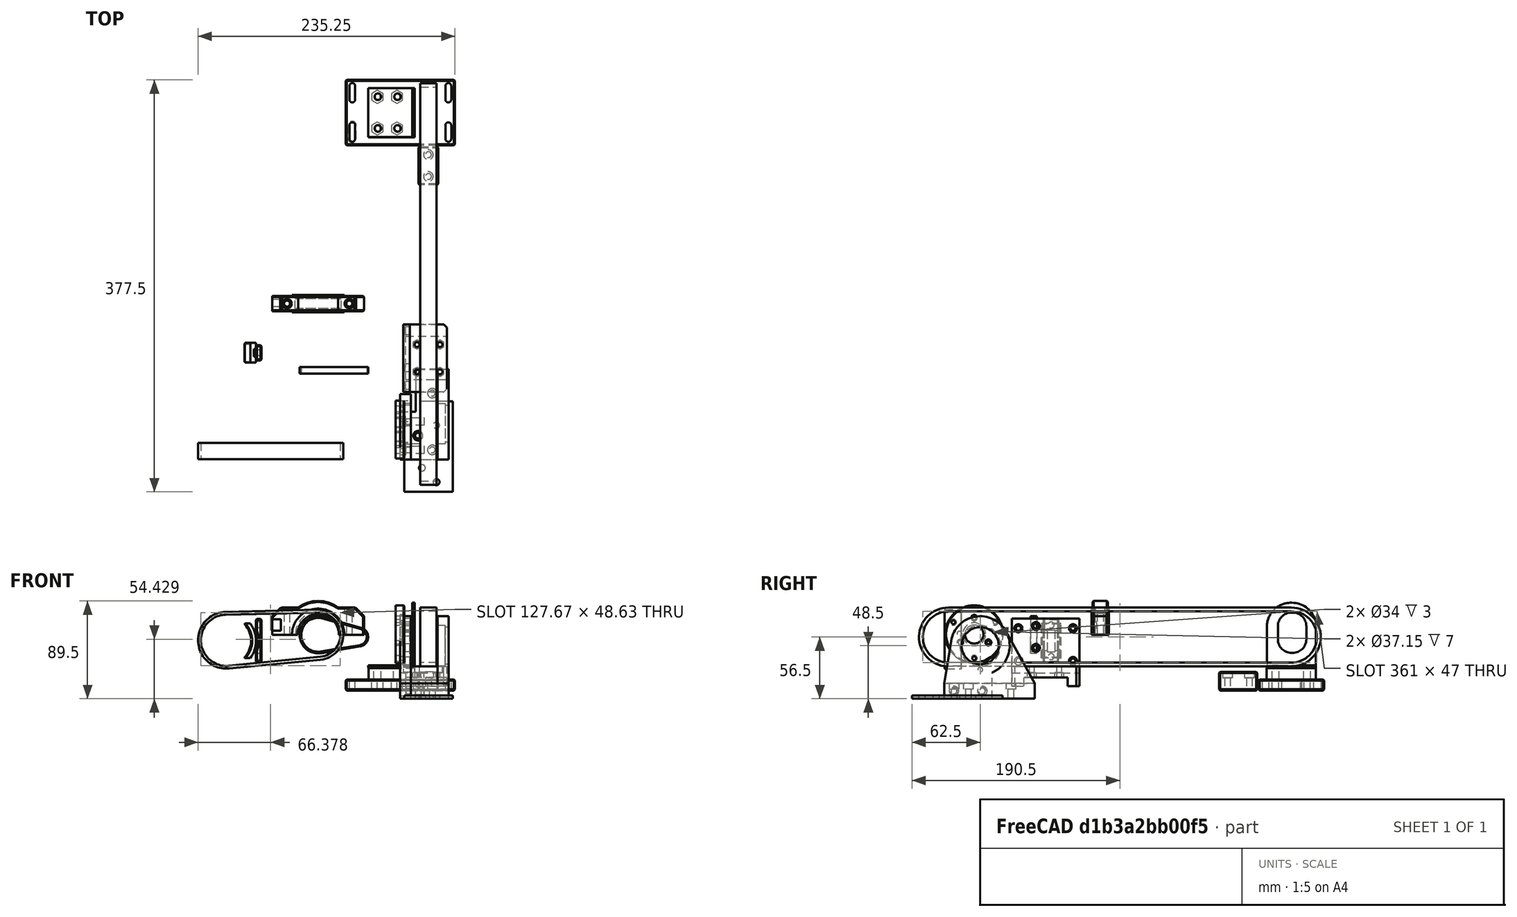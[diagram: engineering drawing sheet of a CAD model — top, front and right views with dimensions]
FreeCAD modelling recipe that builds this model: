
FCSTD DOCUMENT  (FreeCAD 0.21R33668 +26 (Git))
Label: FFB_Yoke_Assembly_v2
License: All rights reserved
LicenseURL: http://en.wikipedia.org/wiki/All_rights_reserved
objects: Sketcher::SketchObject×45, PartDesign::Pad×19, PartDesign::Pocket×17, App::Link×15, PartDesign::Body×14, PartDesign::Chamfer×13, PartDesign::Hole×9, Mesh::Feature×6, App::Part×3, PartDesign::Fillet×1, PartDesign::FeatureBase×1
note: 178 computed .brp shape members not serialized (recipe doc carries the construction recipe); baked Part::Feature solids carry a one-line shape summary decoded from their .brp
EXTERNAL_REF file=Parts/Frame.FCStd obj=Part
EXTERNAL_REF file=Parts/Frame_Roll_Limit_IR_Sensor_Mount.FCStd obj=Body022
EXTERNAL_REF file=Parts/Frame_Roll_Limit_Stop.FCStd obj=Body019
EXTERNAL_REF file=Parts/Roll_Motor_Mount.FCStd obj=Body005
EXTERNAL_REF file=Parts/Roll_Encoder_Mount.FCStd obj=Body026
EXTERNAL_REF file=Parts/GearMotor.FCStd obj=Part
EXTERNAL_REF file=Parts/Encoder.FCStd obj=Part
EXTERNAL_REF file=Parts/Yoke_Bearing.FCStd obj=Body008
EXTERNAL_REF file=Parts/Yoke_Roll_IR_Limit_Ring.FCStd obj=Body028
EXTERNAL_REF file=Parts/Yoke_Encoder_Pulley.FCStd obj=Body
EXTERNAL_REF file=Parts/Roll_Encoder_Pulley.FCStd obj=Part
EXTERNAL_REF file=Parts/Yoke Column.FCStd obj=Part

FEATURE [App::Link] Link  label="Frame"
  LinkedObject = -> <external Parts/Frame.FCStd>#Part
FEATURE [App::Link] Link001  label="Frame_Roll_IR_Sensor_Mount"
  LinkPlacement = pos=(0,-24,0) rot=(0,0,1;0rad)
  LinkedObject = -> <external Parts/Frame_Roll_Limit_IR_Sensor_Mount.FCStd>#Body022
  Placement = pos=(0,-24,0) rot=(0,0,1;0rad)
FEATURE [App::Link] Link002  label="Roll_Limit_Stop"
  LinkPlacement = pos=(0,24,0) rot=(0,0,1;3.14159rad)
  LinkedObject = -> <external Parts/Frame_Roll_Limit_Stop.FCStd>#Body019
  Placement = pos=(0,24,0) rot=(0,0,1;3.14159rad)
FEATURE [App::Link] Link003  label="Roll_Motor_Mount"
  LinkPlacement = pos=(-12,-24,0) rot=(0,0,1;0rad)
  LinkedObject = -> <external Parts/Roll_Motor_Mount.FCStd>#Body005
  Placement = pos=(-12,-24,0) rot=(0,0,1;0rad)
FEATURE [App::Link] Link004  label="Roll_Encoder _Mount"
  LinkPlacement = pos=(1,-27,0) rot=(0,0,1;0rad)
  LinkedObject = -> <external Parts/Roll_Encoder_Mount.FCStd>#Body026
  Placement = pos=(1,-27,0) rot=(0,0,1;0rad)
FEATURE [App::Link] Link005  label="Roll_GearMotor"
  LinkPlacement = pos=(-9,-24,0) rot=(0,0,1;0rad)
  LinkedObject = -> <external Parts/GearMotor.FCStd>#Part
  Placement = pos=(-9,-24,0) rot=(0,0,1;0rad)
FEATURE [App::Link] Link006  label="Pitch_GearMotor"
  LinkPlacement = pos=(88.5,350,3) rot=(0,0,1;1.5708rad)
  LinkedObject = -> <external Parts/GearMotor.FCStd>#Part
  Placement = pos=(88.5,350,3) rot=(0,0,1;1.5708rad)
FEATURE [App::Link] Link007  label="Roll_Encoder"
  LinkPlacement = pos=(-1,-30,0) rot=(0,0,1;0rad)
  LinkedObject = -> <external Parts/Encoder.FCStd>#Part
  Placement = pos=(-1,-30,0) rot=(0,0,1;0rad)
FEATURE [App::Link] Link008  label="Rear_Bearing"
  LinkPlacement = pos=(0,-27,0) rot=(0,0,1;0rad)
  LinkedObject = -> <external Parts/Yoke_Bearing.FCStd>#Body008
  Placement = pos=(0,-27,0) rot=(0,0,1;0rad)
FEATURE [App::Link] Link009  label="Front_Bearing"
  LinkPlacement = pos=(0,-127,0) rot=(0,0,1;0rad)
  LinkedObject = -> <external Parts/Yoke_Bearing.FCStd>#Body008
  Placement = pos=(0,-127,0) rot=(0,0,1;0rad)
FEATURE [App::Link] Link011  label="IR _Cam"
  LinkPlacement = pos=(0,3.75,-6.04e-14) rot=(-1,0,0;1.5708rad)
  LinkedObject = -> <external Parts/Yoke_Roll_IR_Limit_Ring.FCStd>#Body028
  Placement = pos=(0,3.75,-6.04e-14) rot=(-1,0,0;1.5708rad)
FEATURE [App::Link] Link012  label="Yoke_Roll_Encoder_Pulley"
  LinkPlacement = pos=(0,44.25,0) rot=(0,0,1;0rad)
  LinkedObject = -> <external Parts/Yoke_Encoder_Pulley.FCStd>#Body
  Placement = pos=(0,44.25,0) rot=(0,0,1;0rad)
FEATURE [App::Link] Link015  label="Roll_Encoder_Pulley"
  LinkPlacement = pos=(37,43,-2) rot=(1,0,0;1.5708rad)
  LinkedObject = -> <external Parts/Roll_Encoder_Pulley.FCStd>#Part
  Placement = pos=(37,43,-2) rot=(1,0,0;1.5708rad)
FEATURE [App::Link] Link019  label="Pitch_Encoder"
  LinkPlacement = pos=(152.75,-77,0) rot=(0,0,1;1.5708rad)
  LinkedObject = -> <external Parts/Encoder.FCStd>#Part
  Placement = pos=(152.75,-77,0) rot=(0,0,1;1.5708rad)
FEATURE [App::Link] Link021  label="Yoke_Column"
  LinkPlacement = pos=(0,-27,0) rot=(0,0,1;0rad)
  LinkedObject = -> <external Parts/Yoke Column.FCStd>#Part
  Placement = pos=(0,-27,0) rot=(0,0,1;0rad)
FEATURE [Sketcher::SketchObject] Sketch
  AttachmentOffset = pos=(0,0,-19) rot=(0,0,1;0rad)
  FullyConstrained = true
  MapMode = 5
  Placement = pos=(0,19,4.2e-15) rot=(1,0,0;1.5708rad)
  Support = -> [XZ_Plane]
  sketch-geometry (8):
    g0: LineSegment StartX=76 StartY=15 StartZ=0 EndX=76 EndY=-35 EndZ=0
    g1: LineSegment StartX=78 StartY=-47 StartZ=0 EndX=116 EndY=-47 EndZ=0
    g2: LineSegment StartX=116 StartY=-47 StartZ=0 EndX=116 EndY=-29 EndZ=0
    g3: LineSegment StartX=116 StartY=-29 StartZ=0 EndX=82 EndY=-29 EndZ=0
    g4: LineSegment StartX=82 StartY=-29 StartZ=0 EndX=82 EndY=15 EndZ=0
    g5: LineSegment StartX=82 StartY=15 StartZ=0 EndX=76 EndY=15 EndZ=0
    g6: LineSegment StartX=76 StartY=-35 StartZ=0 EndX=78 EndY=-35 EndZ=0
    g7: LineSegment StartX=78 StartY=-35 StartZ=0 EndX=78 EndY=-47 EndZ=0
  constraints (24):
    c: Vertical(g0)
    c: Horizontal(g1)
    c: Coincident(g1,g2)
    c: Coincident(g2,g3)
    c: Horizontal(g3)
    c: Coincident(g3,g4)
    c: Vertical(g4)
    c: Coincident(g4,g5)
    c: Coincident(g5,g0)
    c: Horizontal(g5)
    c: Vertical(g2)
    c: Distance(g2) = 18
    c: Distance(g5) = 6
    c: Distance(g4) = 44
    c: DistanceY(g0) = 15
    c: DistanceX(g0) = 76
    c: Horizontal(g6)
    c: Coincident(g7,g6)
    c: Vertical(g7)
    c: Distance(g6) = 2
    c: Distance(g7) = 12
    c: Distance(g3) = 34
    c: Coincident(g0,g6)
    c: Coincident(g1,g7)
FEATURE [PartDesign::Pad] Pad
  Direction = (0,-1,-2e-16)
  Length = 62
  Length2 = 10
  Placement = pos=(0,0,0) rot=(1,0,0;1.5708rad)
  Profile = -> Sketch
  ReferenceAxis = -> Sketch [N_Axis]
  Reversed = true
  Type = 0
FEATURE [Sketcher::SketchObject] Sketch001
  FullyConstrained = true
  MapMode = 5
  Placement = pos=(0,0,0) rot=(1,0,0;1.5708rad)
  Support = -> [XZ_Plane002]
  sketch-geometry (6):
    g0: LineSegment StartX=42 StartY=0 StartZ=0 EndX=42 EndY=25 EndZ=0
    g1: LineSegment StartX=42 StartY=25 StartZ=0 EndX=18.3303 EndY=25 EndZ=0
    g2: LineSegment StartX=-42 StartY=25 StartZ=0 EndX=-42 EndY=0 EndZ=0
    g3: LineSegment StartX=-42 StartY=0 StartZ=0 EndX=42 EndY=0 EndZ=0
    g4: ArcOfCircle CenterX=0 CenterY=0 CenterZ=0 NormalX=0 NormalY=0 NormalZ=1 AngleXU=0 Radius=31 StartAngle=0.938126 EndAngle=2.20347
    g5: LineSegment StartX=-18.3303 StartY=25 StartZ=0 EndX=-42 EndY=25 EndZ=0
  constraints (18):
    c: Coincident(g0,g1)
    c: Coincident(g5,g2)
    c: Horizontal(g1)
    c: Vertical(g0)
    c: Vertical(g2)
    c: PointOnObject(g2,g-1)
    c: Distance(g0) = 25
    c: DistanceX(g5,g-1) = 42
    c: Horizontal(g0,g-1)
    c: Coincident(g3,g2)
    c: Coincident(g3,g0)
    c: Coincident(g4,g-1)
    c: Diameter(g4) = 62
    c: Coincident(g1,g4)
    c: Coincident(g5,g4)
    c: Distance(g2,g0) = 84
    c: Horizontal(g5)
    c: Horizontal(g1,g4)
FEATURE [PartDesign::Pad] Pad001
  Direction = (0,-1,-2e-16)
  Length = 14
  Length2 = 10
  Midplane = true
  Placement = pos=(0,0,0) rot=(1,0,0;1.5708rad)
  Profile = -> Sketch001
  ReferenceAxis = -> Sketch001 [N_Axis]
  Type = 0
FEATURE [Sketcher::SketchObject] Sketch002
  FullyConstrained = true
  MapMode = 5
  Placement = pos=(0,0,0) rot=(1,0,0;1.5708rad)
  Support = -> [XZ_Plane002]
  sketch-geometry (2):
    g0: ArcOfCircle CenterX=0 CenterY=0 CenterZ=0 NormalX=0 NormalY=0 NormalZ=1 AngleXU=0 Radius=19 StartAngle=0 EndAngle=3.14159
    g1: LineSegment StartX=-19 StartY=0 StartZ=0 EndX=19 EndY=0 EndZ=0
  constraints (6):
    c: Horizontal(g0,g0)
    c: Horizontal(g0,g0)
    c: Coincident(g0,g-1)
    c: Diameter(g0) = 38
    c: Coincident(g1,g0)
    c: Coincident(g1,g0)
FEATURE [Sketcher::SketchObject] Sketch003
  FullyConstrained = true
  MapMode = 5
  Placement = pos=(0,0,0) rot=(1,0,0;1.5708rad)
  Support = -> [XZ_Plane002]
  sketch-geometry (2):
    g0: ArcOfCircle CenterX=0 CenterY=5.9e-15 CenterZ=0 NormalX=0 NormalY=0 NormalZ=1 AngleXU=0 Radius=24 StartAngle=0 EndAngle=3.14159
    g1: LineSegment StartX=-24 StartY=5.9e-15 StartZ=0 EndX=24 EndY=5.9e-15 EndZ=0
  constraints (6):
    c: Diameter(g0) = 48
    c: Horizontal(g0,g0)
    c: Horizontal(g0,g0)
    c: Coincident(g0,g-1)
    c: Coincident(g1,g0)
    c: Coincident(g1,g0)
FEATURE [Sketcher::SketchObject] Sketch004
  FullyConstrained = true
  MapMode = 5
  Placement = pos=(0,0,0) rot=(1,0,0;1.5708rad)
  Support = -> [XZ_Plane002]
  sketch-geometry (2):
    g0: ArcOfCircle CenterX=0 CenterY=0 CenterZ=0 NormalX=0 NormalY=0 NormalZ=1 AngleXU=0 Radius=21 StartAngle=0 EndAngle=3.14159
    g1: LineSegment StartX=-21 StartY=2.6e-15 StartZ=0 EndX=21 EndY=0 EndZ=0
  constraints (6):
    c: PointOnObject(g0,g-1)
    c: Diameter(g0) = 42
    c: Coincident(g0,g-1)
    c: Horizontal(g0,g0)
    c: Coincident(g1,g0)
    c: Coincident(g1,g0)
FEATURE [PartDesign::Pad] Pad002
  BaseFeature = -> Pad001
  Direction = (0,-1,-2e-16)
  Length = 16
  Length2 = 10
  Midplane = true
  Placement = pos=(0,0,0) rot=(1,0,0;1.5708rad)
  Profile = -> Sketch003
  ReferenceAxis = -> Sketch003 [N_Axis]
  Type = 0
FEATURE [PartDesign::Pocket] Pocket
  BaseFeature = -> Pad002
  Direction = (0,1,2e-16)
  Length = 16
  Length2 = 5
  Midplane = true
  Placement = pos=(0,0,0) rot=(1,0,0;1.5708rad)
  Profile = -> Sketch002
  ReferenceAxis = -> Sketch002 [N_Axis]
  Type = 0
FEATURE [PartDesign::Pocket] Pocket001
  BaseFeature = -> Pocket
  Direction = (0,1,2e-16)
  Length = 9.2
  Length2 = 5
  Midplane = true
  Placement = pos=(0,0,0) rot=(1,0,0;1.5708rad)
  Profile = -> Sketch004
  ReferenceAxis = -> Sketch004 [N_Axis]
  Type = 0
FEATURE [Sketcher::SketchObject] Sketch006
  FullyConstrained = true
  MapMode = 5
  Support = -> [XY_Plane002]
  sketch-geometry (2):
    g0: Circle CenterX=-28.5 CenterY=0 CenterZ=0 NormalX=0 NormalY=0 NormalZ=1 AngleXU=0 Radius=2.75
    g1: Circle CenterX=28.5 CenterY=0 CenterZ=0 NormalX=0 NormalY=0 NormalZ=1 AngleXU=0 Radius=2.75
  constraints (5):
    c: Symmetric(g0,g1,g-1)
    c: Horizontal(g0,g-1)
    c: Distance(g0,g1) = 57
    c: Equal(g1,g0)
    c: Diameter(g1) = 5.5
FEATURE [PartDesign::Pocket] Pocket003
  BaseFeature = -> Pocket001
  Direction = (0,0,-1)
  Length = 5
  Length2 = 5
  Placement = pos=(0,0,0) rot=(1,0,0;1.5708rad)
  Profile = -> Sketch006
  ReferenceAxis = -> Sketch006 [N_Axis]
  Reversed = true
  Type = 1
FEATURE [Sketcher::SketchObject] Sketch007
  AttachmentOffset = pos=(0,0,25) rot=(0,0,1;0rad)
  FullyConstrained = true
  MapMode = 5
  Placement = pos=(0,0,25) rot=(0,0,1;0rad)
  Support = -> [XY_Plane002]
  sketch-geometry (2):
    g0: Circle CenterX=-28.5 CenterY=0 CenterZ=0 NormalX=0 NormalY=0 NormalZ=1 AngleXU=0 Radius=4.35
    g1: Circle CenterX=28.5 CenterY=0 CenterZ=0 NormalX=0 NormalY=0 NormalZ=1 AngleXU=0 Radius=4.35
  constraints (5):
    c: PointOnObject(g0,g-1)
    c: Symmetric(g0,g1,g-1)
    c: Distance(g0,g1) = 57
    c: Equal(g0,g1)
    c: Diameter(g0) = 8.7
FEATURE [PartDesign::Pocket] Pocket004
  BaseFeature = -> Pocket003
  Direction = (0,0,-1)
  Length = 5.4
  Length2 = 5
  Placement = pos=(0,0,0) rot=(1,0,0;1.5708rad)
  Profile = -> Sketch007
  ReferenceAxis = -> Sketch007 [N_Axis]
  Type = 0
FEATURE [Mesh::Feature] HTD_32_5M_15_Pulley_v8  label="HTD 32 5M 15 Pulley v8"
  Placement = pos=(111.5,275,-2) rot=(0,0,1;3.14159rad)
FEATURE [Sketcher::SketchObject] Sketch008
  FullyConstrained = true
  MapMode = 5
  Placement = pos=(0,0,0) rot=(0.57735,0.57735,0.57735;2.0944rad)
  Support = -> [YZ_Plane003]
  sketch-geometry (4):
    g0: ArcOfCircle CenterX=-39 CenterY=-3 CenterZ=0 NormalX=0 NormalY=0 NormalZ=1 AngleXU=0 Radius=27 StartAngle=1.5708 EndAngle=4.71239
    g1: ArcOfCircle CenterX=275 CenterY=-3 CenterZ=0 NormalX=0 NormalY=0 NormalZ=1 AngleXU=0 Radius=27 StartAngle=4.71239 EndAngle=7.85398
    g2: LineSegment StartX=-39 StartY=24 StartZ=0 EndX=275 EndY=24 EndZ=0
    g3: LineSegment StartX=275 StartY=-30 StartZ=0 EndX=-39 EndY=-30 EndZ=0
  constraints (13):
    c: Diameter(g0) = 54
    c: Equal(g1,g0)
    c: DistanceY(g0) = -3
    c: DistanceX(g0) = -39
    c: Horizontal(g2)
    c: Coincident(g1,g2)
    c: Coincident(g1,g3)
    c: Coincident(g0,g3)
    c: Tangent(g0,g2) = 1.5708
    c: DistanceX(g1) = 275
    c: Vertical(g0,g0)
    c: Vertical(g1,g1)
    c: Vertical(g1,g1)
FEATURE [PartDesign::Pad] Pad003
  Direction = (1,-2e-16,3e-16)
  Length = 15
  Length2 = 10
  Midplane = true
  Placement = pos=(0,0,0) rot=(0.57735,0.57735,0.57735;2.0944rad)
  Profile = -> Sketch008
  ReferenceAxis = -> Sketch008 [N_Axis]
  Type = 0
FEATURE [Sketcher::SketchObject] Sketch009
  FullyConstrained = true
  MapMode = 5
  Placement = pos=(0,0,0) rot=(0.57735,0.57735,0.57735;2.0944rad)
  Support = -> [YZ_Plane003]
  sketch-geometry (4):
    g0: ArcOfCircle CenterX=-39 CenterY=-3 CenterZ=0 NormalX=0 NormalY=0 NormalZ=1 AngleXU=0 Radius=23.5 StartAngle=1.5708 EndAngle=4.71239
    g1: ArcOfCircle CenterX=275 CenterY=-3 CenterZ=0 NormalX=0 NormalY=0 NormalZ=1 AngleXU=0 Radius=23.5 StartAngle=4.71239 EndAngle=7.85398
    g2: LineSegment StartX=-39 StartY=20.5 StartZ=0 EndX=275 EndY=20.5 EndZ=0
    g3: LineSegment StartX=275 StartY=-26.5 StartZ=0 EndX=-39 EndY=-26.5 EndZ=0
  constraints (13):
    c: Diameter(g1) = 47
    c: Equal(g1,g0)
    c: DistanceY(g0) = -3
    c: DistanceX(g0) = -39
    c: DistanceX(g1) = 275
    c: Horizontal(g2)
    c: Vertical(g2,g0)
    c: Vertical(g0,g3)
    c: Coincident(g0,g3)
    c: Coincident(g0,g2)
    c: Tangent(g1,g2) = 1.5708
    c: Coincident(g1,g3)
    c: Vertical(g1,g1)
FEATURE [PartDesign::Pocket] Pocket005
  BaseFeature = -> Pad003
  Direction = (-1,2e-16,-3e-16)
  Length = 15
  Length2 = 5
  Midplane = true
  Placement = pos=(0,0,0) rot=(0.57735,0.57735,0.57735;2.0944rad)
  Profile = -> Sketch009
  ReferenceAxis = -> Sketch009 [N_Axis]
  Type = 0
FEATURE [PartDesign::Body] Body001002  label="Pitch_Belt"
  Group = -> [Sketch008,Pad003,Sketch009,Pocket005]
  Origin = -> Origin003
  Placement = pos=(101,0,1) rot=(0,0,1;0rad)
  Tip = -> Pocket005
FEATURE [Mesh::Feature] HTD_32_5M_15_Pulley_v8001  label="HTD 32 5M 15 Pulley v009"
  Placement = pos=(-84,-46,-5) rot=(0,0,1;1.5708rad)
FEATURE [Sketcher::SketchObject] Sketch010
  AttachmentOffset = pos=(-4,0,35) rot=(0,0,1;0rad)
  FullyConstrained = true
  MapMode = 5
  Placement = pos=(-4,-35,-7.8e-15) rot=(1,0,0;1.5708rad)
  Support = -> [XZ_Plane004]
  sketch-geometry (4):
    g0: ArcOfCircle CenterX=4 CenterY=0 CenterZ=0 NormalX=0 NormalY=0 NormalZ=1 AngleXU=0 Radius=23 StartAngle=4.8075 EndAngle=7.87778
    g1: LineSegment StartX=-80.6186 StartY=20.9926 StartZ=0 EndX=3.45277 EndY=22.9935 EndZ=0
    g2: LineSegment StartX=-77.5308 StartY=-30.8825 StartZ=0 EndX=6.18429 EndY=-22.896 EndZ=0
    g3: ArcOfCircle CenterX=-80 CenterY=-5 CenterZ=0 NormalX=0 NormalY=0 NormalZ=1 AngleXU=0 Radius=26 StartAngle=1.59459 EndAngle=4.8075
  constraints (10):
    c: PointOnObject(g0,g-1)
    c: DistanceX(g0) = 4
    c: Tangent(g0,g1) = 1.5708
    c: Diameter(g0) = 46
    c: Tangent(g0,g2) = -1.5708
    c: DistanceY(g3) = -5
    c: DistanceX(g3) = -80
    c: Diameter(g3) = 52
    c: Tangent(g3,g2) = -1.5708
    c: Tangent(g3,g1) = 1.5708
FEATURE [PartDesign::Pad] Pad004
  Direction = (0,-1,-2e-16)
  Length = 15
  Length2 = 10
  Midplane = true
  Placement = pos=(0,0,0) rot=(1,0,0;1.5708rad)
  Profile = -> Sketch010
  ReferenceAxis = -> Sketch010 [N_Axis]
  Type = 0
FEATURE [Sketcher::SketchObject] Sketch011
  AttachmentOffset = pos=(-4,0,35) rot=(0,0,1;0rad)
  FullyConstrained = true
  MapMode = 5
  Placement = pos=(-4,-35,-7.8e-15) rot=(1,0,0;1.5708rad)
  Support = -> [XZ_Plane004]
  sketch-geometry (4):
    g0: ArcOfCircle CenterX=-80 CenterY=-5 CenterZ=0 NormalX=0 NormalY=0 NormalZ=1 AngleXU=0 Radius=23.5 StartAngle=1.59162 EndAngle=4.81047
    g1: ArcOfCircle CenterX=4 CenterY=0 CenterZ=0 NormalX=0 NormalY=0 NormalZ=1 AngleXU=0 Radius=20.25 StartAngle=4.81047 EndAngle=7.8748
    g2: LineSegment StartX=-80.4893 StartY=18.4949 StartZ=0 EndX=3.57839 EndY=20.2456 EndZ=0
    g3: LineSegment StartX=-77.6987 StartY=-28.387 StartZ=0 EndX=5.98305 EndY=-20.1527 EndZ=0
  constraints (10):
    c: Diameter(g0) = 47
    c: Diameter(g1) = 40.5
    c: Tangent(g1,g2) = 1.5708
    c: Tangent(g1,g3) = -1.5708
    c: Tangent(g0,g3) = -1.5708
    c: Tangent(g0,g2) = 1.5708
    c: DistanceX(g0) = -80
    c: DistanceY(g0) = -5
    c: DistanceY(g1) = 0
    c: DistanceX(g1) = 4
FEATURE [PartDesign::Pocket] Pocket006
  BaseFeature = -> Pad004
  Direction = (0,1,2e-16)
  Length = 15
  Length2 = 5
  Midplane = true
  Placement = pos=(0,0,0) rot=(1,0,0;1.5708rad)
  Profile = -> Sketch011
  ReferenceAxis = -> Sketch011 [N_Axis]
  Type = 0
FEATURE [PartDesign::Body] Body001003  label="Roll_Belt"
  Group = -> [Sketch010,Sketch011,Pad004,Pocket006]
  Origin = -> Origin004
  Tip = -> Pocket006
FEATURE [Sketcher::SketchObject] Sketch017
  AttachmentOffset = pos=(3,-3,-40) rot=(0,0,1;0rad)
  FullyConstrained = false
  MapMode = 5
  Placement = pos=(-40,3,-3) rot=(0.57735,0.57735,0.57735;2.0944rad)
  Support = -> [YZ_Plane009]
  sketch-geometry (8):
    g0: LineSegment StartX=-2.53905 StartY=-25.1351 StartZ=0 EndX=39.4609 EndY=-25.1351 EndZ=0
    g1: LineSegment StartX=39.4609 StartY=-25.1351 StartZ=0 EndX=39.4609 EndY=19.8649 EndZ=0
    g2: LineSegment StartX=39.4609 StartY=19.8649 StartZ=0 EndX=-2.53905 EndY=19.8649 EndZ=0
    g3: LineSegment StartX=-2.53905 StartY=19.8649 StartZ=0 EndX=-2.53905 EndY=-25.1351 EndZ=0
    g4: Circle CenterX=12.4609 CenterY=11.8649 CenterZ=0 NormalX=0 NormalY=0 NormalZ=1 AngleXU=0 Radius=3
    g5: Circle CenterX=30.4609 CenterY=11.8649 CenterZ=0 NormalX=0 NormalY=0 NormalZ=1 AngleXU=0 Radius=3
    g6: Circle CenterX=30.4609 CenterY=-17.1351 CenterZ=0 NormalX=0 NormalY=0 NormalZ=1 AngleXU=0 Radius=3
    g7: Circle CenterX=12.4609 CenterY=-17.1351 CenterZ=0 NormalX=0 NormalY=0 NormalZ=1 AngleXU=0 Radius=3
  constraints (22):
    c: Coincident(g0,g1)
    c: Coincident(g1,g2)
    c: Coincident(g2,g3)
    c: Coincident(g3,g0)
    c: Horizontal(g0)
    c: Horizontal(g2)
    c: Vertical(g1)
    c: Vertical(g3)
    c: DistanceX(g2,g2) = 42
    c: DistanceY(g1,g1) = 45
    c: Horizontal(g4,g5)
    c: Horizontal(g7,g6)
    c: Vertical(g6,g5)
    c: Vertical(g4,g7)
    c: DistanceY(g6,g5) = 29
    c: DistanceY(g0,g6) = 8
    c: Equal(g4,g5)
    c: Equal(g4,g7)
    c: Equal(g4,g6)
    c: Diameter(g4) = 6
    c: DistanceX(g4,g5) = 18
    c: DistanceX(g2,g4) = 15
FEATURE [PartDesign::Pad] Pad012
  Direction = (1,-2e-16,3e-16)
  Length = 2
  Length2 = 10
  Placement = pos=(0,0,0) rot=(0.57735,0.57735,0.57735;2.0944rad)
  Profile = -> Sketch017
  ReferenceAxis = -> Sketch017 [N_Axis]
  Reversed = true
  Type = 0
FEATURE [Sketcher::SketchObject] Sketch018
  AttachmentOffset = pos=(-21,-3,0) rot=(0,0,1;0rad)
  FullyConstrained = false
  MapMode = 5
  Placement = pos=(-21,7e-16,-3) rot=(1,0,0;1.5708rad)
  Support = -> [XZ_Plane009]
  sketch-geometry (12):
    g0: LineSegment StartX=-20.9755 StartY=19.8621 StartZ=0 EndX=-78.4755 EndY=19.8621 EndZ=0
    g1: LineSegment StartX=-78.4755 StartY=19.8621 StartZ=0 EndX=-78.4755 EndY=-25.1379 EndZ=0
    g2: LineSegment StartX=-78.4755 StartY=-25.1379 StartZ=0 EndX=-20.9755 EndY=-25.1379 EndZ=0
    g3: LineSegment StartX=-20.9755 StartY=-25.1379 StartZ=0 EndX=-20.9755 EndY=19.8621 EndZ=0
    g4: LineSegment StartX=-57 StartY=-15 StartZ=0 EndX=-45 EndY=-15 EndZ=0
    g5: LineSegment StartX=-32.5 StartY=-2.5 StartZ=0 EndX=-32.5 EndY=-1.5 EndZ=0
    g6: LineSegment StartX=-45 StartY=11 StartZ=0 EndX=-57 EndY=11 EndZ=0
    g7: LineSegment StartX=-69.5 StartY=-1.5 StartZ=0 EndX=-69.5 EndY=-2.5 EndZ=0
    g8: ArcOfCircle CenterX=-57 CenterY=-2.5 CenterZ=0 NormalX=0 NormalY=0 NormalZ=1 AngleXU=0 Radius=12.5 StartAngle=3.14159 EndAngle=4.71239
    g9: ArcOfCircle CenterX=-57 CenterY=-1.5 CenterZ=0 NormalX=0 NormalY=0 NormalZ=1 AngleXU=0 Radius=12.5 StartAngle=1.5708 EndAngle=3.14159
    g10: ArcOfCircle CenterX=-45 CenterY=-1.5 CenterZ=0 NormalX=0 NormalY=0 NormalZ=1 AngleXU=0 Radius=12.5 StartAngle=0 EndAngle=1.5708
    g11: ArcOfCircle CenterX=-45 CenterY=-2.5 CenterZ=0 NormalX=0 NormalY=0 NormalZ=1 AngleXU=0 Radius=12.5 StartAngle=4.71239 EndAngle=6.28319
  constraints (30):
    c: Coincident(g0,g1)
    c: Coincident(g1,g2)
    c: Coincident(g2,g3)
    c: Coincident(g3,g0)
    c: Horizontal(g0)
    c: Horizontal(g2)
    c: Vertical(g1)
    c: Vertical(g3)
    c: DistanceY(g3,g3) = 45
    c: DistanceX(g0,g0) = 57.5
    c: Horizontal(g4)
    c: Horizontal(g6)
    c: Vertical(g5)
    c: Vertical(g7)
    c: Tangent(g7,g8) = -1.5708
    c: Tangent(g4,g8) = -1.5708
    c: Tangent(g7,g9) = -1.5708
    c: Tangent(g6,g9) = -1.5708
    c: Tangent(g6,g10) = -1.5708
    c: Tangent(g5,g10) = -1.5708
    c: Tangent(g4,g11) = -1.5708
    c: Tangent(g5,g11) = -1.5708
    c: Equal(g9,g10)
    c: Equal(g9,g11)
    c: Equal(g9,g8)
    c: Diameter(g9) = 25
    c: DistanceY(g4,g6) = 26
    c: DistanceX(g6,g6) = 12
    c: DistanceY(g4) = -15
    c: DistanceX(g4) = -45
FEATURE [PartDesign::Pad] Pad013
  BaseFeature = -> Pad012
  Direction = (0,-1,-2e-16)
  Length = 2
  Length2 = 10
  Placement = pos=(0,0,0) rot=(0.57735,0.57735,0.57735;2.0944rad)
  Profile = -> Sketch018
  ReferenceAxis = -> Sketch018 [N_Axis]
  Reversed = true
  Type = 0
FEATURE [PartDesign::Fillet] Fillet
  Base = -> Pad013 [Edge48,Edge47]
  BaseFeature = -> Pad013
  Placement = pos=(0,0,0) rot=(0.57735,0.57735,0.57735;2.0944rad)
  Radius = 22
  SupportTransform = false
  UseAllEdges = false
FEATURE [PartDesign::Body] Body005  label="Roll Motor Mount"
  Group = -> [Sketch017,Pad012,Sketch018,Pad013,Fillet]
  Origin = -> Origin009
  Placement = pos=(88.25,280.742,-70.0964) rot=(0.57735,-0.57735,-0.57735;4.18879rad)
  Tip = -> Fillet
FEATURE [Mesh::Feature] Clamping_Plate_v1  label="Clamping_Plate v1"
  Placement = pos=(118,29,-19) rot=(-0.57735,-0.57735,0.57735;2.0944rad)
FEATURE [Sketcher::SketchObject] Sketch019
  AttachmentOffset = pos=(0,0,-40) rot=(0,0,1;0rad)
  FullyConstrained = true
  MapMode = 5
  Placement = pos=(0,40,8.9e-15) rot=(1,0,0;1.5708rad)
  Support = -> [XZ_Plane011]
  sketch-geometry (4):
    g0: ArcOfCircle CenterX=0 CenterY=0 CenterZ=0 NormalX=0 NormalY=0 NormalZ=1 AngleXU=0 Radius=17 StartAngle=1.29227 EndAngle=4.88292
    g1: ArcOfCircle CenterX=37 CenterY=-2 CenterZ=0 NormalX=0 NormalY=0 NormalZ=1 AngleXU=0 Radius=8.75 StartAngle=4.88292 EndAngle=7.57545
    g2: LineSegment StartX=4.67404 StartY=16.3448 StartZ=0 EndX=39.4058 EndY=6.41278 EndZ=0
    g3: LineSegment StartX=2.88495 StartY=-16.7534 StartZ=0 EndX=38.4849 EndY=-10.6231 EndZ=0
  constraints (9):
    c: Coincident(g0,g-1)
    c: DistanceX(g1) = 37
    c: DistanceY(g1) = -2
    c: Diameter(g1) = 17.5
    c: Diameter(g0) = 34
    c: Tangent(g0,g3) = -1.5708
    c: Tangent(g0,g2) = 1.5708
    c: Tangent(g1,g2) = 1.5708
    c: Tangent(g1,g3) = -1.5708
FEATURE [PartDesign::Pad] Pad014
  Direction = (0,-1,-2e-16)
  Length = 6
  Length2 = 10
  Midplane = true
  Placement = pos=(0,0,0) rot=(1,0,0;1.5708rad)
  Profile = -> Sketch019
  ReferenceAxis = -> Sketch019 [N_Axis]
  Type = 0
FEATURE [Sketcher::SketchObject] Sketch020
  AttachmentOffset = pos=(0,0,-41.5) rot=(0,0,1;0rad)
  FullyConstrained = true
  MapMode = 5
  Placement = pos=(0,41.5,9.2e-15) rot=(1,0,0;1.5708rad)
  Support = -> [XZ_Plane011]
  sketch-geometry (4):
    g0: ArcOfCircle CenterX=0 CenterY=0 CenterZ=0 NormalX=0 NormalY=0 NormalZ=1 AngleXU=0 Radius=15.5 StartAngle=1.29918 EndAngle=4.876
    g1: ArcOfCircle CenterX=37 CenterY=-2 CenterZ=0 NormalX=0 NormalY=0 NormalZ=1 AngleXU=0 Radius=7.5 StartAngle=4.876 EndAngle=7.58237
    g2: LineSegment StartX=4.15847 StartY=14.9317 StartZ=0 EndX=39.0122 EndY=5.22504 EndZ=0
    g3: LineSegment StartX=2.5247 StartY=-15.293 StartZ=0 EndX=38.2216 EndY=-9.39984 EndZ=0
  constraints (9):
    c: Coincident(g0,g-1)
    c: DistanceY(g1) = -2
    c: DistanceX(g1) = 37
    c: Diameter(g1) = 15
    c: Diameter(g0) = 31
    c: Tangent(g0,g3) = -1.5708
    c: Tangent(g0,g2) = 1.5708
    c: Tangent(g1,g2) = 1.5708
    c: Tangent(g1,g3) = -1.5708
FEATURE [PartDesign::Pocket] Pocket007
  BaseFeature = -> Pad014
  Direction = (0,1,2e-16)
  Length = 9
  Length2 = 5
  Midplane = true
  Placement = pos=(0,0,0) rot=(1,0,0;1.5708rad)
  Profile = -> Sketch020
  ReferenceAxis = -> Sketch020 [N_Axis]
  Type = 0
FEATURE [PartDesign::Body] Body001005  label="Roll_Encoder_Belt"
  Group = -> [Sketch019,Pad014,Sketch020,Pocket007]
  Origin = -> Origin011
  Placement = pos=(0,-1,0) rot=(0,0,1;0rad)
  Tip = -> Pocket007
FEATURE [PartDesign::Chamfer] Chamfer005
  Angle = 45
  Base = -> Pocket004 [Edge35,Edge2]
  BaseFeature = -> Pocket004
  ChamferType = 0
  FlipDirection = false
  Placement = pos=(0,0,0) rot=(1,0,0;1.5708rad)
  Size = 8
  Size2 = 1
  SupportTransform = false
  UseAllEdges = false
FEATURE [PartDesign::Chamfer] Chamfer006
  Angle = 45
  Base = -> Chamfer005 [Edge25,Edge23,Edge21,Edge19,Edge15,Edge4]
  BaseFeature = -> Chamfer005
  ChamferType = 0
  FlipDirection = false
  Placement = pos=(0,0,0) rot=(1,0,0;1.5708rad)
  Size = 1
  Size2 = 1
  SupportTransform = false
  UseAllEdges = false
FEATURE [PartDesign::Chamfer] Chamfer007
  Angle = 45
  Base = -> Chamfer006 [Edge3,Edge6,Edge12,Edge14,Edge16,Edge18]
  BaseFeature = -> Chamfer006
  ChamferType = 0
  FlipDirection = false
  Placement = pos=(0,0,0) rot=(1,0,0;1.5708rad)
  Size = 1
  Size2 = 1
  SupportTransform = false
  UseAllEdges = false
FEATURE [PartDesign::Chamfer] Chamfer008
  Angle = 45
  Base = -> Chamfer007 [Edge93,Edge7]
  BaseFeature = -> Chamfer007
  ChamferType = 0
  FlipDirection = false
  Placement = pos=(0,0,0) rot=(1,0,0;1.5708rad)
  Size = 1
  Size2 = 1
  SupportTransform = false
  UseAllEdges = false
FEATURE [Sketcher::SketchObject] Sketch021
  AttachmentOffset = pos=(-77,10,-34) rot=(0,0,1;0rad)
  FullyConstrained = true
  MapMode = 5
  Placement = pos=(-34,-77,10) rot=(0.57735,0.57735,0.57735;2.0944rad)
  Support = -> [YZ_Plane002]
  sketch-geometry (2):
    g0: Circle CenterX=68.5 CenterY=-1 CenterZ=0 NormalX=0 NormalY=0 NormalZ=1 AngleXU=0 Radius=5.5
    g1: Circle CenterX=86.5 CenterY=-1 CenterZ=0 NormalX=0 NormalY=0 NormalZ=1 AngleXU=0 Radius=5.5
  constraints (6):
    c: Distance(g1,g0) = 18
    c: Horizontal(g1,g0)
    c: DistanceY(g1) = -1
    c: DistanceX(g1) = 86.5
    c: Diameter(g0) = 11
    c: Equal(g0,g1)
FEATURE [PartDesign::Pocket] Pocket008
  BaseFeature = -> Chamfer008
  Direction = (-1,2e-16,-3e-16)
  Length = 5
  Length2 = 5
  Placement = pos=(0,0,0) rot=(1,0,0;1.5708rad)
  Profile = -> Sketch021
  ReferenceAxis = -> Sketch021 [N_Axis]
  Type = 2
FEATURE [PartDesign::Body] Body001
  Group = -> [Sketch001,Pad001,Sketch002,Sketch003,Sketch004,Pad002,Pocket,Pocket001,Sketch006,Pocket003,Sketch007,Pocket004,Chamfer005,Chamfer006,Chamfer007,Chamfer008,Sketch021,Pocket008]
  Origin = -> Origin002
  Placement = pos=(0,100,0) rot=(0,0,1;0rad)
  Tip = -> Pocket008
FEATURE [App::Part] Part  label="Rear_Yoke_Shaft_Housing_Top"
  Group = -> [Body001]
  Origin = -> Origin001
  Placement = pos=(0,-100,0) rot=(0,0,1;0rad)
FEATURE [PartDesign::FeatureBase] Clone
  BaseFeature = -> Body001
  Placement = pos=(0,100,0) rot=(0,0,1;0rad)
FEATURE [PartDesign::Body] Body001006  label="Rear_Yoke_Column_Upper_Mount"
  BaseFeature = -> Body001
  Group = -> [Clone]
  Origin = -> Origin012
  Tip = -> Clone
FEATURE [Sketcher::SketchObject] Sketch029
  AttachmentOffset = pos=(0,0,82) rot=(0,0,1;0rad)
  FullyConstrained = true
  MapMode = 5
  Placement = pos=(82,-1.82e-14,1.82e-14) rot=(0.57735,0.57735,0.57735;2.0944rad)
  Support = -> [YZ_Plane]
  sketch-geometry (6):
    g0: Circle CenterX=25 CenterY=-24 CenterZ=0 NormalX=0 NormalY=0 NormalZ=1 AngleXU=0 Radius=2.1
    g1: Circle CenterX=25 CenterY=6 CenterZ=0 NormalX=0 NormalY=0 NormalZ=1 AngleXU=0 Radius=2.1
    g2: Circle CenterX=41 CenterY=8 CenterZ=0 NormalX=0 NormalY=0 NormalZ=1 AngleXU=0 Radius=2.1
    g3: Circle CenterX=41 CenterY=-12 CenterZ=0 NormalX=0 NormalY=0 NormalZ=1 AngleXU=0 Radius=2.1
    g4: Circle CenterX=75 CenterY=6 CenterZ=0 NormalX=0 NormalY=0 NormalZ=1 AngleXU=0 Radius=2.1
    g5: Circle CenterX=75 CenterY=-24 CenterZ=0 NormalX=0 NormalY=0 NormalZ=1 AngleXU=0 Radius=2.1
  constraints (18):
    c: DistanceX(g2) = 41
    c: Vertical(g2,g3)
    c: Distance(g2,g3) = 20
    c: Diameter(g2) = 4.2
    c: Equal(g2,g3)
    c: DistanceY(g2) = 8
    c: DistanceX(g0) = 25
    c: DistanceY(g0) = -24
    c: Vertical(g0,g1)
    c: Horizontal(g0,g5)
    c: Vertical(g5,g4)
    c: Horizontal(g1,g4)
    c: Distance(g0,g5) = 50
    c: Diameter(g0) = 4.2
    c: Equal(g0,g1)
    c: Equal(g1,g4)
    c: Equal(g4,g5)
    c: Distance(g0,g1) = 30
FEATURE [PartDesign::Hole] Hole
  BaseFeature = -> Pad
  CustomThreadClearance = 0
  Depth = 25
  DepthType = 0
  Diameter = 4.5
  DrillForDepth = false
  DrillPoint = 1
  DrillPointAngle = 118
  HoleCutCountersinkAngle = 90
  HoleCutCustomValues = false
  HoleCutDepth = 4.4
  HoleCutDiameter = 7.4
  HoleCutType = 1
  ModelThread = false
  Placement = pos=(0,0,0) rot=(1,0,0;1.5708rad)
  Profile = -> Sketch029
  Tapered = false
  TaperedAngle = 90
  ThreadClass = 0
  ThreadDepth = 25
  ThreadDepthType = 0
  ThreadDirection = 0
  ThreadFit = 0
  ThreadSize = 11
  ThreadType = 1
  Threaded = false
  UseCustomThreadClearance = false
FEATURE [Sketcher::SketchObject] Sketch030
  FullyConstrained = true
  MapMode = 5
  Placement = pos=(0,0,0) rot=(1,0,0;1.5708rad)
  Support = -> [XZ_Plane015]
  sketch-geometry (7):
    g0: ArcOfCircle CenterX=-84 CenterY=-5.5 CenterZ=0 NormalX=0 NormalY=0 NormalZ=1 AngleXU=0 Radius=27 StartAngle=5.65305 EndAngle=6.91332
    g1: ArcOfCircle CenterX=-84 CenterY=-5.5 CenterZ=0 NormalX=0 NormalY=0 NormalZ=1 AngleXU=0 Radius=22.5 StartAngle=5.49779 EndAngle=7.06858
    g2: LineSegment StartX=-84 StartY=-5.5 StartZ=0 EndX=-68.0901 EndY=10.4099 EndZ=0
    g3: LineSegment StartX=-84 StartY=-5.5 StartZ=0 EndX=-68.0901 EndY=-21.4099 EndZ=0
    g4: LineSegment StartX=-84 StartY=-5.5 StartZ=0 EndX=-84 EndY=24.5 EndZ=0
    g5: LineSegment StartX=-68.0901 StartY=-21.4099 StartZ=0 EndX=-62.1854 EndY=-21.4099 EndZ=0
    g6: LineSegment StartX=-68.0901 StartY=10.4099 StartZ=0 EndX=-62.1854 EndY=10.4099 EndZ=0
  constraints (21):
    c: Coincident(g1,g0)
    c: Coincident(g2,g0)
    c: Coincident(g3,g0)
    c: Coincident(g4,g0)
    c: Vertical(g4)
    c: Distance(g4) = 30
    c: DistanceY(g0) = -5.5
    c: DistanceX(g0) = -84
    c: Diameter(g1) = 45
    c: Diameter(g0) = 54
    c: Angle(g2,g4) = 0.785398
    c: Angle(g3,g4) = 2.35619
    c: PointOnObject(g1,g3)
    c: Coincident(g5,g1)
    c: Horizontal(g5)
    c: Coincident(g2,g1)
    c: Coincident(g6,g1)
    c: Horizontal(g6)
    c: Coincident(g6,g0)
    c: Coincident(g0,g5)
    c: PointOnObject(g3,g5)
FEATURE [PartDesign::Pad] Pad017
  Direction = (0,-1,2e-16)
  Length = 18
  Length2 = 10
  Midplane = true
  Placement = pos=(0,0,0) rot=(1,0,0;1.5708rad)
  Profile = -> Sketch030
  ReferenceAxis = -> Sketch030 [N_Axis]
  Type = 0
FEATURE [Sketcher::SketchObject] Sketch031
  FullyConstrained = true
  MapMode = 5
  Placement = pos=(0,0,0) rot=(1,0,0;1.5708rad)
  Support = -> [XZ_Plane015]
  sketch-geometry (4):
    g0: LineSegment StartX=-60.5 StartY=4.5 StartZ=0 EndX=-52 EndY=4.5 EndZ=0
    g1: LineSegment StartX=-52 StartY=4.5 StartZ=0 EndX=-52 EndY=-15.5 EndZ=0
    g2: LineSegment StartX=-52 StartY=-15.5 StartZ=0 EndX=-60.5 EndY=-15.5 EndZ=0
    g3: LineSegment StartX=-60.5 StartY=-15.5 StartZ=0 EndX=-60.5 EndY=4.5 EndZ=0
  constraints (12):
    c: Coincident(g0,g1)
    c: Coincident(g1,g2)
    c: Coincident(g2,g3)
    c: Coincident(g3,g0)
    c: Horizontal(g0)
    c: Horizontal(g2)
    c: Vertical(g1)
    c: Vertical(g3)
    c: Distance(g1) = 20
    c: DistanceY(g1) = -15.5
    c: Distance(g2) = 8.5
    c: DistanceX(g1) = -52
FEATURE [PartDesign::Pad] Pad018
  BaseFeature = -> Pad017
  Direction = (0,-1,2e-16)
  Length = 7
  Length2 = 10
  Midplane = true
  Placement = pos=(0,0,0) rot=(1,0,0;1.5708rad)
  Profile = -> Sketch031
  ReferenceAxis = -> Sketch031 [N_Axis]
  Type = 0
FEATURE [Sketcher::SketchObject] Sketch032
  FullyConstrained = true
  MapMode = 5
  Placement = pos=(0,0,0) rot=(1,0,0;1.5708rad)
  Support = -> [XZ_Plane015]
  sketch-geometry (6):
    g0: LineSegment StartX=-52 StartY=14.5 StartZ=0 EndX=-57 EndY=14.5 EndZ=0
    g1: LineSegment StartX=-57 StartY=14.5 StartZ=0 EndX=-57 EndY=3.62414 EndZ=0
    g2: LineSegment StartX=-57 StartY=-25.5 StartZ=0 EndX=-52 EndY=-25.5 EndZ=0
    g3: LineSegment StartX=-52 StartY=-25.5 StartZ=0 EndX=-52 EndY=14.5 EndZ=0
    g4: ArcOfCircle CenterX=-84 CenterY=-5.5 CenterZ=0 NormalX=0 NormalY=0 NormalZ=1 AngleXU=0 Radius=28.5 StartAngle=5.9573 EndAngle=6.60907
    g5: LineSegment StartX=-57 StartY=-14.6241 StartZ=0 EndX=-57 EndY=-25.5 EndZ=0
  constraints (19):
    c: Coincident(g0,g1)
    c: Coincident(g5,g2)
    c: Coincident(g2,g3)
    c: Coincident(g3,g0)
    c: Horizontal(g0)
    c: Horizontal(g2)
    c: Vertical(g1)
    c: Vertical(g3)
    c: Distance(g2) = 5
    c: Distance(g3) = 40
    c: DistanceY(g2) = -25.5
    c: DistanceX(g2) = -52
    c: DistanceX(g4) = -84
    c: DistanceY(g4) = -5.5
    c: Diameter(g4) = 57
    c: Coincident(g1,g4)
    c: Coincident(g5,g4)
    c: Equal(g2,g0)
    c: Vertical(g5)
FEATURE [PartDesign::Pad] Pad019
  BaseFeature = -> Pad018
  Direction = (0,-1,2e-16)
  Length = 14
  Length2 = 10
  Midplane = true
  Placement = pos=(0,0,0) rot=(1,0,0;1.5708rad)
  Profile = -> Sketch032
  ReferenceAxis = -> Sketch032 [N_Axis]
  Type = 0
FEATURE [Sketcher::SketchObject] Sketch033
  AttachmentOffset = pos=(0,0,-57) rot=(0,0,1;0rad)
  FullyConstrained = true
  MapMode = 5
  Placement = pos=(-57,1.27e-14,-1.27e-14) rot=(0.57735,0.57735,0.57735;2.0944rad)
  Support = -> [YZ_Plane017]
  sketch-geometry (2):
    g0: Circle CenterX=0 CenterY=9 CenterZ=0 NormalX=0 NormalY=0 NormalZ=1 AngleXU=0 Radius=2.75
    g1: Circle CenterX=0 CenterY=-20 CenterZ=0 NormalX=0 NormalY=0 NormalZ=1 AngleXU=0 Radius=2.75
  constraints (6):
    c: Vertical(g1,g0)
    c: DistanceY(g1) = -20
    c: Distance(g1,g0) = 29
    c: Diameter(g0) = 5.5
    c: Equal(g0,g1)
    c: PointOnObject(g1,g-2)
FEATURE [PartDesign::Pocket] Pocket013
  BaseFeature = -> Pad019
  Direction = (-1,2e-16,-3e-16)
  Length = 5
  Length2 = 5
  Placement = pos=(0,0,0) rot=(1,0,0;1.5708rad)
  Profile = -> Sketch033
  ReferenceAxis = -> Sketch033 [N_Axis]
  Reversed = true
  Type = 1
FEATURE [PartDesign::Chamfer] Chamfer014
  Angle = 45
  Base = -> Pocket013 [Face17,Face16,Face15,Face19,Face2]
  BaseFeature = -> Pocket013
  ChamferType = 0
  FlipDirection = false
  Placement = pos=(0,0,0) rot=(1,0,0;1.5708rad)
  Size = 1
  Size2 = 1
  SupportTransform = false
  UseAllEdges = false
FEATURE [PartDesign::Body] Body001008  label="Roll_Motor_Rear_Mount"
  Group = -> [Sketch030,Pad017,Sketch031,Pad018,Sketch032,Pad019,Sketch033,Pocket013,Chamfer014]
  Origin = -> Origin015
  Placement = pos=(0,55,0) rot=(0,0,1;0rad)
  Tip = -> Chamfer014
FEATURE [Mesh::Feature] Pitch_Encoder_Pulley_5_15_32t_v4  label="Pitch_Encoder_Pulley_5_15_32t v4"
  Placement = pos=(42,0,-14.75) rot=(0,0,1;0rad)
FEATURE [Sketcher::SketchObject] Sketch046
  AttachmentOffset = pos=(0,0,69) rot=(0,0,1;0rad)
  FullyConstrained = true
  MapMode = 5
  Placement = pos=(69,-1.53e-14,1.53e-14) rot=(0.57735,0.57735,0.57735;2.0944rad)
  Support = -> [YZ_Plane015]
  sketch-geometry (8):
    g0: Circle CenterX=-10 CenterY=-6 CenterZ=0 NormalX=0 NormalY=0 NormalZ=1 AngleXU=0 Radius=26.5
    g1: Circle CenterX=-10 CenterY=-6 CenterZ=0 NormalX=0 NormalY=0 NormalZ=1 AngleXU=0 Radius=8.5
    g2: Circle CenterX=-10 CenterY=9 CenterZ=0 NormalX=0 NormalY=0 NormalZ=1 AngleXU=0 Radius=1.65
    g3: Circle CenterX=2.99038 CenterY=-13.5 CenterZ=0 NormalX=0 NormalY=0 NormalZ=1 AngleXU=0 Radius=1.65
    g4: Circle CenterX=-22.9904 CenterY=-13.5 CenterZ=0 NormalX=0 NormalY=0 NormalZ=1 AngleXU=0 Radius=1.65
    g5: LineSegment StartX=-10 StartY=9 StartZ=0 EndX=2.99038 EndY=-13.5 EndZ=0
    g6: LineSegment StartX=2.99038 StartY=-13.5 StartZ=0 EndX=-22.9904 EndY=-13.5 EndZ=0
    g7: LineSegment StartX=-22.9904 StartY=-13.5 StartZ=0 EndX=-10 EndY=9 EndZ=0
  constraints (20):
    c: DistanceY(g0) = -6
    c: DistanceX(g0) = -10
    c: Diameter(g0) = 53
    c: Coincident(g1,g0)
    c: Diameter(g1) = 17
    c: Equal(g2,g3)
    c: Equal(g2,g4)
    c: Diameter(g2) = 3.3
    c: Vertical(g0,g2)
    c: Distance(g0,g2) = 15
    c: Coincident(g5,g2)
    c: Coincident(g5,g3)
    c: Coincident(g5,g6)
    c: Coincident(g6,g4)
    c: Coincident(g6,g7)
    c: Coincident(g7,g5)
    c: Equal(g7,g5)
    c: Equal(g5,g6)
    c: Distance(g0,g3) = 15
    c: Distance(g0,g4) = 15
FEATURE [PartDesign::Pad] Pad029
  Direction = (1,-2e-16,3e-16)
  Length = 8
  Length2 = 10
  Placement = pos=(0,0,0) rot=(0.57735,0.57735,0.57735;2.0944rad)
  Profile = -> Sketch046
  ReferenceAxis = -> Sketch046 [N_Axis]
  Type = 0
FEATURE [Sketcher::SketchObject] Sketch048
  AttachmentOffset = pos=(0,0,69) rot=(0,0,1;0rad)
  FullyConstrained = true
  MapMode = 5
  Placement = pos=(69,-1.53e-14,1.53e-14) rot=(0.57735,0.57735,0.57735;2.0944rad)
  Support = -> [YZ_Plane015]
  sketch-geometry (1):
    g0: Circle CenterX=-10 CenterY=-6 CenterZ=0 NormalX=0 NormalY=0 NormalZ=1 AngleXU=0 Radius=10.5
  constraints (3):
    c: DistanceY(g0) = -6
    c: DistanceX(g0) = -10
    c: Diameter(g0) = 21
FEATURE [PartDesign::Pocket] Pocket014
  BaseFeature = -> Pad029
  Direction = (-1,2e-16,-3e-16)
  Length = 6
  Length2 = 5
  Placement = pos=(0,0,0) rot=(0.57735,0.57735,0.57735;2.0944rad)
  Profile = -> Sketch048
  ReferenceAxis = -> Sketch048 [N_Axis]
  Reversed = true
  Type = 0
FEATURE [Sketcher::SketchObject] Sketch064
  AttachmentOffset = pos=(0,0,69) rot=(0,0,1;0rad)
  FullyConstrained = true
  MapMode = 5
  Placement = pos=(69,-1.53e-14,1.53e-14) rot=(0.57735,0.57735,0.57735;2.0944rad)
  Support = -> [YZ_Plane015]
  sketch-geometry (8):
    g0: Circle CenterX=-10 CenterY=-6 CenterZ=0 NormalX=0 NormalY=0 NormalZ=1 AngleXU=0 Radius=22
    g1: LineSegment StartX=-10 StartY=-6 StartZ=0 EndX=-31.6506 EndY=6.5 EndZ=0
    g2: LineSegment StartX=-10 StartY=-6 StartZ=0 EndX=-10 EndY=19 EndZ=0
    g3: LineSegment StartX=-10 StartY=-6 StartZ=0 EndX=11.6506 EndY=6.5 EndZ=0
    g4: LineSegment StartX=-10 StartY=-6 StartZ=0 EndX=-10 EndY=-31 EndZ=0
    g5: Circle CenterX=-29.0526 CenterY=5 CenterZ=0 NormalX=0 NormalY=0 NormalZ=1 AngleXU=0 Radius=1.65
    g6: Circle CenterX=9.05256 CenterY=5 CenterZ=0 NormalX=0 NormalY=0 NormalZ=1 AngleXU=0 Radius=1.65
    g7: Circle CenterX=-10 CenterY=-28 CenterZ=0 NormalX=0 NormalY=0 NormalZ=1 AngleXU=0 Radius=1.65
  constraints (24):
    c: DistanceX(g0) = -10
    c: DistanceY(g0) = -6
    c: Coincident(g1,g0)
    c: Coincident(g2,g0)
    c: Vertical(g2)
    c: Distance(g2) = 25
    c: Distance(g1) = 25
    c: Angle(g2,g1) = 1.0472
    c: Diameter(g0) = 44
    c: Coincident(g3,g0)
    c: Coincident(g4,g0)
    c: Vertical(g4)
    c: Distance(g4) = 25
    c: Distance(g3) = 25
    c: Angle(g3,g1) = 2.0944
    c: PointOnObject(g7,g4)
    c: PointOnObject(g7,g0)
    c: PointOnObject(g5,g0)
    c: PointOnObject(g5,g1)
    c: PointOnObject(g6,g3)
    c: PointOnObject(g6,g0)
    c: Diameter(g5) = 3.3
    c: Equal(g5,g6)
    c: Equal(g6,g7)
FEATURE [PartDesign::Hole] Hole003
  BaseFeature = -> Pocket014
  CustomThreadClearance = 0
  Depth = 155.107
  DepthType = 1
  Diameter = 3.4
  DrillForDepth = false
  DrillPoint = 1
  DrillPointAngle = 118
  HoleCutCountersinkAngle = 90
  HoleCutCustomValues = false
  HoleCutDepth = 4
  HoleCutDiameter = 5.5
  HoleCutType = 1
  ModelThread = false
  Placement = pos=(0,0,0) rot=(0.57735,0.57735,0.57735;2.0944rad)
  Profile = -> Sketch064
  Reversed = true
  Tapered = false
  TaperedAngle = 90
  ThreadClass = 0
  ThreadDepth = 155.107
  ThreadDepthType = 0
  ThreadDirection = 0
  ThreadFit = 0
  ThreadSize = 9
  ThreadType = 1
  Threaded = false
  UseCustomThreadClearance = false
FEATURE [Sketcher::SketchObject] Sketch065
  AttachmentOffset = pos=(0,0,77) rot=(0,0,1;0rad)
  FullyConstrained = true
  MapMode = 5
  Placement = pos=(77,-1.71e-14,1.71e-14) rot=(0.57735,0.57735,0.57735;2.0944rad)
  Support = -> [YZ_Plane015]
  sketch-geometry (7):
    g0: Circle CenterX=-10 CenterY=-6 CenterZ=0 NormalX=0 NormalY=0 NormalZ=1 AngleXU=0 Radius=15
    g1: LineSegment StartX=-10 StartY=-6 StartZ=0 EndX=-10 EndY=9 EndZ=0
    g2: LineSegment StartX=-10 StartY=-6 StartZ=0 EndX=-22.9904 EndY=-13.5 EndZ=0
    g3: LineSegment StartX=-10 StartY=-6 StartZ=0 EndX=2.99038 EndY=-13.5 EndZ=0
    g4: Circle CenterX=-22.9904 CenterY=-13.5 CenterZ=0 NormalX=0 NormalY=0 NormalZ=1 AngleXU=0 Radius=1.6
    g5: Circle CenterX=-10 CenterY=9 CenterZ=0 NormalX=0 NormalY=0 NormalZ=1 AngleXU=0 Radius=1.6
    g6: Circle CenterX=2.99038 CenterY=-13.5 CenterZ=0 NormalX=0 NormalY=0 NormalZ=1 AngleXU=0 Radius=1.6
  constraints (18):
    c: DistanceX(g0) = -10
    c: DistanceY(g0) = -6
    c: Diameter(g0) = 30
    c: Coincident(g1,g0)
    c: PointOnObject(g1,g0)
    c: Vertical(g1)
    c: Coincident(g2,g1)
    c: PointOnObject(g2,g0)
    c: Coincident(g3,g1)
    c: PointOnObject(g3,g0)
    c: Angle(g3,g1) = 2.0944
    c: Angle(g1,g2) = 2.0944
    c: Coincident(g4,g2)
    c: Coincident(g5,g1)
    c: Coincident(g6,g3)
    c: Diameter(g4) = 3.2
    c: Equal(g4,g5)
    c: Equal(g5,g6)
FEATURE [PartDesign::Hole] Hole004
  BaseFeature = -> Hole003
  CustomThreadClearance = 0
  Depth = 154.845
  DepthType = 1
  Diameter = 3.4
  DrillForDepth = false
  DrillPoint = 1
  DrillPointAngle = 118
  HoleCutCountersinkAngle = 90
  HoleCutCustomValues = false
  HoleCutDepth = 4
  HoleCutDiameter = 5.5
  HoleCutType = 1
  ModelThread = false
  Placement = pos=(0,0,0) rot=(0.57735,0.57735,0.57735;2.0944rad)
  Profile = -> Sketch065
  Tapered = false
  TaperedAngle = 90
  ThreadClass = 0
  ThreadDepth = 154.845
  ThreadDepthType = 0
  ThreadDirection = 0
  ThreadFit = 0
  ThreadSize = 9
  ThreadType = 1
  Threaded = false
  UseCustomThreadClearance = false
FEATURE [PartDesign::Chamfer] Chamfer016
  Angle = 45
  Base = -> Hole004 [Edge3]
  BaseFeature = -> Hole004
  ChamferType = 0
  FlipDirection = false
  Placement = pos=(0,0,0) rot=(0.57735,0.57735,0.57735;2.0944rad)
  Size = 0.75
  Size2 = 1
  SupportTransform = false
  UseAllEdges = false
FEATURE [PartDesign::Body] Body011  label="Pitch Encoder Spacer"
  Group = -> [Sketch046,Pad029,Sketch048,Pocket014,Sketch064,Hole003,Sketch065,Hole004,Chamfer016]
  Origin = -> Origin021
  Placement = pos=(2,-5.5,6.5) rot=(0,0,1;0rad)
  Tip = -> Chamfer016
FEATURE [App::Part] Part002  label="Pitch_Encoder_Spacer"
  Group = -> [Body011]
  Origin = -> Origin022
  Placement = pos=(149.75,-23.5,-1.75) rot=(0,1,0;3.14159rad)
FEATURE [Sketcher::SketchObject] Sketch049
  AttachmentOffset = pos=(0,0,81) rot=(0,0,1;0rad)
  FullyConstrained = true
  MapMode = 5
  Placement = pos=(81,-1.8e-14,1.8e-14) rot=(0.57735,0.57735,0.57735;2.0944rad)
  Support = -> [YZ_Plane022]
  sketch-geometry (6):
    g0: ArcOfCircle CenterX=-10 CenterY=-10 CenterZ=0 NormalX=0 NormalY=0 NormalZ=1 AngleXU=0 Radius=27 StartAngle=5.132 EndAngle=9.26269
    g1: LineSegment StartX=-43 StartY=-58.5 StartZ=0 EndX=1 EndY=-58.5 EndZ=0
    g2: LineSegment StartX=1 StartY=-58.5 StartZ=0 EndX=1 EndY=-34.6577 EndZ=0
    g3: LineSegment StartX=-43 StartY=-58.5 StartZ=0 EndX=-43 EndY=-44.5 EndZ=0
    g4: LineSegment StartX=-43 StartY=-44.5 StartZ=0 EndX=-36.6461 EndY=-5.64285 EndZ=0
    g5: Circle CenterX=-10 CenterY=-10 CenterZ=0 NormalX=0 NormalY=0 NormalZ=1 AngleXU=0 Radius=17
  constraints (17):
    c: DistanceX(g0) = -10
    c: DistanceY(g0) = -10
    c: Diameter(g0) = 54
    c: Horizontal(g1)
    c: Coincident(g2,g1)
    c: Vertical(g2)
    c: Vertical(g3)
    c: Distance(g3) = 14
    c: Coincident(g3,g1)
    c: Coincident(g4,g3)
    c: Tangent(g0,g4) = 1.5708
    c: DistanceX(g1) = -43
    c: DistanceY(g1) = -58.5
    c: Coincident(g5,g0)
    c: Diameter(g5) = 34
    c: Distance(g1) = 44
    c: Coincident(g0,g2)
FEATURE [PartDesign::Pad] Pad030
  Direction = (1,-2e-16,3e-16)
  Length = 10
  Length2 = 10
  Placement = pos=(0,0,0) rot=(0.57735,0.57735,0.57735;2.0944rad)
  Profile = -> Sketch049
  ReferenceAxis = -> Sketch049 [N_Axis]
  Type = 0
FEATURE [Sketcher::SketchObject] Sketch053
  AttachmentOffset = pos=(0,0,91) rot=(0,0,1;0rad)
  FullyConstrained = true
  MapMode = 5
  Placement = pos=(91,-2.02e-14,2.02e-14) rot=(0.57735,0.57735,0.57735;2.0944rad)
  Support = -> [YZ_Plane019]
  sketch-geometry (7):
    g0: ArcOfCircle CenterX=-10 CenterY=-10 CenterZ=0 NormalX=0 NormalY=0 NormalZ=1 AngleXU=0 Radius=27 StartAngle=0.506238 EndAngle=2.97951
    g1: LineSegment StartX=-43 StartY=-58.5 StartZ=0 EndX=40 EndY=-58.5 EndZ=0
    g2: LineSegment StartX=40 StartY=-58.5 StartZ=0 EndX=40 EndY=-44.5 EndZ=0
    g3: LineSegment StartX=40 StartY=-44.5 StartZ=0 EndX=13.6135 EndY=3.09205 EndZ=0
    g4: Circle CenterX=-10 CenterY=-10 CenterZ=0 NormalX=0 NormalY=0 NormalZ=1 AngleXU=0 Radius=17
    g5: LineSegment StartX=-43 StartY=-58.5 StartZ=0 EndX=-43 EndY=-44.5 EndZ=0
    g6: LineSegment StartX=-43 StartY=-44.5 StartZ=0 EndX=-36.6461 EndY=-5.64285 EndZ=0
  constraints (19):
    c: DistanceX(g0) = -10
    c: DistanceY(g0) = -10
    c: Horizontal(g1)
    c: DistanceY(g1) = -58.5
    c: Diameter(g0) = 54
    c: Coincident(g2,g1)
    c: Vertical(g2)
    c: DistanceY(g2,g2) = 14
    c: Coincident(g3,g2)
    c: Tangent(g0,g3) = -1.5708
    c: Coincident(g4,g0)
    c: Diameter(g4) = 34
    c: DistanceX(g1) = 40
    c: DistanceX(g1) = -43
    c: Coincident(g5,g1)
    c: Vertical(g5)
    c: Equal(g5,g2)
    c: Coincident(g6,g5)
    c: Tangent(g0,g6) = 1.5708
FEATURE [PartDesign::Pad] Pad033
  Direction = (1,-2e-16,3e-16)
  Length = 10
  Length2 = 10
  Placement = pos=(0,0,0) rot=(0.57735,0.57735,0.57735;2.0944rad)
  Profile = -> Sketch053
  ReferenceAxis = -> Sketch053 [N_Axis]
  Type = 0
FEATURE [Sketcher::SketchObject] Sketch057
  AttachmentOffset = pos=(0,0,91) rot=(0,0,1;0rad)
  FullyConstrained = true
  MapMode = 5
  Placement = pos=(91,-2.02e-14,2.02e-14) rot=(0.57735,0.57735,0.57735;2.0944rad)
  Support = -> [YZ_Plane019]
  sketch-geometry (1):
    g0: Circle CenterX=-10 CenterY=-10 CenterZ=0 NormalX=0 NormalY=0 NormalZ=1 AngleXU=0 Radius=18.575
  constraints (3):
    c: Diameter(g0) = 37.15
    c: DistanceY(g0) = -10
    c: DistanceX(g0) = -10
FEATURE [PartDesign::Pocket] Pocket018
  BaseFeature = -> Pad033
  Direction = (-1,2e-16,-3e-16)
  Length = 7
  Length2 = 5
  Placement = pos=(0,0,0) rot=(0.57735,0.57735,0.57735;2.0944rad)
  Profile = -> Sketch057
  ReferenceAxis = -> Sketch057 [N_Axis]
  Reversed = true
  Type = 0
FEATURE [Sketcher::SketchObject] Sketch066
  AttachmentOffset = pos=(0,0,91) rot=(0,0,1;0rad)
  FullyConstrained = true
  MapMode = 5
  Placement = pos=(91,-2.02e-14,2.02e-14) rot=(0.57735,0.57735,0.57735;2.0944rad)
  Support = -> [YZ_Plane022]
  sketch-geometry (1):
    g0: Circle CenterX=-10 CenterY=-10 CenterZ=0 NormalX=0 NormalY=0 NormalZ=1 AngleXU=0 Radius=18.575
  constraints (3):
    c: DistanceY(g0) = -10
    c: DistanceX(g0) = -10
    c: Diameter(g0) = 37.15
FEATURE [PartDesign::Pocket] Pocket019
  BaseFeature = -> Pad030
  Direction = (-1,2e-16,-3e-16)
  Length = 7
  Length2 = 5
  Placement = pos=(0,0,0) rot=(0.57735,0.57735,0.57735;2.0944rad)
  Profile = -> Sketch066
  ReferenceAxis = -> Sketch066 [N_Axis]
  Type = 0
FEATURE [Sketcher::SketchObject] Sketch058
  AttachmentOffset = pos=(0,0,-58.5) rot=(0,0,1;0rad)
  FullyConstrained = true
  MapMode = 5
  Placement = pos=(0,0,-58.5) rot=(0,0,1;0rad)
  Support = -> [XY_Plane019]
  sketch-geometry (6):
    g0: LineSegment StartX=91 StartY=40 StartZ=0 EndX=71 EndY=40 EndZ=0
    g1: LineSegment StartX=71 StartY=40 StartZ=0 EndX=71 EndY=1 EndZ=0
    g2: LineSegment StartX=71 StartY=1 StartZ=0 EndX=66.5 EndY=1 EndZ=0
    g3: LineSegment StartX=66.5 StartY=1 StartZ=0 EndX=66.5 EndY=-43 EndZ=0
    g4: LineSegment StartX=66.5 StartY=-43 StartZ=0 EndX=91 EndY=-43 EndZ=0
    g5: LineSegment StartX=91 StartY=-43 StartZ=0 EndX=91 EndY=40 EndZ=0
  constraints (18):
    c: Coincident(g0,g1)
    c: Vertical(g1)
    c: Coincident(g1,g2)
    c: Horizontal(g2)
    c: Coincident(g2,g3)
    c: Vertical(g3)
    c: Coincident(g3,g4)
    c: Horizontal(g4)
    c: Coincident(g4,g5)
    c: Coincident(g5,g0)
    c: Vertical(g5)
    c: Horizontal(g0)
    c: Distance(g0) = 20
    c: DistanceY(g0) = 40
    c: DistanceX(g0) = 91
    c: Distance(g5) = 83
    c: Distance(g4) = 24.5
    c: DistanceY(g3,g3) = 44
FEATURE [PartDesign::Pad] Pad034
  BaseFeature = -> Pocket018
  Direction = (0,0,1)
  Length = 14
  Length2 = 10
  Placement = pos=(0,0,0) rot=(0.57735,0.57735,0.57735;2.0944rad)
  Profile = -> Sketch058
  ReferenceAxis = -> Sketch058 [N_Axis]
  Type = 0
FEATURE [Sketcher::SketchObject] Sketch067
  AttachmentOffset = pos=(0,0,81) rot=(0,0,1;0rad)
  FullyConstrained = true
  MapMode = 5
  Placement = pos=(81,-1.8e-14,1.8e-14) rot=(0.57735,0.57735,0.57735;2.0944rad)
  Support = -> [YZ_Plane022]
  sketch-geometry (2):
    g0: Circle CenterX=-34 CenterY=-51.5 CenterZ=0 NormalX=0 NormalY=0 NormalZ=1 AngleXU=0 Radius=2.65
    g1: Circle CenterX=-8 CenterY=-51.5 CenterZ=0 NormalX=0 NormalY=0 NormalZ=1 AngleXU=0 Radius=2.65
  constraints (6):
    c: Diameter(g0) = 5.3
    c: Distance(g0,g1) = 26
    c: DistanceY(g1) = -51.5
    c: DistanceX(g1) = -8
    c: Equal(g0,g1)
    c: Horizontal(g0,g1)
FEATURE [PartDesign::Hole] Hole005
  BaseFeature = -> Pocket019
  CustomThreadClearance = 0
  Depth = 25
  DepthType = 0
  Diameter = 5.3
  DrillForDepth = false
  DrillPoint = 1
  DrillPointAngle = 118
  HoleCutCountersinkAngle = 90
  HoleCutCustomValues = false
  HoleCutDepth = 5.4
  HoleCutDiameter = 8.7
  HoleCutType = 1
  ModelThread = false
  Placement = pos=(0,0,0) rot=(0.57735,0.57735,0.57735;2.0944rad)
  Profile = -> Sketch067
  Reversed = true
  Tapered = false
  TaperedAngle = 90
  ThreadClass = 0
  ThreadDepth = 25
  ThreadDepthType = 0
  ThreadDirection = 0
  ThreadFit = 1
  ThreadSize = 13
  ThreadType = 1
  Threaded = false
  UseCustomThreadClearance = false
FEATURE [Sketcher::SketchObject] Sketch059
  AttachmentOffset = pos=(-15,-23,66.5) rot=(0,0,1;0rad)
  FullyConstrained = true
  MapMode = 5
  Placement = pos=(66.5,-15,-23) rot=(0.57735,0.57735,0.57735;2.0944rad)
  Support = -> [YZ_Plane019]
  sketch-geometry (2):
    g0: Circle CenterX=-19 CenterY=-28.5 CenterZ=0 NormalX=0 NormalY=0 NormalZ=1 AngleXU=0 Radius=3.45
    g1: Circle CenterX=7 CenterY=-28.5 CenterZ=0 NormalX=0 NormalY=0 NormalZ=1 AngleXU=0 Radius=3.45
  constraints (6):
    c: Diameter(g0) = 6.9
    c: DistanceX(g1) = 7
    c: DistanceY(g1) = -28.5
    c: Horizontal(g0,g1)
    c: Distance(g0,g1) = 26
    c: Equal(g0,g1)
FEATURE [PartDesign::Pocket] Pocket020
  BaseFeature = -> Pad034
  Direction = (-1,2e-16,-3e-16)
  Length = 12
  Length2 = 5
  Placement = pos=(0,0,0) rot=(0.57735,0.57735,0.57735;2.0944rad)
  Profile = -> Sketch059
  ReferenceAxis = -> Sketch059 [N_Axis]
  Reversed = true
  Type = 0
FEATURE [Sketcher::SketchObject] Sketch060
  AttachmentOffset = pos=(1,0,-44.5) rot=(0,0,1;0rad)
  FullyConstrained = true
  MapMode = 5
  Placement = pos=(1,0,-44.5) rot=(0,0,1;0rad)
  Support = -> [XY_Plane019]
  sketch-geometry (3):
    g0: Circle CenterX=85 CenterY=18 CenterZ=0 NormalX=0 NormalY=0 NormalZ=1 AngleXU=0 Radius=4.35
    g1: Circle CenterX=72 CenterY=-21 CenterZ=0 NormalX=0 NormalY=0 NormalZ=1 AngleXU=0 Radius=4.35
    g2: Circle CenterX=85 CenterY=-34 CenterZ=0 NormalX=0 NormalY=0 NormalZ=1 AngleXU=0 Radius=4.35
  constraints (9):
    c: Equal(g0,g1)
    c: Equal(g1,g2)
    c: Diameter(g0) = 8.7
    c: Vertical(g0,g2)
    c: DistanceX(g0) = 85
    c: DistanceY(g0) = 18
    c: DistanceX(g1) = 72
    c: DistanceY(g1) = -21
    c: Distance(g0,g2) = 52
FEATURE [PartDesign::Hole] Hole001
  BaseFeature = -> Pocket020
  CustomThreadClearance = 0
  Depth = 237.1
  DepthType = 1
  Diameter = 5.3
  DrillForDepth = false
  DrillPoint = 1
  DrillPointAngle = 118
  HoleCutCountersinkAngle = 90
  HoleCutCustomValues = false
  HoleCutDepth = 5.4
  HoleCutDiameter = 8.7
  HoleCutType = 1
  ModelThread = false
  Placement = pos=(0,0,0) rot=(0.57735,0.57735,0.57735;2.0944rad)
  Profile = -> Sketch060
  Tapered = false
  TaperedAngle = 90
  ThreadClass = 0
  ThreadDepth = 237.1
  ThreadDepthType = 0
  ThreadDirection = 0
  ThreadFit = 1
  ThreadSize = 13
  ThreadType = 1
  Threaded = false
  UseCustomThreadClearance = false
FEATURE [Sketcher::SketchObject] Sketch061
  AttachmentOffset = pos=(0,0,81) rot=(0,0,1;0rad)
  FullyConstrained = true
  MapMode = 5
  Placement = pos=(81,-1.8e-14,1.8e-14) rot=(0.57735,0.57735,0.57735;2.0944rad)
  Support = -> [YZ_Plane022]
  sketch-geometry (6):
    g0: LineSegment StartX=-10 StartY=-10 StartZ=0 EndX=-29.0526 EndY=1 EndZ=0
    g1: LineSegment StartX=-10 StartY=-10 StartZ=0 EndX=9.05256 EndY=1 EndZ=0
    g2: LineSegment StartX=-10 StartY=-10 StartZ=0 EndX=-10 EndY=-32 EndZ=0
    g3: Circle CenterX=-29.0526 CenterY=1 CenterZ=0 NormalX=0 NormalY=0 NormalZ=1 AngleXU=0 Radius=2.2
    g4: Circle CenterX=9.05256 CenterY=1 CenterZ=0 NormalX=0 NormalY=0 NormalZ=1 AngleXU=0 Radius=2.2
    g5: Circle CenterX=-10 CenterY=-32 CenterZ=0 NormalX=0 NormalY=0 NormalZ=1 AngleXU=0 Radius=2.2
  constraints (16):
    c: DistanceY(g0) = -10
    c: DistanceX(g0) = -10
    c: Coincident(g1,g0)
    c: Coincident(g2,g0)
    c: Vertical(g2)
    c: Equal(g0,g1)
    c: Equal(g1,g2)
    c: Distance(g0) = 22
    c: Angle(g0,g2) = 2.0944
    c: Angle(g2,g1) = 2.0944
    c: Coincident(g3,g0)
    c: Coincident(g4,g1)
    c: Coincident(g5,g2)
    c: Equal(g3,g4)
    c: Equal(g3,g5)
    c: Diameter(g3) = 4.4
FEATURE [PartDesign::Pocket] Pocket021
  BaseFeature = -> Hole005
  Direction = (-1,2e-16,-3e-16)
  Length = 5
  Length2 = 5
  Placement = pos=(0,0,0) rot=(0.57735,0.57735,0.57735;2.0944rad)
  Profile = -> Sketch061
  ReferenceAxis = -> Sketch061 [N_Axis]
  Reversed = true
  Type = 1
FEATURE [PartDesign::Body] Body012  label="Pitch Encoder Mount"
  Group = -> [Sketch049,Pad030,Sketch066,Pocket019,Sketch067,Hole005,Sketch061,Pocket021]
  Origin = -> Origin017
  Placement = pos=(-6,0,0) rot=(0,0,1;0rad)
  Tip = -> Pocket021
FEATURE [Sketcher::SketchObject] Sketch069
  AttachmentOffset = pos=(0,0,-45) rot=(0,0,1;0rad)
  FullyConstrained = true
  MapMode = 5
  Placement = pos=(0,0,-45) rot=(0,0,1;0rad)
  Support = -> [XY_Plane]
  sketch-geometry (4):
    g0: Circle CenterX=88.5 CenterY=62.5 CenterZ=0 NormalX=0 NormalY=0 NormalZ=1 AngleXU=0 Radius=2.2
    g1: Circle CenterX=109.5 CenterY=37.5 CenterZ=0 NormalX=0 NormalY=0 NormalZ=1 AngleXU=0 Radius=2.2
    g2: Circle CenterX=109.5 CenterY=62.5 CenterZ=0 NormalX=0 NormalY=0 NormalZ=1 AngleXU=0 Radius=2.2
    g3: Circle CenterX=88.5 CenterY=37.5 CenterZ=0 NormalX=0 NormalY=0 NormalZ=1 AngleXU=0 Radius=2.2
  constraints (12):
    c: Vertical(g3,g0)
    c: Vertical(g1,g2)
    c: Horizontal(g3,g1)
    c: Horizontal(g0,g2)
    c: Distance(g3,g1) = 21
    c: Distance(g3,g0) = 25
    c: Diameter(g3) = 4.4
    c: Equal(g3,g0)
    c: Equal(g0,g2)
    c: Equal(g2,g1)
    c: DistanceY(g3) = 37.5
    c: DistanceX(g3) = 88.5
FEATURE [PartDesign::Hole] Hole006
  BaseFeature = -> Hole
  CustomThreadClearance = 0
  Depth = 208.716
  DepthType = 1
  Diameter = 4.5
  DrillForDepth = false
  DrillPoint = 1
  DrillPointAngle = 118
  HoleCutCountersinkAngle = 90
  HoleCutCustomValues = false
  HoleCutDepth = 0
  HoleCutDiameter = 10.1
  HoleCutType = 0
  ModelThread = false
  Placement = pos=(0,0,0) rot=(1,0,0;1.5708rad)
  Profile = -> Sketch069
  Reversed = true
  Tapered = false
  TaperedAngle = 90
  ThreadClass = 0
  ThreadDepth = 208.716
  ThreadDepthType = 0
  ThreadDirection = 0
  ThreadFit = 0
  ThreadSize = 11
  ThreadType = 1
  Threaded = false
  UseCustomThreadClearance = false
FEATURE [Sketcher::SketchObject] Sketch070
  AttachmentOffset = pos=(0,0,-39) rot=(0,0,1;0rad)
  FullyConstrained = true
  MapMode = 5
  Placement = pos=(0,0,-39) rot=(0,0,1;0rad)
  Support = -> [XY_Plane]
  sketch-geometry (28):
    g0: LineSegment StartX=92.1 StartY=64.5785 StartZ=0 EndX=88.5 EndY=66.6569 EndZ=0
    g1: LineSegment StartX=88.5 StartY=66.6569 StartZ=0 EndX=84.9 EndY=64.5785 EndZ=0
    g2: LineSegment StartX=84.9 StartY=64.5785 StartZ=0 EndX=84.9 EndY=60.4215 EndZ=0
    g3: LineSegment StartX=84.9 StartY=60.4215 StartZ=0 EndX=88.5 EndY=58.3431 EndZ=0
    g4: LineSegment StartX=88.5 StartY=58.3431 StartZ=0 EndX=92.1 EndY=60.4215 EndZ=0
    g5: LineSegment StartX=92.1 StartY=60.4215 StartZ=0 EndX=92.1 EndY=64.5785 EndZ=0
    g6: Circle CenterX=88.5 CenterY=62.5 CenterZ=0 NormalX=0 NormalY=0 NormalZ=1 AngleXU=0 Radius=4.15692
    g7: LineSegment StartX=113.1 StartY=64.5785 StartZ=0 EndX=109.5 EndY=66.6569 EndZ=0
    g8: LineSegment StartX=109.5 StartY=66.6569 StartZ=0 EndX=105.9 EndY=64.5785 EndZ=0
    g9: LineSegment StartX=105.9 StartY=64.5785 StartZ=0 EndX=105.9 EndY=60.4215 EndZ=0
    g10: LineSegment StartX=105.9 StartY=60.4215 StartZ=0 EndX=109.5 EndY=58.3431 EndZ=0
    g11: LineSegment StartX=109.5 StartY=58.3431 StartZ=0 EndX=113.1 EndY=60.4215 EndZ=0
    g12: LineSegment StartX=113.1 StartY=60.4215 StartZ=0 EndX=113.1 EndY=64.5785 EndZ=0
    g13: Circle CenterX=109.5 CenterY=62.5 CenterZ=0 NormalX=0 NormalY=0 NormalZ=1 AngleXU=0 Radius=4.15692
    g14: LineSegment StartX=113.1 StartY=39.5785 StartZ=0 EndX=109.5 EndY=41.6569 EndZ=0
    g15: LineSegment StartX=109.5 StartY=41.6569 StartZ=0 EndX=105.9 EndY=39.5785 EndZ=0
    g16: LineSegment StartX=105.9 StartY=39.5785 StartZ=0 EndX=105.9 EndY=35.4215 EndZ=0
    g17: LineSegment StartX=105.9 StartY=35.4215 StartZ=0 EndX=109.5 EndY=33.3431 EndZ=0
    g18: LineSegment StartX=109.5 StartY=33.3431 StartZ=0 EndX=113.1 EndY=35.4215 EndZ=0
    g19: LineSegment StartX=113.1 StartY=35.4215 StartZ=0 EndX=113.1 EndY=39.5785 EndZ=0
    g20: Circle CenterX=109.5 CenterY=37.5 CenterZ=0 NormalX=0 NormalY=0 NormalZ=1 AngleXU=0 Radius=4.15692
    g21: LineSegment StartX=92.1 StartY=39.5785 StartZ=0 EndX=88.5 EndY=41.6569 EndZ=0
    g22: LineSegment StartX=88.5 StartY=41.6569 StartZ=0 EndX=84.9 EndY=39.5785 EndZ=0
    g23: LineSegment StartX=84.9 StartY=39.5785 StartZ=0 EndX=84.9 EndY=35.4215 EndZ=0
    g24: LineSegment StartX=84.9 StartY=35.4215 StartZ=0 EndX=88.5 EndY=33.3431 EndZ=0
    g25: LineSegment StartX=88.5 StartY=33.3431 StartZ=0 EndX=92.1 EndY=35.4215 EndZ=0
    g26: LineSegment StartX=92.1 StartY=35.4215 StartZ=0 EndX=92.1 EndY=39.5785 EndZ=0
    g27: Circle CenterX=88.5 CenterY=37.5 CenterZ=0 NormalX=0 NormalY=0 NormalZ=1 AngleXU=0 Radius=4.15692
  constraints (68):
    c: Coincident(g0,g1)
    c: Coincident(g1,g2)
    c: Coincident(g2,g3)
    c: Coincident(g3,g4)
    c: Coincident(g4,g5)
    c: Coincident(g5,g0)
    c: Equal(g0, g1-g5) x5
    c: PointOnObject(g0,g6)
    c: PointOnObject(g1,g6)
    c: PointOnObject(g2,g6)
    c: PointOnObject(g3,g6)
    c: PointOnObject(g4,g6)
    c: PointOnObject(g5,g6)
    c: Coincident(g7,g8)
    c: Coincident(g8,g9)
    c: Coincident(g9,g10)
    c: Coincident(g10,g11)
    c: Coincident(g11,g12)
    c: Coincident(g12,g7)
    c: Equal(g7, g8-g12) x5
    c: PointOnObject(g7,g13)
    c: PointOnObject(g8,g13)
    c: PointOnObject(g9,g13)
    c: PointOnObject(g10,g13)
    c: PointOnObject(g11,g13)
    c: PointOnObject(g12,g13)
    c: Coincident(g14,g15)
    c: Coincident(g15,g16)
    c: Coincident(g16,g17)
    c: Coincident(g17,g18)
    c: Coincident(g18,g19)
    c: Coincident(g19,g14)
    c: Equal(g14, g15-g19) x5
    c: PointOnObject(g14,g20)
    c: PointOnObject(g15,g20)
    c: PointOnObject(g16,g20)
    c: PointOnObject(g17,g20)
    c: PointOnObject(g18,g20)
    c: PointOnObject(g19,g20)
    c: Coincident(g21,g22)
    c: Coincident(g22,g23)
    c: Coincident(g23,g24)
    c: Coincident(g24,g25)
    c: Coincident(g25,g26)
    c: Coincident(g26,g21)
    c: Equal(g21, g22-g26) x5
    c: PointOnObject(g21,g27)
    c: PointOnObject(g22,g27)
    c: PointOnObject(g23,g27)
    c: PointOnObject(g24,g27)
    c: PointOnObject(g25,g27)
    c: PointOnObject(g26,g27)
    c: Horizontal(g27,g20)
    c: Vertical(g27,g6)
    c: Vertical(g20,g13)
    c: Horizontal(g6,g13)
    c: Distance(g27,g6) = 25
    c: Distance(g27,g20) = 21
    c: DistanceX(g27) = 88.5
    c: DistanceY(g27) = 37.5
    c: Distance(g1,g0) = 7.2
    c: Vertical(g2)
    c: Equal(g6,g13)
    c: Equal(g13,g20)
    c: Equal(g20,g27)
    c: Vertical(g12)
    c: Vertical(g19)
    c: Vertical(g23)
FEATURE [PartDesign::Pocket] Pocket022
  BaseFeature = -> Hole006
  Direction = (0,0,-1)
  Length = 4.5
  Length2 = 5
  Placement = pos=(0,0,0) rot=(1,0,0;1.5708rad)
  Profile = -> Sketch070
  ReferenceAxis = -> Sketch070 [N_Axis]
  Reversed = true
  Type = 0
FEATURE [Sketcher::SketchObject] Sketch071
  AttachmentOffset = pos=(0,0,-47) rot=(0,0,1;0rad)
  FullyConstrained = true
  MapMode = 5
  Placement = pos=(0,0,-47) rot=(0,0,1;0rad)
  Support = -> [XY_Plane]
  sketch-geometry (4):
    g0: LineSegment StartX=76 StartY=70 StartZ=0 EndX=116 EndY=70 EndZ=0
    g1: LineSegment StartX=116 StartY=70 StartZ=0 EndX=116 EndY=30 EndZ=0
    g2: LineSegment StartX=116 StartY=30 StartZ=0 EndX=76 EndY=30 EndZ=0
    g3: LineSegment StartX=76 StartY=30 StartZ=0 EndX=76 EndY=70 EndZ=0
  constraints (12):
    c: Coincident(g0,g1)
    c: Coincident(g1,g2)
    c: Coincident(g2,g3)
    c: Coincident(g3,g0)
    c: Horizontal(g0)
    c: Horizontal(g2)
    c: Vertical(g1)
    c: Vertical(g3)
    c: DistanceX(g0) = 76
    c: DistanceY(g0) = 70
    c: Distance(g3) = 40
    c: Distance(g0) = 40
FEATURE [PartDesign::Pocket] Pocket023
  BaseFeature = -> Pocket022
  Direction = (0,0,-1)
  Length = 8
  Length2 = 5
  Placement = pos=(0,0,0) rot=(1,0,0;1.5708rad)
  Profile = -> Sketch071
  ReferenceAxis = -> Sketch071 [N_Axis]
  Reversed = true
  Type = 0
FEATURE [PartDesign::Chamfer] Chamfer017
  Angle = 45
  Base = -> Hole001
  BaseFeature = -> Hole001
  ChamferType = 0
  FlipDirection = false
  Placement = pos=(0,0,0) rot=(0.57735,0.57735,0.57735;2.0944rad)
  Size = 1
  Size2 = 1
  SupportTransform = false
  UseAllEdges = false
FEATURE [PartDesign::Chamfer] Chamfer
  Angle = 45
  Base = -> Pocket023 [Edge23]
  BaseFeature = -> Pocket023
  ChamferType = 0
  FlipDirection = false
  Placement = pos=(0,0,0) rot=(1,0,0;1.5708rad)
  Size = 3
  Size2 = 1
  SupportTransform = false
  UseAllEdges = false
FEATURE [PartDesign::Chamfer] Chamfer018
  Angle = 45
  Base = -> Chamfer [Edge47]
  BaseFeature = -> Chamfer
  ChamferType = 0
  FlipDirection = false
  Placement = pos=(0,0,0) rot=(1,0,0;1.5708rad)
  Size = 3
  Size2 = 1
  SupportTransform = false
  UseAllEdges = false
FEATURE [PartDesign::Body] Body  label="Frame_Pitch_Belt_Clamp"
  Group = -> [Sketch,Pad,Sketch029,Hole,Sketch069,Hole006,Sketch070,Pocket022,Sketch071,Pocket023,Chamfer,Chamfer018]
  Origin = -> Origin
  Placement = pos=(2,0,0) rot=(0,0,1;0rad)
  Tip = -> Chamfer018
FEATURE [Sketcher::SketchObject] Sketch072
  AttachmentOffset = pos=(0,0,-24) rot=(0,0,1;0rad)
  FullyConstrained = false
  MapMode = 5
  Placement = pos=(0,0,-24) rot=(0,0,1;0rad)
  Support = -> [XY_Plane024]
  sketch-geometry (4):
    g0: LineSegment StartX=51 StartY=297 StartZ=0 EndX=93 EndY=297 EndZ=0
    g1: LineSegment StartX=93 StartY=297 StartZ=0 EndX=93 EndY=252 EndZ=0
    g2: LineSegment StartX=93 StartY=252 StartZ=0 EndX=51 EndY=252 EndZ=0
    g3: LineSegment StartX=51 StartY=252 StartZ=0 EndX=51 EndY=297 EndZ=0
  constraints (11):
    c: Coincident(g0,g1)
    c: Coincident(g1,g2)
    c: Coincident(g2,g3)
    c: Coincident(g3,g0)
    c: Horizontal(g0)
    c: Horizontal(g2)
    c: Vertical(g1)
    c: Vertical(g3)
    c: Distance(g2) = 42
    c: Distance(g3) = 45
    c: DistanceY(g2) = 252
FEATURE [PartDesign::Pad] Pad036
  Direction = (0,0,1)
  Length = 20.5
  Length2 = 10
  Profile = -> Sketch072
  ReferenceAxis = -> Sketch072 [N_Axis]
  Reversed = true
  Type = 0
FEATURE [Sketcher::SketchObject] Sketch073
  AttachmentOffset = pos=(0,0,-44.5) rot=(0,0,1;0rad)
  FullyConstrained = true
  MapMode = 5
  Placement = pos=(0,0,-44.5) rot=(0,0,1;0rad)
  Support = -> [XY_Plane024]
  sketch-geometry (20):
    g0: LineSegment StartX=30 StartY=304.5 StartZ=0 EndX=130 EndY=304.5 EndZ=0
    g1: LineSegment StartX=130 StartY=304.5 StartZ=0 EndX=130 EndY=244.5 EndZ=0
    g2: LineSegment StartX=130 StartY=244.5 StartZ=0 EndX=30 EndY=244.5 EndZ=0
    g3: LineSegment StartX=30 StartY=244.5 StartZ=0 EndX=30 EndY=304.5 EndZ=0
    g4: ArcOfCircle CenterX=124 CenterY=286.5 CenterZ=0 NormalX=0 NormalY=0 NormalZ=1 AngleXU=0 Radius=2.65 StartAngle=3.14159 EndAngle=6.28319
    g5: ArcOfCircle CenterX=124 CenterY=299 CenterZ=0 NormalX=0 NormalY=0 NormalZ=1 AngleXU=0 Radius=2.65 StartAngle=-9e-16 EndAngle=3.14159
    g6: LineSegment StartX=126.65 StartY=286.5 StartZ=0 EndX=126.65 EndY=299 EndZ=0
    g7: LineSegment StartX=121.35 StartY=299 StartZ=0 EndX=121.35 EndY=286.5 EndZ=0
    g8: ArcOfCircle CenterX=124 CenterY=250.5 CenterZ=0 NormalX=0 NormalY=0 NormalZ=1 AngleXU=0 Radius=2.65 StartAngle=3.14159 EndAngle=6.28319
    g9: ArcOfCircle CenterX=124 CenterY=263 CenterZ=0 NormalX=0 NormalY=0 NormalZ=1 AngleXU=0 Radius=2.65 StartAngle=-8e-15 EndAngle=3.14159
    g10: LineSegment StartX=126.65 StartY=250.5 StartZ=0 EndX=126.65 EndY=263 EndZ=0
    g11: LineSegment StartX=121.35 StartY=263 StartZ=0 EndX=121.35 EndY=250.5 EndZ=0
    g12: ArcOfCircle CenterX=36 CenterY=250.5 CenterZ=0 NormalX=0 NormalY=0 NormalZ=1 AngleXU=0 Radius=2.65 StartAngle=3.14159 EndAngle=6.28319
    g13: ArcOfCircle CenterX=36 CenterY=263 CenterZ=0 NormalX=0 NormalY=0 NormalZ=1 AngleXU=0 Radius=2.65 StartAngle=-9e-16 EndAngle=3.14159
    g14: LineSegment StartX=38.65 StartY=250.5 StartZ=0 EndX=38.65 EndY=263 EndZ=0
    g15: LineSegment StartX=33.35 StartY=263 StartZ=0 EndX=33.35 EndY=250.5 EndZ=0
    g16: ArcOfCircle CenterX=36 CenterY=286.5 CenterZ=0 NormalX=0 NormalY=0 NormalZ=1 AngleXU=0 Radius=2.65 StartAngle=3.14159 EndAngle=6.28319
    g17: ArcOfCircle CenterX=36 CenterY=299 CenterZ=0 NormalX=0 NormalY=0 NormalZ=1 AngleXU=0 Radius=2.65 StartAngle=8.8e-15 EndAngle=3.14159
    g18: LineSegment StartX=38.65 StartY=286.5 StartZ=0 EndX=38.65 EndY=299 EndZ=0
    g19: LineSegment StartX=33.35 StartY=299 StartZ=0 EndX=33.35 EndY=286.5 EndZ=0
  constraints (52):
    c: Coincident(g0,g1)
    c: Coincident(g1,g2)
    c: Coincident(g2,g3)
    c: Coincident(g3,g0)
    c: Horizontal(g0)
    c: Horizontal(g2)
    c: Vertical(g1)
    c: Vertical(g3)
    c: Tangent(g4,g6) = -1.5708
    c: Tangent(g6,g5) = -1.5708
    c: Tangent(g5,g7) = -1.5708
    c: Tangent(g7,g4) = -1.5708
    c: Equal(g4,g5)
    c: Vertical(g6)
    c: Distance(g2) = 100
    c: Distance(g1) = 60
    c: Tangent(g8,g10) = -1.5708
    c: Tangent(g10,g9) = -1.5708
    c: Tangent(g9,g11) = -1.5708
    c: Tangent(g11,g8) = -1.5708
    c: Equal(g8,g9)
    c: Vertical(g10)
    c: Tangent(g12,g14) = -1.5708
    c: Tangent(g14,g13) = -1.5708
    c: Tangent(g13,g15) = -1.5708
    c: Tangent(g15,g12) = -1.5708
    c: Equal(g12,g13)
    c: Vertical(g14)
    c: Tangent(g16,g18) = -1.5708
    c: Tangent(g18,g17) = -1.5708
    c: Tangent(g17,g19) = -1.5708
    c: Tangent(g19,g16) = -1.5708
    c: Equal(g16,g17)
    c: Vertical(g18)
    c: Equal(g16,g4)
    c: Equal(g4,g8)
    c: Equal(g8,g12)
    c: Equal(g19,g15)
    c: Equal(g15,g11)
    c: Equal(g11,g7)
    c: Vertical(g12,g16)
    c: Vertical(g8,g4)
    c: Horizontal(g5,g17)
    c: Horizontal(g13,g9)
    c: Diameter(g16) = 5.3
    c: Distance(g15) = 12.5
    c: Distance(g12,g8) = 88
    c: DistanceX(g8,g1) = 6
    c: Distance(g12,g16) = 36
    c: DistanceY(g2,g12) = 6
    c: DistanceX(g1) = 130
    c: DistanceY(g1) = 244.5
FEATURE [PartDesign::Pad] Pad037
  BaseFeature = -> Pad036
  Direction = (0,0,1)
  Length = 10
  Length2 = 10
  Profile = -> Sketch073
  ReferenceAxis = -> Sketch073 [N_Axis]
  Type = 0
FEATURE [Sketcher::SketchObject] Sketch074
  AttachmentOffset = pos=(0,0,-44) rot=(0,0,1;0rad)
  FullyConstrained = true
  MapMode = 5
  Placement = pos=(0,0,-44) rot=(0,0,1;0rad)
  Support = -> [XY_Plane024]
  sketch-geometry (4):
    g0: Circle CenterX=59 CenterY=289 CenterZ=0 NormalX=0 NormalY=0 NormalZ=1 AngleXU=0 Radius=3.15
    g1: Circle CenterX=77 CenterY=289 CenterZ=0 NormalX=0 NormalY=0 NormalZ=1 AngleXU=0 Radius=3.15
    g2: Circle CenterX=77 CenterY=260 CenterZ=0 NormalX=0 NormalY=0 NormalZ=1 AngleXU=0 Radius=3.15
    g3: Circle CenterX=59 CenterY=260 CenterZ=0 NormalX=0 NormalY=0 NormalZ=1 AngleXU=0 Radius=3.15
  constraints (12):
    c: Horizontal(g0,g1)
    c: Vertical(g0,g3)
    c: Horizontal(g3,g2)
    c: Vertical(g2,g1)
    c: Distance(g3,g0) = 29
    c: Distance(g3,g2) = 18
    c: Equal(g0,g1)
    c: Equal(g1,g2)
    c: Equal(g2,g3)
    c: Diameter(g0) = 6.3
    c: DistanceX(g3) = 59
    c: DistanceY(g3) = 260
FEATURE [Sketcher::SketchObject] Sketch075
  AttachmentOffset = pos=(0,0,-44.5) rot=(0,0,1;0rad)
  FullyConstrained = true
  MapMode = 5
  Placement = pos=(0,0,-44.5) rot=(0,0,1;0rad)
  Support = -> [XY_Plane024]
  sketch-geometry (28):
    g0: LineSegment StartX=64.15 StartY=257.027 StartZ=0 EndX=64.15 EndY=262.973 EndZ=0
    g1: LineSegment StartX=64.15 StartY=262.973 StartZ=0 EndX=59 EndY=265.947 EndZ=0
    g2: LineSegment StartX=59 StartY=265.947 StartZ=0 EndX=53.85 EndY=262.973 EndZ=0
    g3: LineSegment StartX=53.85 StartY=262.973 StartZ=0 EndX=53.85 EndY=257.027 EndZ=0
    g4: LineSegment StartX=53.85 StartY=257.027 StartZ=0 EndX=59 EndY=254.053 EndZ=0
    g5: LineSegment StartX=59 StartY=254.053 StartZ=0 EndX=64.15 EndY=257.027 EndZ=0
    g6: Circle CenterX=59 CenterY=260 CenterZ=0 NormalX=0 NormalY=0 NormalZ=1 AngleXU=0 Radius=5.94671
    g7: LineSegment StartX=82.15 StartY=257.027 StartZ=0 EndX=82.15 EndY=262.973 EndZ=0
    g8: LineSegment StartX=82.15 StartY=262.973 StartZ=0 EndX=77 EndY=265.947 EndZ=0
    g9: LineSegment StartX=77 StartY=265.947 StartZ=0 EndX=71.85 EndY=262.973 EndZ=0
    g10: LineSegment StartX=71.85 StartY=262.973 StartZ=0 EndX=71.85 EndY=257.027 EndZ=0
    g11: LineSegment StartX=71.85 StartY=257.027 StartZ=0 EndX=77 EndY=254.053 EndZ=0
    g12: LineSegment StartX=77 StartY=254.053 StartZ=0 EndX=82.15 EndY=257.027 EndZ=0
    g13: Circle CenterX=77 CenterY=260 CenterZ=0 NormalX=0 NormalY=0 NormalZ=1 AngleXU=0 Radius=5.94671
    g14: LineSegment StartX=82.15 StartY=286.027 StartZ=0 EndX=82.15 EndY=291.973 EndZ=0
    g15: LineSegment StartX=82.15 StartY=291.973 StartZ=0 EndX=77 EndY=294.947 EndZ=0
    g16: LineSegment StartX=77 StartY=294.947 StartZ=0 EndX=71.85 EndY=291.973 EndZ=0
    g17: LineSegment StartX=71.85 StartY=291.973 StartZ=0 EndX=71.85 EndY=286.027 EndZ=0
    g18: LineSegment StartX=71.85 StartY=286.027 StartZ=0 EndX=77 EndY=283.053 EndZ=0
    g19: LineSegment StartX=77 StartY=283.053 StartZ=0 EndX=82.15 EndY=286.027 EndZ=0
    g20: Circle CenterX=77 CenterY=289 CenterZ=0 NormalX=0 NormalY=0 NormalZ=1 AngleXU=0 Radius=5.94671
    g21: LineSegment StartX=64.15 StartY=286.027 StartZ=0 EndX=64.15 EndY=291.973 EndZ=0
    g22: LineSegment StartX=64.15 StartY=291.973 StartZ=0 EndX=59 EndY=294.947 EndZ=0
    g23: LineSegment StartX=59 StartY=294.947 StartZ=0 EndX=53.85 EndY=291.973 EndZ=0
    g24: LineSegment StartX=53.85 StartY=291.973 StartZ=0 EndX=53.85 EndY=286.027 EndZ=0
    g25: LineSegment StartX=53.85 StartY=286.027 StartZ=0 EndX=59 EndY=283.053 EndZ=0
    g26: LineSegment StartX=59 StartY=283.053 StartZ=0 EndX=64.15 EndY=286.027 EndZ=0
    g27: Circle CenterX=59 CenterY=289 CenterZ=0 NormalX=0 NormalY=0 NormalZ=1 AngleXU=0 Radius=5.94671
  constraints (68):
    c: Coincident(g0,g1)
    c: Coincident(g1,g2)
    c: Coincident(g2,g3)
    c: Coincident(g3,g4)
    c: Coincident(g4,g5)
    c: Coincident(g5,g0)
    c: Equal(g0, g1-g5) x5
    c: PointOnObject(g0,g6)
    c: PointOnObject(g1,g6)
    c: PointOnObject(g2,g6)
    c: PointOnObject(g3,g6)
    c: PointOnObject(g4,g6)
    c: PointOnObject(g5,g6)
    c: Coincident(g7,g8)
    c: Coincident(g8,g9)
    c: Coincident(g9,g10)
    c: Coincident(g10,g11)
    c: Coincident(g11,g12)
    c: Coincident(g12,g7)
    c: Equal(g7, g8-g12) x5
    c: PointOnObject(g7,g13)
    c: PointOnObject(g8,g13)
    c: PointOnObject(g9,g13)
    c: PointOnObject(g10,g13)
    c: PointOnObject(g11,g13)
    c: PointOnObject(g12,g13)
    c: Coincident(g14,g15)
    c: Coincident(g15,g16)
    c: Coincident(g16,g17)
    c: Coincident(g17,g18)
    c: Coincident(g18,g19)
    c: Coincident(g19,g14)
    c: Equal(g14, g15-g19) x5
    c: PointOnObject(g14,g20)
    c: PointOnObject(g15,g20)
    c: PointOnObject(g16,g20)
    c: PointOnObject(g17,g20)
    c: PointOnObject(g18,g20)
    c: PointOnObject(g19,g20)
    c: Coincident(g21,g22)
    c: Coincident(g22,g23)
    c: Coincident(g23,g24)
    c: Coincident(g24,g25)
    c: Coincident(g25,g26)
    c: Coincident(g26,g21)
    c: Equal(g21, g22-g26) x5
    c: PointOnObject(g21,g27)
    c: PointOnObject(g22,g27)
    c: PointOnObject(g23,g27)
    c: PointOnObject(g24,g27)
    c: PointOnObject(g25,g27)
    c: PointOnObject(g26,g27)
    c: Equal(g6,g13)
    c: Equal(g13,g20)
    c: Equal(g20,g27)
    c: Vertical(g3)
    c: Vertical(g10)
    c: Vertical(g17)
    c: Vertical(g24)
    c: Distance(g2,g0) = 10.3
    c: Vertical(g27,g6)
    c: Vertical(g20,g13)
    c: Horizontal(g6,g13)
    c: Horizontal(g27,g20)
    c: DistanceY(g6) = 260
    c: DistanceX(g6) = 59
    c: Distance(g6,g13) = 18
    c: Distance(g6,g27) = 29
FEATURE [PartDesign::Pocket] Pocket024
  BaseFeature = -> Pad037
  Direction = (0,0,-1)
  Length = 10
  Length2 = 5
  Profile = -> Sketch075
  ReferenceAxis = -> Sketch075 [N_Axis]
  Reversed = true
  Type = 0
FEATURE [PartDesign::Hole] Hole007
  BaseFeature = -> Pocket024
  CustomThreadClearance = 0
  Depth = 25
  DepthType = 0
  Diameter = 6.4
  DrillForDepth = false
  DrillPoint = 1
  DrillPointAngle = 118
  HoleCutCountersinkAngle = 90
  HoleCutCustomValues = false
  HoleCutDepth = 0
  HoleCutDiameter = 6.1
  HoleCutType = 0
  ModelThread = false
  Profile = -> Sketch074
  Reversed = true
  Tapered = false
  TaperedAngle = 90
  ThreadClass = 0
  ThreadDepth = 25
  ThreadDepthType = 0
  ThreadDirection = 0
  ThreadFit = 0
  ThreadSize = 0
  ThreadType = 0
  Threaded = false
  UseCustomThreadClearance = false
FEATURE [PartDesign::Chamfer] Chamfer019
  Angle = 45
  Base = -> Hole007 [Face11,Face12,Face14,Face13]
  BaseFeature = -> Hole007
  ChamferType = 0
  FlipDirection = false
  Size = 1
  Size2 = 1
  SupportTransform = false
  UseAllEdges = false
FEATURE [PartDesign::Chamfer] Chamfer020
  Angle = 45
  Base = -> Chamfer019 [Edge62,Edge63,Edge65,Edge67]
  BaseFeature = -> Chamfer019
  ChamferType = 0
  FlipDirection = false
  Size = 1
  Size2 = 1
  SupportTransform = false
  UseAllEdges = false
FEATURE [PartDesign::Body] Body001009  label="Pitch_Motor_Mount"
  Group = -> [Sketch072,Pad036,Sketch073,Pad037,Sketch074,Sketch075,Pocket024,Hole007,Chamfer019,Chamfer020]
  Origin = -> Origin024
  Placement = pos=(-4.75,0.5,-6.5) rot=(0,0,1;0rad)
  Tip = -> Chamfer020
FEATURE [Sketcher::SketchObject] Sketch076
  AttachmentOffset = pos=(0,0,-51) rot=(0,0,1;0rad)
  FullyConstrained = true
  MapMode = 5
  Placement = pos=(0,0,-51) rot=(0,0,1;0rad)
  Support = -> [XY_Plane025]
  sketch-geometry (4):
    g0: LineSegment StartX=92 StartY=240 StartZ=0 EndX=110 EndY=240 EndZ=0
    g1: LineSegment StartX=110 StartY=240 StartZ=0 EndX=110 EndY=205 EndZ=0
    g2: LineSegment StartX=110 StartY=205 StartZ=0 EndX=92 EndY=205 EndZ=0
    g3: LineSegment StartX=92 StartY=205 StartZ=0 EndX=92 EndY=240 EndZ=0
  constraints (12):
    c: Coincident(g0,g1)
    c: Coincident(g1,g2)
    c: Coincident(g2,g3)
    c: Coincident(g3,g0)
    c: Horizontal(g0)
    c: Horizontal(g2)
    c: Vertical(g1)
    c: Vertical(g3)
    c: Distance(g2) = 18
    c: Distance(g1) = 35
    c: DistanceX(g2) = 92
    c: DistanceY(g2) = 205
FEATURE [PartDesign::Pad] Pad038
  Direction = (0,0,1)
  Length = 17
  Length2 = 10
  Profile = -> Sketch076
  ReferenceAxis = -> Sketch076 [N_Axis]
  Type = 0
FEATURE [Sketcher::SketchObject] Sketch077
  AttachmentOffset = pos=(0,0,-34) rot=(0,0,1;0rad)
  FullyConstrained = true
  MapMode = 5
  Placement = pos=(0,0,-34) rot=(0,0,1;0rad)
  Support = -> [XY_Plane025]
  sketch-geometry (2):
    g0: Circle CenterX=101 CenterY=232.75 CenterZ=0 NormalX=0 NormalY=0 NormalZ=1 AngleXU=0 Radius=4.15
    g1: Circle CenterX=101 CenterY=212.75 CenterZ=0 NormalX=0 NormalY=0 NormalZ=1 AngleXU=0 Radius=4.15
  constraints (6):
    c: Vertical(g0,g1)
    c: Distance(g1,g0) = 20
    c: DistanceY(g1) = 212.75
    c: DistanceX(g1) = 101
    c: Diameter(g1) = 8.3
    c: Equal(g1,g0)
FEATURE [PartDesign::Hole] Hole008
  BaseFeature = -> Pad038
  CustomThreadClearance = 0
  Depth = 25
  DepthType = 0
  Diameter = 5.3
  DrillForDepth = false
  DrillPoint = 1
  DrillPointAngle = 118
  HoleCutCountersinkAngle = 90
  HoleCutCustomValues = false
  HoleCutDepth = 5.4
  HoleCutDiameter = 8.8
  HoleCutType = 1
  ModelThread = false
  Profile = -> Sketch077
  Tapered = false
  TaperedAngle = 90
  ThreadClass = 0
  ThreadDepth = 25
  ThreadDepthType = 0
  ThreadDirection = 0
  ThreadFit = 1
  ThreadSize = 13
  ThreadType = 1
  Threaded = false
  UseCustomThreadClearance = false
FEATURE [PartDesign::Chamfer] Chamfer021
  Angle = 45
  Base = -> Hole008 [Face1,Face3,Face2,Face6]
  BaseFeature = -> Hole008
  ChamferType = 0
  FlipDirection = false
  Size = 1
  Size2 = 1
  SupportTransform = false
  UseAllEdges = false
FEATURE [PartDesign::Body] Body001010  label="Pitch_Rear_Stop"
  Group = -> [Sketch076,Pad038,Sketch077,Hole008,Chamfer021]
  Origin = -> Origin025
  Placement = pos=(0,3.75,0) rot=(0,0,1;0rad)
  Tip = -> Chamfer021
FEATURE [PartDesign::Chamfer] Chamfer022
  Angle = 45
  Base = -> Hole001 [Edge30]
  BaseFeature = -> Hole001
  ChamferType = 0
  FlipDirection = false
  Placement = pos=(0,0,0) rot=(0.57735,0.57735,0.57735;2.0944rad)
  Size = 0.5
  Size2 = 1
  SupportTransform = false
  UseAllEdges = false
FEATURE [PartDesign::Body] Body014  label="Pitch Encoder Pulley Mount"
  Group = -> [Sketch053,Pad033,Sketch057,Pocket018,Sketch058,Pad034,Sketch059,Pocket020,Sketch060,Hole001,Chamfer017,Chamfer022]
  Origin = -> Origin019
  Placement = pos=(18.5,0,0) rot=(0,0,1;0rad)
  Tip = -> Chamfer022
FEATURE [App::Part] Part003  label="Pitch_Pulley_Mount_Assy"
  Group = -> [Body012,Body014]
  Origin = -> Origin023
  Placement = pos=(3.75,-29.5,7.5) rot=(0,0,1;0rad)
FEATURE [Sketcher::SketchObject] Sketch078
  AttachmentOffset = pos=(0,0,-58.5) rot=(0,0,1;0rad)
  FullyConstrained = true
  MapMode = 5
  Placement = pos=(0,0,-58.5) rot=(0,0,1;0rad)
  Support = -> [XY_Plane026]
  sketch-geometry (6):
    g0: LineSegment StartX=111 StartY=40 StartZ=0 EndX=81 EndY=40 EndZ=0
    g1: LineSegment StartX=81 StartY=40 StartZ=0 EndX=81 EndY=1 EndZ=0
    g2: LineSegment StartX=81 StartY=1 StartZ=0 EndX=66.5 EndY=1 EndZ=0
    g3: LineSegment StartX=66.5 StartY=1 StartZ=0 EndX=66.5 EndY=-43 EndZ=0
    g4: LineSegment StartX=66.5 StartY=-43 StartZ=0 EndX=111 EndY=-43 EndZ=0
    g5: LineSegment StartX=111 StartY=-43 StartZ=0 EndX=111 EndY=40 EndZ=0
  constraints (18):
    c: Coincident(g0,g1)
    c: Vertical(g1)
    c: Coincident(g1,g2)
    c: Horizontal(g2)
    c: Coincident(g2,g3)
    c: Vertical(g3)
    c: Coincident(g3,g4)
    c: Horizontal(g4)
    c: Coincident(g4,g5)
    c: Coincident(g5,g0)
    c: Vertical(g5)
    c: Horizontal(g0)
    c: DistanceY(g0) = 40
    c: DistanceX(g0) = 111
    c: Distance(g5) = 83
    c: Distance(g4) = 44.5
    c: DistanceY(g3,g3) = 44
    c: Distance(g0) = 30
FEATURE [PartDesign::Pad] Pad039
  Direction = (0,0,1)
  Length = 3
  Length2 = 10
  Profile = -> Sketch078
  ReferenceAxis = -> Sketch078 [N_Axis]
  Type = 0
FEATURE [Sketcher::SketchObject] Sketch079
  AttachmentOffset = pos=(1,0,-54.5) rot=(0,0,1;0rad)
  FullyConstrained = true
  MapMode = 5
  Placement = pos=(1,0,-54.5) rot=(0,0,1;0rad)
  Support = -> [XY_Plane026]
  sketch-geometry (3):
    g0: Circle CenterX=95 CenterY=18 CenterZ=0 NormalX=0 NormalY=0 NormalZ=1 AngleXU=0 Radius=2.7
    g1: Circle CenterX=82 CenterY=-21 CenterZ=0 NormalX=0 NormalY=0 NormalZ=1 AngleXU=0 Radius=2.7
    g2: Circle CenterX=95 CenterY=-34 CenterZ=0 NormalX=0 NormalY=0 NormalZ=1 AngleXU=0 Radius=2.7
  constraints (9):
    c: Equal(g0,g1)
    c: Equal(g1,g2)
    c: Diameter(g0) = 5.4
    c: Vertical(g0,g2)
    c: DistanceX(g0) = 95
    c: DistanceY(g0) = 18
    c: DistanceX(g1) = 82
    c: DistanceY(g1) = -21
    c: Distance(g0,g2) = 52
FEATURE [PartDesign::Hole] Hole009
  BaseFeature = -> Pad039
  CustomThreadClearance = 0
  Depth = 192.327
  DepthType = 1
  Diameter = 5.8
  DrillForDepth = false
  DrillPoint = 1
  DrillPointAngle = 118
  HoleCutCountersinkAngle = 90
  HoleCutCustomValues = false
  HoleCutDepth = 0
  HoleCutDiameter = 8.7
  HoleCutType = 0
  ModelThread = false
  Profile = -> Sketch079
  Tapered = false
  TaperedAngle = 90
  ThreadClass = 0
  ThreadDepth = 192.327
  ThreadDepthType = 0
  ThreadDirection = 0
  ThreadFit = 2
  ThreadSize = 13
  ThreadType = 1
  Threaded = false
  UseCustomThreadClearance = false
FEATURE [PartDesign::Body] Body001011  label="Pitch Encoder Pulley Mount001"
  Group = -> [Sketch078,Pad039,Sketch079,Hole009]
  Origin = -> Origin026
  Placement = pos=(12.25,-29.5,0) rot=(0,0,1;0rad)
  Tip = -> Hole009
FEATURE [Mesh::Feature] CadetYokev3__1__v6  label="CadetYokev3 (1) v6"
  Placement = pos=(-0.25,-3.25,-100.5) rot=(0,0,1;0rad)
FEATURE [Mesh::Feature] _8_5M_15_Yoke_Column_Pulley_v24  label="28_5M_15_Yoke_Column_Pulley v24"
  Placement = pos=(-1.17e-14,-45.5,0) rot=(0,0,1;1.5708rad)

RESOLVED EXTERNAL PARTS (link-assembly join: the EXTERNAL_REF files above that resolve inside this repo's crawl, each included once):
---- part Parts/Encoder.FCStd = doc fcstd_7a44d7247bb3 ----
FCSTD DOCUMENT  (FreeCAD 0.21R32110 (Git))
Label: Encoder
License: All rights reserved
LicenseURL: http://en.wikipedia.org/wiki/All_rights_reserved
objects: Sketcher::SketchObject×3, PartDesign::Pad×3, PartDesign::Body×1, App::Part×1
note: 10 computed .brp shape members not serialized (recipe doc carries the construction recipe); baked Part::Feature solids carry a one-line shape summary decoded from their .brp

FEATURE [Sketcher::SketchObject] Sketch002
  AttachmentOffset = pos=(0,0,-60) rot=(0,0,1;0rad)
  FullyConstrained = true
  MapMode = 5
  Placement = pos=(0,82,3) rot=(1,0,0;1.5708rad)
  sketch-geometry (1):
    g0: Circle CenterX=38 CenterY=-5 CenterZ=0 NormalX=0 NormalY=0 NormalZ=1 AngleXU=0 Radius=19
  constraints (3):
    c: Diameter(g0) = 38
    c: DistanceX(g0) = 38
    c: DistanceY(g0) = -5
FEATURE [PartDesign::Pad] Pad002  label="Encoder"
  Direction = (0,-1,2e-16)
  Length = 34
  Length2 = 10
  Placement = pos=(0,82,3) rot=(1,0,0;1.5708rad)
  Profile = -> Sketch002
  ReferenceAxis = -> Sketch002 [N_Axis]
  Reversed = true
  Type = 0
FEATURE [Sketcher::SketchObject] Sketch036
  AttachmentOffset = pos=(0,0,-80) rot=(0,0,1;0rad)
  FullyConstrained = true
  MapMode = 5
  Placement = pos=(0,80,1.78e-14) rot=(1,0,0;1.5708rad)
  Support = -> [XZ_Plane013]
  sketch-geometry (1):
    g0: Circle CenterX=38 CenterY=-5 CenterZ=0 NormalX=0 NormalY=0 NormalZ=1 AngleXU=0 Radius=10
  constraints (3):
    c: DistanceX(g0) = 38
    c: DistanceY(g0) = -5
    c: Diameter(g0) = 20
FEATURE [PartDesign::Pad] Pad025
  Direction = (0,-1,-2e-16)
  Length = 5
  Length2 = 10
  Placement = pos=(0,0,0) rot=(1,0,0;1.5708rad)
  Profile = -> Sketch036
  ReferenceAxis = -> Sketch036 [N_Axis]
  Reversed = true
  Type = 0
FEATURE [Sketcher::SketchObject] Sketch037
  AttachmentOffset = pos=(0,0,-80) rot=(0,0,1;0rad)
  FullyConstrained = true
  MapMode = 5
  Placement = pos=(0,80,1.78e-14) rot=(1,0,0;1.5708rad)
  Support = -> [XZ_Plane013]
  sketch-geometry (1):
    g0: Circle CenterX=38 CenterY=-5 CenterZ=0 NormalX=0 NormalY=0 NormalZ=1 AngleXU=0 Radius=3
  constraints (3):
    c: Diameter(g0) = 6
    c: DistanceY(g0) = -5
    c: DistanceX(g0) = 38
FEATURE [PartDesign::Pad] Pad026
  BaseFeature = -> Pad025
  Direction = (0,-1,-2e-16)
  Length = 13
  Length2 = 10
  Placement = pos=(0,0,0) rot=(1,0,0;1.5708rad)
  Profile = -> Sketch037
  ReferenceAxis = -> Sketch037 [N_Axis]
  Type = 0
FEATURE [PartDesign::Body] Body009  label="Encoder_Shaft"
  Group = -> [Sketch036,Sketch037,Pad025,Pad026]
  Origin = -> Origin013
  Placement = pos=(0,-3,3) rot=(0,0,1;0rad)
  Tip = -> Pad026
FEATURE [App::Part] Part
  Group = -> [Sketch002,Pad002,Body009]
  Origin = -> Origin
---- part Parts/Frame.FCStd = doc fcstd_649fad6ec7f0 ----
FCSTD DOCUMENT  (FreeCAD 0.21R32110 (Git))
Label: Frame
License: All rights reserved
LicenseURL: http://en.wikipedia.org/wiki/All_rights_reserved
objects: Sketcher::SketchObject×12, PartDesign::Pad×6, PartDesign::Pocket×6, PartDesign::Body×5, PartDesign::Chamfer×5, PartDesign::LinearPattern×1, PartDesign::CoordinateSystem×1, PartDesign::FeatureBase×1, App::Part×1
note: 54 computed .brp shape members not serialized (recipe doc carries the construction recipe); baked Part::Feature solids carry a one-line shape summary decoded from their .brp

FEATURE [Sketcher::SketchObject] Sketch
  AttachmentOffset = pos=(0,0,-42) rot=(0,0,1;0rad)
  FullyConstrained = true
  MapMode = 5
  Placement = pos=(-42,9.3e-15,-9.3e-15) rot=(0.57735,0.57735,0.57735;2.0944rad)
  Support = -> [YZ_Plane004]
  sketch-geometry (8):
    g0: LineSegment StartX=-7 StartY=0 StartZ=0 EndX=7 EndY=0 EndZ=0
    g1: LineSegment StartX=7 StartY=0 StartZ=0 EndX=7 EndY=-10 EndZ=0
    g2: LineSegment StartX=7 StartY=-10 StartZ=0 EndX=3 EndY=-17 EndZ=0
    g3: LineSegment StartX=3 StartY=-17 StartZ=0 EndX=3 EndY=-35 EndZ=0
    g4: LineSegment StartX=3 StartY=-35 StartZ=0 EndX=-3 EndY=-35 EndZ=0
    g5: LineSegment StartX=-3 StartY=-35 StartZ=0 EndX=-3 EndY=-17 EndZ=0
    g6: LineSegment StartX=-3 StartY=-17 StartZ=0 EndX=-7 EndY=-10 EndZ=0
    g7: LineSegment StartX=-7 StartY=-10 StartZ=0 EndX=-7 EndY=0 EndZ=0
  constraints (22):
    c: Coincident(g0,g1)
    c: Coincident(g1,g2)
    c: Coincident(g2,g3)
    c: Vertical(g3)
    c: Coincident(g3,g4)
    c: Coincident(g4,g5)
    c: Vertical(g5)
    c: Coincident(g5,g6)
    c: Coincident(g6,g7)
    c: Coincident(g7,g0)
    c: Vertical(g7)
    c: Vertical(g1)
    c: Equal(g7,g1)
    c: Equal(g5,g3)
    c: Symmetric(g0,g0,g-2)
    c: Distance(g0) = 14
    c: Distance(g4) = 6
    c: Symmetric(g4,g3,g-2)
    c: Distance(g5) = 18
    c: Horizontal(g0,g-1)
    c: DistanceY(g4) = -35
    c: Distance(g7) = 10
FEATURE [PartDesign::Pad] Pad
  Direction = (1,-2e-16,3e-16)
  Length = 110
  Length2 = 10
  Placement = pos=(0,0,0) rot=(0.57735,0.57735,0.57735;2.0944rad)
  Profile = -> Sketch
  ReferenceAxis = -> Sketch [N_Axis]
  Type = 0
FEATURE [Sketcher::SketchObject] Sketch001
  FullyConstrained = true
  MapMode = 5
  Placement = pos=(0,0,0) rot=(1,0,0;1.5708rad)
  Support = -> [XZ_Plane]
  sketch-geometry (1):
    g0: Circle CenterX=0 CenterY=0 CenterZ=0 NormalX=0 NormalY=0 NormalZ=1 AngleXU=0 Radius=21
  constraints (2):
    c: Coincident(g0,g-1)
    c: Diameter(g0) = 42
FEATURE [Sketcher::SketchObject] Sketch002
  FullyConstrained = true
  MapMode = 5
  Support = -> [XY_Plane]
  sketch-geometry (2):
    g0: Circle CenterX=-28.5 CenterY=0 CenterZ=0 NormalX=0 NormalY=0 NormalZ=1 AngleXU=0 Radius=3.45
    g1: Circle CenterX=28.5 CenterY=0 CenterZ=0 NormalX=0 NormalY=0 NormalZ=1 AngleXU=0 Radius=3.45
  constraints (5):
    c: PointOnObject(g0,g-1)
    c: Equal(g0,g1)
    c: Diameter(g0) = 6.9
    c: Symmetric(g0,g1,g-2)
    c: DistanceX(g0,g1) = 57
FEATURE [PartDesign::Pocket] Pocket001
  BaseFeature = -> Pad
  Direction = (0,0,-1)
  Length = 11
  Length2 = 5
  Placement = pos=(0,0,0) rot=(0.57735,0.57735,0.57735;2.0944rad)
  Profile = -> Sketch002
  ReferenceAxis = -> Sketch002 [N_Axis]
  Type = 0
FEATURE [Sketcher::SketchObject] Sketch003
  FullyConstrained = true
  MapMode = 5
  Placement = pos=(0,0,0) rot=(1,0,0;1.5708rad)
  Support = -> [XZ_Plane]
  sketch-geometry (1):
    g0: Circle CenterX=0 CenterY=0 CenterZ=0 NormalX=0 NormalY=0 NormalZ=1 AngleXU=0 Radius=19
  constraints (2):
    c: Coincident(g0,g-1)
    c: Diameter(g0) = 38
FEATURE [Sketcher::SketchObject] Sketch004
  FullyConstrained = true
  MapMode = 5
  Placement = pos=(0,0,0) rot=(1,0,0;1.5708rad)
  Support = -> [XZ_Plane]
  sketch-geometry (2):
    g0: Circle CenterX=-10 CenterY=-28 CenterZ=0 NormalX=0 NormalY=0 NormalZ=1 AngleXU=0 Radius=2.1
    g1: Circle CenterX=10 CenterY=-28 CenterZ=0 NormalX=0 NormalY=0 NormalZ=1 AngleXU=0 Radius=2.1
  constraints (5):
    c: DistanceX(g0,g1) = 20
    c: Symmetric(g0,g1,g-2)
    c: Equal(g0,g1)
    c: Diameter(g0) = 4.2
    c: DistanceY(g0) = -28
FEATURE [PartDesign::Pocket] Pocket003
  BaseFeature = -> Pocket001
  Direction = (0,1,2e-16)
  Length = 5
  Length2 = 5
  Midplane = true
  Placement = pos=(0,0,0) rot=(0.57735,0.57735,0.57735;2.0944rad)
  Profile = -> Sketch004
  ReferenceAxis = -> Sketch004 [N_Axis]
  Type = 1
FEATURE [Sketcher::SketchObject] Sketch005
  FullyConstrained = true
  MapMode = 5
  Placement = pos=(0,0,0) rot=(1,0,0;1.5708rad)
  Support = -> [XZ_Plane]
  sketch-geometry (8):
    g0: LineSegment StartX=32 StartY=-35 StartZ=0 EndX=39 EndY=-35 EndZ=0
    g1: LineSegment StartX=39 StartY=-35 StartZ=0 EndX=39 EndY=-27 EndZ=0
    g2: LineSegment StartX=39 StartY=-27 StartZ=0 EndX=32 EndY=-27 EndZ=0
    g3: LineSegment StartX=32 StartY=-27 StartZ=0 EndX=32 EndY=-35 EndZ=0
    g4: LineSegment StartX=42 StartY=-35 StartZ=0 EndX=49 EndY=-35 EndZ=0
    g5: LineSegment StartX=49 StartY=-35 StartZ=0 EndX=49 EndY=-27 EndZ=0
    g6: LineSegment StartX=49 StartY=-27 StartZ=0 EndX=42 EndY=-27 EndZ=0
    g7: LineSegment StartX=42 StartY=-27 StartZ=0 EndX=42 EndY=-35 EndZ=0
  constraints (24):
    c: Coincident(g0,g1)
    c: Coincident(g1,g2)
    c: Coincident(g2,g3)
    c: Coincident(g3,g0)
    c: Horizontal(g0)
    c: Horizontal(g2)
    c: Vertical(g1)
    c: Vertical(g3)
    c: Coincident(g4,g5)
    c: Coincident(g5,g6)
    c: Coincident(g6,g7)
    c: Coincident(g7,g4)
    c: Horizontal(g4)
    c: Horizontal(g6)
    c: Vertical(g5)
    c: Vertical(g7)
    c: Distance(g0) = 7
    c: Equal(g0,g4)
    c: Distance(g3) = 8
    c: Equal(g3,g7)
    c: Horizontal(g0,g4)
    c: DistanceX(g0,g4) = 3
    c: DistanceX(g0) = 32
    c: DistanceY(g0) = -35
FEATURE [PartDesign::Pocket] Pocket004
  BaseFeature = -> Pocket003
  Direction = (0,1,2e-16)
  Length = 5
  Length2 = 5
  Midplane = true
  Placement = pos=(0,0,0) rot=(0.57735,0.57735,0.57735;2.0944rad)
  Profile = -> Sketch005
  ReferenceAxis = -> Sketch005 [N_Axis]
  Type = 1
FEATURE [Sketcher::SketchObject] Sketch006
  FullyConstrained = true
  MapMode = 5
  Placement = pos=(0,0,0) rot=(1,0,0;1.5708rad)
  Support = -> [XZ_Plane]
  sketch-geometry (2):
    g0: LineSegment StartX=-24 StartY=2.9e-15 StartZ=0 EndX=24 EndY=-5.69382e-05 EndZ=0
    g1: ArcOfCircle CenterX=0 CenterY=0 CenterZ=0 NormalX=0 NormalY=0 NormalZ=1 AngleXU=0 Radius=24 StartAngle=3.14159 EndAngle=6.28318
  constraints (6):
    c: Coincident(g1,g-1)
    c: Diameter(g1) = 48
    c: Coincident(g0,g1)
    c: Coincident(g0,g1)
    c: DistanceY(g0) = 0
    c: DistanceX(g0,g0) = 48
FEATURE [PartDesign::Pad] Pad001
  BaseFeature = -> Pocket004
  Direction = (0,-1,-2e-16)
  Length = 16
  Length2 = 10
  Midplane = true
  Placement = pos=(0,0,0) rot=(0.57735,0.57735,0.57735;2.0944rad)
  Profile = -> Sketch006
  ReferenceAxis = -> Sketch006 [N_Axis]
  Type = 0
FEATURE [PartDesign::Pocket] Pocket
  BaseFeature = -> Pad001
  Direction = (0,1,2e-16)
  Length = 18
  Length2 = 5
  Midplane = true
  Placement = pos=(0,0,0) rot=(0.57735,0.57735,0.57735;2.0944rad)
  Profile = -> Sketch003
  ReferenceAxis = -> Sketch003 [N_Axis]
  Type = 0
FEATURE [PartDesign::Pocket] Pocket005
  BaseFeature = -> Pocket
  Direction = (0,1,2e-16)
  Length = 9.2
  Length2 = 5
  Midplane = true
  Placement = pos=(0,0,0) rot=(0.57735,0.57735,0.57735;2.0944rad)
  Profile = -> Sketch001
  ReferenceAxis = -> Sketch001 [N_Axis]
  Type = 0
FEATURE [Sketcher::SketchObject] Sketch007
  AttachmentOffset = pos=(-18,21,-30) rot=(0,0,1;0rad)
  FullyConstrained = true
  MapMode = 5
  Placement = pos=(-123,-11.5,-35) rot=(0,0,1;0rad)
  sketch-geometry (8):
    g0: LineSegment StartX=62.5 StartY=-1 StartZ=0 EndX=89.5 EndY=-1 EndZ=0
    g1: LineSegment StartX=89.5 StartY=-1 StartZ=0 EndX=89.5 EndY=24 EndZ=0
    g2: LineSegment StartX=89.5 StartY=24 StartZ=0 EndX=62.5 EndY=24 EndZ=0
    g3: LineSegment StartX=62.5 StartY=24 StartZ=0 EndX=62.5 EndY=-1 EndZ=0
    g4: Circle CenterX=66 CenterY=19 CenterZ=0 NormalX=0 NormalY=0 NormalZ=1 AngleXU=0 Radius=1.8
    g5: Circle CenterX=86 CenterY=19 CenterZ=0 NormalX=0 NormalY=0 NormalZ=1 AngleXU=0 Radius=1.8
    g6: Circle CenterX=86 CenterY=4 CenterZ=0 NormalX=0 NormalY=0 NormalZ=1 AngleXU=0 Radius=1.8
    g7: Circle CenterX=66 CenterY=4 CenterZ=0 NormalX=0 NormalY=0 NormalZ=1 AngleXU=0 Radius=1.8
  constraints (24):
    c: Coincident(g0,g1)
    c: Coincident(g1,g2)
    c: Coincident(g2,g3)
    c: Coincident(g3,g0)
    c: Horizontal(g0)
    c: Horizontal(g2)
    c: Vertical(g1)
    c: Vertical(g3)
    c: DistanceX(g0,g0) = 27
    c: DistanceY(g1,g1) = 25
    c: Vertical(g7,g4)
    c: Vertical(g6,g5)
    c: Horizontal(g4,g5)
    c: Horizontal(g7,g6)
    c: DistanceX(g7,g6) = 20
    c: DistanceY(g6,g5) = 15
    c: Equal(g4,g5)
    c: Equal(g4,g6)
    c: Equal(g4,g7)
    c: Diameter(g4) = 3.6
    c: DistanceY(g0,g6) = 5
    c: DistanceX(g6,g0) = 3.5
    c: DistanceX(g5) = 86
    c: DistanceY(g5) = 19
FEATURE [PartDesign::Pad] Pad002
  BaseFeature = -> Pocket005
  Direction = (0,0,1)
  Length = 5
  Length2 = 10
  Placement = pos=(0,0,0) rot=(0.57735,0.57735,0.57735;2.0944rad)
  Profile = -> Sketch007
  ReferenceAxis = -> Sketch007 [N_Axis]
  Type = 0
FEATURE [PartDesign::LinearPattern] LinearPattern
  BaseFeature = -> Pad002
  Direction = -> Sketch007 [H_Axis]
  Length = 120
  Occurrences = 2
  Originals = -> [Pad002]
  Placement = pos=(0,0,0) rot=(0.57735,0.57735,0.57735;2.0944rad)
FEATURE [Sketcher::SketchObject] Sketch008
  AttachmentOffset = pos=(0,0,-36) rot=(0,0,1;0rad)
  FullyConstrained = true
  MapMode = 5
  Placement = pos=(-36,8e-15,-8e-15) rot=(0.57735,0.57735,0.57735;2.0944rad)
  Support = -> [YZ_Plane003]
  sketch-geometry (10):
    g0: LineSegment StartX=112 StartY=17 StartZ=0 EndX=-24 EndY=17 EndZ=0
    g1: LineSegment StartX=-24 StartY=17 StartZ=0 EndX=-24 EndY=-35 EndZ=0
    g2: LineSegment StartX=-24 StartY=-35 StartZ=0 EndX=112 EndY=-35 EndZ=0
    g3: LineSegment StartX=112 StartY=-35 StartZ=0 EndX=112 EndY=17 EndZ=0
    g4: Circle CenterX=-8.5 CenterY=9 CenterZ=0 NormalX=0 NormalY=0 NormalZ=1 AngleXU=0 Radius=3.15
    g5: Circle CenterX=9.5 CenterY=9 CenterZ=0 NormalX=0 NormalY=0 NormalZ=1 AngleXU=0 Radius=3.15
    g6: Circle CenterX=9.5 CenterY=-20 CenterZ=0 NormalX=0 NormalY=0 NormalZ=1 AngleXU=0 Radius=3.15
    g7: Circle CenterX=-8.5 CenterY=-20 CenterZ=0 NormalX=0 NormalY=0 NormalZ=1 AngleXU=0 Radius=3.15
    g8: Circle CenterX=55 CenterY=9 CenterZ=0 NormalX=0 NormalY=0 NormalZ=1 AngleXU=0 Radius=2.65
    g9: Circle CenterX=55 CenterY=-20 CenterZ=0 NormalX=0 NormalY=0 NormalZ=1 AngleXU=0 Radius=2.65
  constraints (30):
    c: Coincident(g0,g1)
    c: Coincident(g1,g2)
    c: Coincident(g2,g3)
    c: Coincident(g3,g0)
    c: Horizontal(g0)
    c: Horizontal(g2)
    c: Vertical(g1)
    c: Vertical(g3)
    c: Distance(g2) = 136
    c: Distance(g1) = 52
    c: DistanceY(g2) = -35
    c: DistanceX(g1) = -24
    c: Equal(g4,g5)
    c: Equal(g4,g6)
    c: Equal(g4,g7)
    c: Diameter(g4) = 6.3
    c: Vertical(g7,g4)
    c: Vertical(g6,g5)
    c: Horizontal(g4,g5)
    c: Horizontal(g7,g6)
    c: DistanceX(g7) = -8.5
    c: DistanceY(g6,g5) = 29
    c: DistanceY(g6) = -20
    c: DistanceX(g7,g6) = 18
    c: Horizontal(g5,g8)
    c: Horizontal(g6,g9)
    c: Vertical(g9,g8)
    c: DistanceX(g1,g9) = 79
    c: Equal(g8,g9)
    c: Diameter(g8) = 5.3
FEATURE [PartDesign::Pad] Pad003
  Direction = (1,-2e-16,3e-16)
  Length = 10
  Length2 = 10
  Placement = pos=(0,0,0) rot=(0.57735,0.57735,0.57735;2.0944rad)
  Profile = -> Sketch008
  ReferenceAxis = -> Sketch008 [N_Axis]
  Reversed = true
  Type = 0
FEATURE [Sketcher::SketchObject] Sketch010
  AttachmentOffset = pos=(0,4,0) rot=(0,0,1;0rad)
  FullyConstrained = true
  MapMode = 5
  Placement = pos=(0,4,0) rot=(0,0,1;0rad)
  Support = -> [XY_Plane003]
  sketch-geometry (8):
    g0: LineSegment StartX=-36 StartY=42 StartZ=0 EndX=-26 EndY=42 EndZ=0
    g1: LineSegment StartX=-26 StartY=42 StartZ=0 EndX=-26 EndY=35 EndZ=0
    g2: LineSegment StartX=-26 StartY=35 StartZ=0 EndX=-36 EndY=35 EndZ=0
    g3: LineSegment StartX=-36 StartY=35 StartZ=0 EndX=-36 EndY=42 EndZ=0
    g4: LineSegment StartX=-36 StartY=21 StartZ=0 EndX=-26 EndY=21 EndZ=0
    g5: LineSegment StartX=-26 StartY=21 StartZ=0 EndX=-26 EndY=14 EndZ=0
    g6: LineSegment StartX=-26 StartY=14 StartZ=0 EndX=-36 EndY=14 EndZ=0
    g7: LineSegment StartX=-36 StartY=14 StartZ=0 EndX=-36 EndY=21 EndZ=0
  constraints (24):
    c: Coincident(g0,g1)
    c: Coincident(g1,g2)
    c: Coincident(g2,g3)
    c: Coincident(g3,g0)
    c: Horizontal(g0)
    c: Horizontal(g2)
    c: Vertical(g1)
    c: Vertical(g3)
    c: Coincident(g4,g5)
    c: Coincident(g5,g6)
    c: Coincident(g6,g7)
    c: Coincident(g7,g4)
    c: Horizontal(g4)
    c: Horizontal(g6)
    c: Vertical(g5)
    c: Vertical(g7)
    c: Vertical(g4,g2)
    c: DistanceX(g6) = -36
    c: Vertical(g4,g1)
    c: Equal(g1,g5)
    c: Distance(g6) = 10
    c: Distance(g5) = 7
    c: DistanceY(g6) = 14
    c: DistanceY(g4,g0) = 21
FEATURE [PartDesign::Pad] Pad005
  BaseFeature = -> Pad003
  Direction = (0,0,1)
  Length = 8
  Length2 = 10
  Midplane = true
  Placement = pos=(0,0,0) rot=(0.57735,0.57735,0.57735;2.0944rad)
  Profile = -> Sketch010
  ReferenceAxis = -> Sketch010 [N_Axis]
  Type = 0
FEATURE [Sketcher::SketchObject] Sketch011
  AttachmentOffset = pos=(4,0,-26) rot=(0,0,1;0rad)
  FullyConstrained = true
  MapMode = 5
  Placement = pos=(-26,4,-6.7e-15) rot=(0.57735,0.57735,0.57735;2.0944rad)
  Support = -> [YZ_Plane003]
  sketch-geometry (2):
    g0: Circle CenterX=38.5 CenterY=0 CenterZ=0 NormalX=0 NormalY=0 NormalZ=1 AngleXU=0 Radius=2.1
    g1: Circle CenterX=17.5 CenterY=0 CenterZ=0 NormalX=0 NormalY=0 NormalZ=1 AngleXU=0 Radius=2.1
  constraints (6):
    c: PointOnObject(g0,g-1)
    c: PointOnObject(g1,g-1)
    c: Distance(g1,g0) = 21
    c: Equal(g1,g0)
    c: Diameter(g1) = 4.2
    c: DistanceX(g1) = 17.5
FEATURE [PartDesign::Pocket] Pocket006
  BaseFeature = -> Pad005
  Direction = (-1,2e-16,-3e-16)
  Length = 5
  Length2 = 5
  Placement = pos=(0,0,0) rot=(0.57735,0.57735,0.57735;2.0944rad)
  Profile = -> Sketch011
  ReferenceAxis = -> Sketch011 [N_Axis]
  Type = 1
FEATURE [Sketcher::SketchObject] Sketch012
  AttachmentOffset = pos=(0,0,68) rot=(0,0,1;0rad)
  FullyConstrained = true
  MapMode = 5
  Placement = pos=(68,-1.51e-14,1.51e-14) rot=(0.57735,0.57735,0.57735;2.0944rad)
  Support = -> [YZ_Plane004]
  sketch-geometry (12):
    g0: LineSegment StartX=-8 StartY=17 StartZ=0 EndX=112 EndY=17 EndZ=0
    g1: LineSegment StartX=112 StartY=17 StartZ=0 EndX=112 EndY=-35 EndZ=0
    g2: LineSegment StartX=112 StartY=-35 StartZ=0 EndX=-12.5 EndY=-35 EndZ=0
    g3: LineSegment StartX=-12.5 StartY=-35 StartZ=0 EndX=-12.5 EndY=-17.9911 EndZ=0
    g4: ArcOfCircle CenterX=-32 CenterY=-4 CenterZ=0 NormalX=0 NormalY=0 NormalZ=1 AngleXU=0 Radius=24 StartAngle=5.66082 EndAngle=6.28319
    g5: Circle CenterX=41 CenterY=8 CenterZ=0 NormalX=0 NormalY=0 NormalZ=1 AngleXU=0 Radius=2.1
    g6: Circle CenterX=41 CenterY=-12 CenterZ=0 NormalX=0 NormalY=0 NormalZ=1 AngleXU=0 Radius=2.1
    g7: Circle CenterX=75 CenterY=-24 CenterZ=0 NormalX=0 NormalY=0 NormalZ=1 AngleXU=0 Radius=2.1
    g8: Circle CenterX=25 CenterY=-24 CenterZ=0 NormalX=0 NormalY=0 NormalZ=1 AngleXU=0 Radius=2.1
    g9: Circle CenterX=25 CenterY=6 CenterZ=0 NormalX=0 NormalY=0 NormalZ=1 AngleXU=0 Radius=2.1
    g10: Circle CenterX=75 CenterY=6 CenterZ=0 NormalX=0 NormalY=0 NormalZ=1 AngleXU=0 Radius=2.1
    g11: LineSegment StartX=-8 StartY=17 StartZ=0 EndX=-8 EndY=-4 EndZ=0
  constraints (36):
    c: Coincident(g0,g1)
    c: Coincident(g1,g2)
    c: Coincident(g2,g3)
    c: Horizontal(g0)
    c: Horizontal(g2)
    c: Vertical(g1)
    c: Vertical(g3)
    c: Distance(g1) = 52
    c: DistanceY(g2) = -35
    c: Diameter(g4) = 48
    c: DistanceX(g4) = -32
    c: Coincident(g3,g4)
    c: Vertical(g6,g5)
    c: Equal(g5,g6)
    c: Diameter(g5) = 4.2
    c: DistanceY(g5) = 8
    c: DistanceX(g5) = 41
    c: Distance(g5,g6) = 20
    c: Diameter(g8) = 4.2
    c: Vertical(g9,g8)
    c: Vertical(g7,g10)
    c: Horizontal(g9,g10)
    c: Equal(g7,g10)
    c: Equal(g10,g9)
    c: Distance(g8,g9) = 30
    c: DistanceY(g4) = -4
    c: Coincident(g11,g0)
    c: Tangent(g11,g4) = 1.5708
    c: Vertical(g11)
    c: DistanceX(g1) = 112
    c: Distance(g2) = 124.5
    c: DistanceX(g8) = 25
    c: DistanceY(g8) = -24
    c: Distance(g8,g7) = 50
    c: Horizontal(g8,g7)
    c: Equal(g8,g9)
FEATURE [PartDesign::Pad] Pad006
  Direction = (1,-2e-16,3e-16)
  Length = 10
  Length2 = 10
  Placement = pos=(0,0,0) rot=(0.57735,0.57735,0.57735;2.0944rad)
  Profile = -> Sketch012
  ReferenceAxis = -> Sketch012 [N_Axis]
  Type = 0
FEATURE [PartDesign::CoordinateSystem] LCS_1
  AttacherType = Attacher::AttachEngine3D
FEATURE [PartDesign::Body] Body004  label="Front_IR_Tab"
  Origin = -> Origin005
FEATURE [PartDesign::Chamfer] Chamfer
  Angle = 45
  Base = -> Pocket006 [Edge4,Edge3,Edge2,Edge1,Edge9,Edge10,Edge8,Edge7,Face2,Edge6,Edge11,Edge26]
  BaseFeature = -> Pocket006
  ChamferType = 0
  FlipDirection = false
  Placement = pos=(0,0,0) rot=(0.57735,0.57735,0.57735;2.0944rad)
  Size = 1
  Size2 = 1
  SupportTransform = false
  UseAllEdges = false
FEATURE [PartDesign::Chamfer] Chamfer001
  Angle = 45
  Base = -> Pad006 [Edge7,Edge6,Edge2,Edge4,Face1,Edge1,Edge13,Edge18,Edge16,Edge12,Edge15,Edge17,Edge10,Edge9]
  BaseFeature = -> Pad006
  ChamferType = 0
  FlipDirection = false
  Placement = pos=(0,0,0) rot=(0.57735,0.57735,0.57735;2.0944rad)
  Size = 1
  Size2 = 1
  SupportTransform = false
  UseAllEdges = false
FEATURE [PartDesign::Body] Body003  label="RHS"
  Group = -> [Sketch012,Pad006,Chamfer001]
  Origin = -> Origin004
  Tip = -> Chamfer001
FEATURE [PartDesign::Chamfer] Chamfer002
  Angle = 45
  Base = -> LinearPattern [Edge125,Edge123,Edge124,Edge121,Edge119]
  BaseFeature = -> LinearPattern
  ChamferType = 0
  FlipDirection = false
  Placement = pos=(0,0,0) rot=(0.57735,0.57735,0.57735;2.0944rad)
  Size = 1
  Size2 = 1
  SupportTransform = false
  UseAllEdges = false
FEATURE [PartDesign::Chamfer] Chamfer003
  Angle = 45
  Base = -> Chamfer002 [Edge79,Edge78,Edge74,Edge75,Edge152,Edge156,Edge151,Edge76]
  BaseFeature = -> Chamfer002
  ChamferType = 0
  FlipDirection = false
  Placement = pos=(0,0,0) rot=(0.57735,0.57735,0.57735;2.0944rad)
  Size = 1
  Size2 = 1
  SupportTransform = false
  UseAllEdges = false
FEATURE [PartDesign::Body] Body  label="Front"
  Group = -> [Sketch,Pad,Sketch002,Pocket001,Sketch004,Pocket003,Sketch005,Pocket004,Sketch006,Pad001,Sketch003,Pocket,Sketch001,Pocket005,Sketch007,Pad002,LinearPattern,Chamfer002,Chamfer003]
  Origin = -> Origin
  Tip = -> Chamfer003
FEATURE [PartDesign::FeatureBase] Clone
  BaseFeature = -> Body
FEATURE [PartDesign::Body] Body001  label="Rear"
  BaseFeature = -> Body
  Group = -> [Clone]
  Origin = -> Origin002
  Placement = pos=(0,100,0) rot=(0,0,1;0rad)
  Tip = -> Clone
FEATURE [PartDesign::Chamfer] Chamfer004
  Angle = 45
  Base = -> Pocket006 [Face3,Face1,Face2,Face6]
  BaseFeature = -> Pocket006
  ChamferType = 0
  FlipDirection = false
  Placement = pos=(0,0,0) rot=(0.57735,0.57735,0.57735;2.0944rad)
  Size = 1
  Size2 = 1
  SupportTransform = false
  UseAllEdges = false
FEATURE [PartDesign::Body] Body002  label="LHS"
  Group = -> [Sketch008,Pad003,Sketch010,Pad005,Sketch011,Pocket006,Chamfer,Chamfer004]
  Origin = -> Origin003
  Placement = pos=(-6,0,0) rot=(0,0,1;0rad)
  Tip = -> Chamfer004
FEATURE [App::Part] Part  label="Frame"
  Group = -> [Body,Body002,Body003,Body001,LCS_1,Body004]
  Origin = -> Origin001
---- part Parts/Frame_Roll_Limit_IR_Sensor_Mount.FCStd = doc fcstd_48ffcfb0d0f1 ----
FCSTD DOCUMENT  (FreeCAD 0.21R32110 (Git))
Label: Frame_Roll_Limit_IR_Sensor_Mount
License: All rights reserved
LicenseURL: http://en.wikipedia.org/wiki/All_rights_reserved
objects: Sketcher::SketchObject×6, PartDesign::Pad×3, PartDesign::Pocket×3, PartDesign::Plane×1, PartDesign::Mirrored×1, PartDesign::Body×1
note: 21 computed .brp shape members not serialized (recipe doc carries the construction recipe); baked Part::Feature solids carry a one-line shape summary decoded from their .brp

FEATURE [Sketcher::SketchObject] Sketch097
  AttachmentOffset = pos=(0,0,-27) rot=(0,0,1;0rad)
  FullyConstrained = true
  MapMode = 5
  Placement = pos=(0,27,6e-15) rot=(1,0,0;1.5708rad)
  Support = -> [XZ_Plane031]
  sketch-geometry (7):
    g0: LineSegment StartX=25.8209 StartY=-22.5023 StartZ=0 EndX=19.68 EndY=-28.0316 EndZ=0
    g1: LineSegment StartX=19.68 StartY=-35 StartZ=0 EndX=24 EndY=-35 EndZ=0
    g2: LineSegment StartX=0 StartY=0 StartZ=0 EndX=22.7504 EndY=-25.2669 EndZ=0
    g3: LineSegment StartX=24 StartY=-32.2156 StartZ=0 EndX=24 EndY=-35 EndZ=0
    g4: LineSegment StartX=19.68 StartY=-35 StartZ=0 EndX=19.68 EndY=-28.0316 EndZ=0
    g5: LineSegment StartX=24 StartY=-32.2156 StartZ=0 EndX=29.8357 EndY=-26.9612 EndZ=0
    g6: LineSegment StartX=25.8209 StartY=-22.5023 StartZ=0 EndX=29.8357 EndY=-26.9612 EndZ=0
  constraints (20):
    c: Horizontal(g1)
    c: DistanceY(g1) = -35
    c: Coincident(g2,g-1)
    c: Angle(g2,g0) = 1.5708
    c: Coincident(g3,g1)
    c: Vertical(g3)
    c: Symmetric(g0,g0,g2)
    c: Coincident(g4,g1)
    c: Vertical(g4)
    c: Angle(g2,g-1) = 0.837758
    c: Distance(g2,g2) = 34
    c: Parallel(g0,g5)
    c: Coincident(g6,g0)
    c: Coincident(g6,g5)
    c: Angle(g0,g6) = 1.5708
    c: Coincident(g3,g5)
    c: Distance(g6) = 6
    c: Coincident(g4,g0)
    c: Distance(g1) = 4.32
    c: DistanceX(g1) = 24
FEATURE [PartDesign::Pad] Pad054
  Direction = (0,-1,-2e-16)
  Length = 33
  Length2 = 10
  Placement = pos=(0,0,0) rot=(1,0,0;1.5708rad)
  Profile = -> Sketch097
  ReferenceAxis = -> Sketch097 [N_Axis]
  Reversed = true
  Type = 0
FEATURE [PartDesign::Plane] DatumPlane
  Length = 82.4977
  MapMode = 5
  Placement = pos=(22.7504,-5.6e-15,-25.2669) rot=(-0.358368,0,0.93358;3.14159rad)
  ResizeMode = 0
  Support = -> [Pad054]
  Width = 61.8839
FEATURE [Sketcher::SketchObject] Sketch098
  AttachmentOffset = pos=(0,0.75,0) rot=(0,0,1;0rad)
  FullyConstrained = true
  MapMode = 5
  Placement = pos=(22.7504,-0.75,-25.2669) rot=(-0.358368,0,0.93358;3.14159rad)
  Support = -> [DatumPlane]
  sketch-geometry (2):
    g0: Circle CenterX=0 CenterY=-55.75 CenterZ=0 NormalX=0 NormalY=0 NormalZ=1 AngleXU=0 Radius=2.2
    g1: Circle CenterX=0 CenterY=-34.75 CenterZ=0 NormalX=0 NormalY=0 NormalZ=1 AngleXU=0 Radius=2.2
  constraints (6):
    c: PointOnObject(g0,g-2)
    c: PointOnObject(g1,g-2)
    c: DistanceY(g0,g1) = 21
    c: DistanceY(g1) = -34.75
    c: Equal(g0,g1)
    c: Diameter(g0) = 4.4
FEATURE [PartDesign::Pocket] Pocket034
  BaseFeature = -> Pad054
  Direction = (0.669131,-2e-16,-0.743145)
  Length = 5
  Length2 = 5
  Placement = pos=(0,0,0) rot=(1,0,0;1.5708rad)
  Profile = -> Sketch098
  ReferenceAxis = -> Sketch098 [N_Axis]
  Type = 1
FEATURE [Sketcher::SketchObject] Sketch099
  AttachmentOffset = pos=(0,0.75,0) rot=(0,0,1;0rad)
  FullyConstrained = true
  MapMode = 5
  Placement = pos=(22.7504,-0.75,-25.2669) rot=(-0.358368,0,0.93358;3.14159rad)
  Support = -> [DatumPlane]
  sketch-geometry (4):
    g0: LineSegment StartX=-7 StartY=-38.25 StartZ=0 EndX=7 EndY=-38.25 EndZ=0
    g1: LineSegment StartX=7 StartY=-38.25 StartZ=0 EndX=7 EndY=-52.25 EndZ=0
    g2: LineSegment StartX=7 StartY=-52.25 StartZ=0 EndX=-7 EndY=-52.25 EndZ=0
    g3: LineSegment StartX=-7 StartY=-52.25 StartZ=0 EndX=-7 EndY=-38.25 EndZ=0
  constraints (11):
    c: Coincident(g0,g1)
    c: Coincident(g1,g2)
    c: Coincident(g2,g3)
    c: Coincident(g3,g0)
    c: Horizontal(g2)
    c: Vertical(g1)
    c: Vertical(g3)
    c: DistanceY(g1,g1) = 14
    c: DistanceX(g2,g2) = 14
    c: Symmetric(g0,g0,g-2)
    c: DistanceY(g0) = -38.25
FEATURE [PartDesign::Pocket] Pocket035
  BaseFeature = -> Pocket034
  Direction = (0.669131,-2e-16,-0.743145)
  Length = 1.5
  Length2 = 5
  Placement = pos=(0,0,0) rot=(1,0,0;1.5708rad)
  Profile = -> Sketch099
  ReferenceAxis = -> Sketch099 [N_Axis]
  Type = 0
FEATURE [Sketcher::SketchObject] Sketch100
  AttachmentOffset = pos=(0,0,-27) rot=(0,0,1;0rad)
  FullyConstrained = true
  MapMode = 5
  Placement = pos=(0,27,6e-15) rot=(1,0,0;1.5708rad)
  Support = -> [XZ_Plane031]
  sketch-geometry (8):
    g0: LineSegment StartX=17.3775 StartY=-24.25 StartZ=0 EndX=9.3775 EndY=-24.25 EndZ=0
    g1: LineSegment StartX=-21.5 StartY=-29.2 StartZ=0 EndX=-21.5 EndY=-35 EndZ=0
    g2: LineSegment StartX=-21.5 StartY=-35 StartZ=0 EndX=21.5 EndY=-35 EndZ=0
    g3: ArcOfCircle CenterX=0 CenterY=0 CenterZ=0 NormalX=0 NormalY=0 NormalZ=1 AngleXU=0 Radius=26 StartAngle=4.3434 EndAngle=5.08138
    g4: LineSegment StartX=-9.3775 StartY=-24.25 StartZ=0 EndX=-17.3775 EndY=-24.25 EndZ=0
    g5: LineSegment StartX=21.5 StartY=-35 StartZ=0 EndX=21.5 EndY=-29.2 EndZ=0
    g6: LineSegment StartX=21.5 StartY=-29.2 StartZ=0 EndX=17.3775 EndY=-24.25 EndZ=0
    g7: LineSegment StartX=-21.5 StartY=-29.2 StartZ=0 EndX=-17.3775 EndY=-24.25 EndZ=0
  constraints (23):
    c: Coincident(g1,g2)
    c: Vertical(g1)
    c: DistanceY(g2) = -35
    c: Coincident(g3,g-1)
    c: Coincident(g0,g3)
    c: Coincident(g4,g3)
    c: Horizontal(g3,g0)
    c: Horizontal(g4)
    c: Diameter(g3) = 52
    c: Symmetric(g1,g2,g-2)
    c: Coincident(g5,g2)
    c: Vertical(g5)
    c: Coincident(g6,g5)
    c: Coincident(g6,g0)
    c: Coincident(g7,g1)
    c: Coincident(g7,g4)
    c: Equal(g5,g1)
    c: Distance(g4) = 8
    c: Equal(g4,g0)
    c: Distance(g2) = 43
    c: Distance(g1) = 5.8
    c: Horizontal(g0)
    c: DistanceY(g1,g4) = 10.75
FEATURE [PartDesign::Pad] Pad055
  BaseFeature = -> Pocket035
  Direction = (0,-1,-2e-16)
  Length = 6
  Length2 = 10
  Placement = pos=(0,0,0) rot=(1,0,0;1.5708rad)
  Profile = -> Sketch100
  ReferenceAxis = -> Sketch100 [N_Axis]
  Reversed = true
  Type = 0
FEATURE [Sketcher::SketchObject] Sketch101
  AttachmentOffset = pos=(0,0,-33) rot=(0,0,1;0rad)
  FullyConstrained = true
  MapMode = 5
  Placement = pos=(0,33,7.3e-15) rot=(1,0,0;1.5708rad)
  Support = -> [XZ_Plane031]
  sketch-geometry (2):
    g0: Circle CenterX=-10 CenterY=-28 CenterZ=0 NormalX=0 NormalY=0 NormalZ=1 AngleXU=0 Radius=2.15
    g1: Circle CenterX=10 CenterY=-28 CenterZ=0 NormalX=0 NormalY=0 NormalZ=1 AngleXU=0 Radius=2.15
  constraints (5):
    c: Equal(g0,g1)
    c: Diameter(g0) = 4.3
    c: Symmetric(g0,g1,g-2)
    c: DistanceY(g0) = -28
    c: DistanceX(g0) = -10
FEATURE [Sketcher::SketchObject] Sketch102
  AttachmentOffset = pos=(0,1,-35) rot=(0,0,1;0rad)
  FullyConstrained = true
  MapMode = 5
  Placement = pos=(0,1,-35) rot=(0,0,1;0rad)
  Support = -> [XY_Plane031]
  sketch-geometry (4):
    g0: LineSegment StartX=-20 StartY=59 StartZ=0 EndX=20 EndY=59 EndZ=0
    g1: LineSegment StartX=20 StartY=59 StartZ=0 EndX=20 EndY=53.5 EndZ=0
    g2: LineSegment StartX=20 StartY=53.5 StartZ=0 EndX=-20 EndY=53.5 EndZ=0
    g3: LineSegment StartX=-20 StartY=53.5 StartZ=0 EndX=-20 EndY=59 EndZ=0
  constraints (11):
    c: Coincident(g0,g1)
    c: Coincident(g1,g2)
    c: Coincident(g2,g3)
    c: Coincident(g3,g0)
    c: Horizontal(g0)
    c: Vertical(g1)
    c: Vertical(g3)
    c: DistanceY(g0) = 59
    c: Distance(g1) = 5.5
    c: Distance(g2) = 40
    c: Symmetric(g2,g1,g-2)
FEATURE [PartDesign::Mirrored] Mirrored
  BaseFeature = -> Pad055
  MirrorPlane = -> Sketch097 [V_Axis]
  Originals = -> [Pad054,Pocket034,Pocket035]
  Placement = pos=(0,0,0) rot=(1,0,0;1.5708rad)
FEATURE [PartDesign::Pocket] Pocket036
  BaseFeature = -> Mirrored
  Direction = (0,1,2e-16)
  Length = 5
  Length2 = 5
  Placement = pos=(0,0,0) rot=(1,0,0;1.5708rad)
  Profile = -> Sketch101
  ReferenceAxis = -> Sketch101 [N_Axis]
  Reversed = true
  Type = 1
FEATURE [PartDesign::Pad] Pad
  BaseFeature = -> Pocket036
  Direction = (0,0,1)
  Length = 6.8
  Length2 = 10
  Placement = pos=(0,0,0) rot=(1,0,0;1.5708rad)
  Profile = -> Sketch102
  ReferenceAxis = -> Sketch102 [N_Axis]
  Type = 0
FEATURE [PartDesign::Body] Body022  label="Frame_Roll_IR_Sensor_Mount"
  Group = -> [Sketch097,Pad054,DatumPlane,Sketch098,Sketch099,Pocket034,Pocket035,Sketch100,Pad055,Mirrored,Sketch101,Pocket036,Sketch102,Pad]
  Origin = -> Origin031
  Tip = -> Pad
---- part Parts/Frame_Roll_Limit_Stop.FCStd = doc fcstd_30771d60c532 ----
FCSTD DOCUMENT  (FreeCAD 0.21R32110 (Git))
Label: Frame_Roll_Limit_Stop
License: All rights reserved
LicenseURL: http://en.wikipedia.org/wiki/All_rights_reserved
objects: Sketcher::SketchObject×3, PartDesign::Pad×1, PartDesign::Pocket×1, PartDesign::Hole×1, PartDesign::Body×1
note: 10 computed .brp shape members not serialized (recipe doc carries the construction recipe); baked Part::Feature solids carry a one-line shape summary decoded from their .brp

FEATURE [Sketcher::SketchObject] Sketch078
  AttachmentOffset = pos=(0,0,-27) rot=(0,0,1;0rad)
  FullyConstrained = false
  MapMode = 5
  Placement = pos=(0,27,6e-15) rot=(1,0,0;1.5708rad)
  Support = -> [XZ_Plane028]
  sketch-geometry (8):
    g0: LineSegment StartX=-23.5 StartY=-35 StartZ=0 EndX=23.5 EndY=-35 EndZ=0
    g1: LineSegment StartX=23.5 StartY=-35 StartZ=0 EndX=23.5 EndY=-23.5 EndZ=0
    g2: LineSegment StartX=-23.5 StartY=-23.5 StartZ=0 EndX=-23.5 EndY=-35 EndZ=0
    g3: LineSegment StartX=0 StartY=0 StartZ=0 EndX=23.5001 EndY=-23.5001 EndZ=0
    g4: LineSegment StartX=0 StartY=0 StartZ=0 EndX=-23.5 EndY=-23.5 EndZ=0
    g5: ArcOfCircle CenterX=0 CenterY=0 CenterZ=0 NormalX=0 NormalY=0 NormalZ=1 AngleXU=0 Radius=20.5 StartAngle=3.92699 EndAngle=5.49779
    g6: LineSegment StartX=14.4957 StartY=-14.4957 StartZ=0 EndX=23.5 EndY=-23.5 EndZ=0
    g7: LineSegment StartX=-23.5 StartY=-23.5 StartZ=0 EndX=-14.4957 EndY=-14.4957 EndZ=0
  constraints (21):
    c: Coincident(g0,g1)
    c: Coincident(g2,g0)
    c: Vertical(g1)
    c: Vertical(g2)
    c: Symmetric(g0,g0,g-2)
    c: DistanceX(g0,g0) = 47
    c: Coincident(g3,g-1)
    c: Coincident(g4,g3)
    c: Angle(g4) = -2.35619
    c: Angle(g3) = -0.785398
    c: Coincident(g5,g3)
    c: Diameter(g5) = 41
    c: PointOnObject(g5,g3)
    c: PointOnObject(g5,g4)
    c: Coincident(g6,g5)
    c: Coincident(g6,g1)
    c: Coincident(g4,g2)
    c: Equal(g2,g1)
    c: Coincident(g7,g2)
    c: Coincident(g7,g5)
    c: DistanceY(g0) = -35
FEATURE [PartDesign::Pad] Pad046
  Direction = (0,-1,-2e-16)
  Length = 22
  Length2 = 10
  Placement = pos=(0,0,0) rot=(1,0,0;1.5708rad)
  Profile = -> Sketch078
  ReferenceAxis = -> Sketch078 [N_Axis]
  Reversed = true
  Type = 0
FEATURE [Sketcher::SketchObject] Sketch
  AttachmentOffset = pos=(0,0,-27) rot=(0,0,1;0rad)
  FullyConstrained = true
  MapMode = 5
  Placement = pos=(0,27,6e-15) rot=(1,0,0;1.5708rad)
  Support = -> [XZ_Plane028]
  sketch-geometry (1):
    g0: Circle CenterX=0 CenterY=0 CenterZ=0 NormalX=0 NormalY=0 NormalZ=1 AngleXU=0 Radius=25
  constraints (2):
    c: Coincident(g0,g-1)
    c: Diameter(g0) = 50
FEATURE [PartDesign::Pocket] Pocket
  BaseFeature = -> Pad046
  Direction = (0,1,2e-16)
  Length = 6
  Length2 = 5
  Placement = pos=(0,0,0) rot=(1,0,0;1.5708rad)
  Profile = -> Sketch
  ReferenceAxis = -> Sketch [N_Axis]
  Type = 0
FEATURE [Sketcher::SketchObject] Sketch079
  AttachmentOffset = pos=(0,0,-49) rot=(0,0,1;0rad)
  FullyConstrained = true
  MapMode = 5
  Placement = pos=(0,49,1.09e-14) rot=(1,0,0;1.5708rad)
  Support = -> [XZ_Plane028]
  sketch-geometry (2):
    g0: Circle CenterX=-10 CenterY=-28 CenterZ=0 NormalX=0 NormalY=0 NormalZ=1 AngleXU=0 Radius=2.25
    g1: Circle CenterX=10 CenterY=-28 CenterZ=0 NormalX=0 NormalY=0 NormalZ=1 AngleXU=0 Radius=2.25
  constraints (5):
    c: Symmetric(g0,g1,g-2)
    c: Distance(g0,g1) = 20
    c: Equal(g0,g1)
    c: Diameter(g0) = 4.5
    c: DistanceY(g1) = -28
FEATURE [PartDesign::Hole] Hole
  BaseFeature = -> Pocket
  CustomThreadClearance = 0
  Depth = 112.712
  DepthType = 1
  Diameter = 4.5
  DrillForDepth = false
  DrillPoint = 1
  DrillPointAngle = 118
  HoleCutCountersinkAngle = 90
  HoleCutCustomValues = false
  HoleCutDepth = 4.4
  HoleCutDiameter = 7.4
  HoleCutType = 1
  ModelThread = false
  Placement = pos=(0,0,0) rot=(1,0,0;1.5708rad)
  Profile = -> Sketch079
  Reversed = true
  Tapered = false
  TaperedAngle = 90
  ThreadClass = 0
  ThreadDepth = 112.712
  ThreadDepthType = 0
  ThreadDirection = 0
  ThreadFit = 0
  ThreadSize = 11
  ThreadType = 1
  Threaded = false
  UseCustomThreadClearance = false
FEATURE [PartDesign::Body] Body019  label="Roll limit stop"
  Group = -> [Sketch078,Pad046,Sketch,Pocket,Sketch079,Hole]
  Origin = -> Origin028
  Tip = -> Hole
---- part Parts/GearMotor.FCStd = doc fcstd_35677846020b ----
FCSTD DOCUMENT  (FreeCAD 0.21R32110 (Git))
Label: GearMotor
License: All rights reserved
LicenseURL: http://en.wikipedia.org/wiki/All_rights_reserved
objects: Sketcher::SketchObject×3, PartDesign::Pad×3, PartDesign::Body×1, App::Part×1
note: 10 computed .brp shape members not serialized (recipe doc carries the construction recipe); baked Part::Feature solids carry a one-line shape summary decoded from their .brp

FEATURE [Sketcher::SketchObject] Sketch003
  FullyConstrained = false
  MapMode = 5
  Placement = pos=(-7,2,-25.5) rot=(1,0,0;1.5708rad)
  sketch-geometry (1):
    g0: Circle CenterX=-68 CenterY=20 CenterZ=0 NormalX=0 NormalY=0 NormalZ=1 AngleXU=0 Radius=22.5
  constraints (2):
    c: Diameter(g0) = 45
    c: DistanceX(g0) = -68
FEATURE [PartDesign::Pad] Pad003  label="Gear_Motor"
  Direction = (0,-1,0)
  Length = 120
  Length2 = 10
  Placement = pos=(-7,2,-25.5) rot=(1,0,0;1.5708rad)
  Profile = -> Sketch003
  ReferenceAxis = -> Sketch003 [N_Axis]
  Reversed = true
  Type = 0
FEATURE [Sketcher::SketchObject] Sketch
  AttachmentOffset = pos=(0,0,1) rot=(0,0,1;0rad)
  FullyConstrained = true
  MapMode = 5
  Placement = pos=(0,-1,-2e-16) rot=(1,0,0;1.5708rad)
  Support = -> [XZ_Plane001]
  sketch-geometry (1):
    g0: Circle CenterX=-75 CenterY=-5 CenterZ=0 NormalX=0 NormalY=0 NormalZ=1 AngleXU=0 Radius=5
  constraints (3):
    c: Diameter(g0) = 10
    c: DistanceY(g0) = -5
    c: DistanceX(g0) = -75
FEATURE [PartDesign::Pad] Pad
  Direction = (0,-1,-2e-16)
  Length = 23.5
  Length2 = 10
  Placement = pos=(0,0,0) rot=(1,0,0;1.5708rad)
  Profile = -> Sketch
  ReferenceAxis = -> Sketch [N_Axis]
  Type = 0
FEATURE [Sketcher::SketchObject] Sketch004
  AttachmentOffset = pos=(0,0,-2) rot=(0,0,1;0rad)
  FullyConstrained = false
  MapMode = 5
  Placement = pos=(0,2,4e-16) rot=(1,0,0;1.5708rad)
  Support = -> [XZ_Plane001]
  sketch-geometry (1):
    g0: Circle CenterX=-74.9703 CenterY=-5.13394 CenterZ=0 NormalX=0 NormalY=0 NormalZ=1 AngleXU=0 Radius=10
  constraints (1):
    c: Diameter(g0) = 20
FEATURE [PartDesign::Pad] Pad004
  BaseFeature = -> Pad
  Direction = (0,-1,-2e-16)
  Length = 3
  Length2 = 10
  Placement = pos=(0,0,0) rot=(1,0,0;1.5708rad)
  Profile = -> Sketch004
  ReferenceAxis = -> Sketch004 [N_Axis]
  Type = 0
FEATURE [PartDesign::Body] Body
  Group = -> [Sketch,Pad,Sketch004,Pad004]
  Origin = -> Origin001
  Tip = -> Pad004
FEATURE [App::Part] Part
  Group = -> [Sketch003,Pad003,Body]
  Origin = -> Origin
---- part Parts/Roll_Encoder_Mount.FCStd = doc fcstd_f4d863fa154e ----
FCSTD DOCUMENT  (FreeCAD 0.21R33668 +26 (Git))
Label: Roll_Encoder_Mount
License: All rights reserved
LicenseURL: http://en.wikipedia.org/wiki/All_rights_reserved
objects: PartDesign::Chamfer×6, Sketcher::SketchObject×5, PartDesign::Pad×4, PartDesign::Pocket×1, PartDesign::Body×1
note: 28 computed .brp shape members not serialized (recipe doc carries the construction recipe); baked Part::Feature solids carry a one-line shape summary decoded from their .brp

FEATURE [Sketcher::SketchObject] Sketch124
  AttachmentOffset = pos=(1,-14,-75) rot=(0,0,1;0rad)
  FullyConstrained = true
  MapMode = 5
  Placement = pos=(1,75,-14) rot=(1,0,0;1.5708rad)
  Support = -> [XZ_Plane043]
  sketch-geometry (23):
    g0: LineSegment StartX=33 StartY=31 StartZ=0 EndX=66 EndY=31 EndZ=0
    g1: LineSegment StartX=66 StartY=31 StartZ=0 EndX=66 EndY=-7 EndZ=0
    g2: LineSegment StartX=66 StartY=-7 StartZ=0 EndX=33 EndY=-7 EndZ=0
    g3: ArcOfCircle CenterX=33 CenterY=12 CenterZ=0 NormalX=0 NormalY=0 NormalZ=1 AngleXU=0 Radius=19 StartAngle=1.5708 EndAngle=4.71239
    g4: LineSegment StartX=33 StartY=22.25 StartZ=0 EndX=36 EndY=22.25 EndZ=0
    g5: LineSegment StartX=36 StartY=1.75 StartZ=0 EndX=33 EndY=1.75 EndZ=0
    g6: ArcOfCircle CenterX=51 CenterY=11.86 CenterZ=0 NormalX=0 NormalY=0 NormalZ=1 AngleXU=0 Radius=1.75 StartAngle=4.71239 EndAngle=7.85398
    g7: LineSegment StartX=51 StartY=10.11 StartZ=0 EndX=46.0742 EndY=10.11 EndZ=0
    g8: LineSegment StartX=51 StartY=13.61 StartZ=0 EndX=46.1228 EndY=13.61 EndZ=0
    g9: ArcOfCircle CenterX=33 CenterY=12 CenterZ=0 NormalX=0 NormalY=0 NormalZ=1 AngleXU=0 Radius=10.25 StartAngle=1.5708 EndAngle=4.71239
    g10: ArcOfCircle CenterX=36 CenterY=12 CenterZ=0 NormalX=0 NormalY=0 NormalZ=1 AngleXU=0 Radius=10.25 StartAngle=4.71239 EndAngle=6.09773
    g11: ArcOfCircle CenterX=36 CenterY=12 CenterZ=0 NormalX=0 NormalY=0 NormalZ=1 AngleXU=0 Radius=10.25 StartAngle=0.157726 EndAngle=1.5708
    g12: ArcOfCircle CenterX=25.57 CenterY=24.41 CenterZ=0 NormalX=0 NormalY=0 NormalZ=1 AngleXU=0 Radius=1.6 StartAngle=1.5708 EndAngle=4.71239
    g13: ArcOfCircle CenterX=30.57 CenterY=24.41 CenterZ=0 NormalX=0 NormalY=0 NormalZ=1 AngleXU=0 Radius=1.6 StartAngle=4.71239 EndAngle=7.85398
    g14: ArcOfCircle CenterX=25.57 CenterY=-0.59 CenterZ=0 NormalX=0 NormalY=0 NormalZ=1 AngleXU=0 Radius=1.6 StartAngle=1.5708 EndAngle=4.71239
    g15: ArcOfCircle CenterX=30.57 CenterY=-0.59 CenterZ=0 NormalX=0 NormalY=0 NormalZ=1 AngleXU=0 Radius=1.6 StartAngle=4.71239 EndAngle=7.85398
    g16: LineSegment StartX=25.57 StartY=1.01 StartZ=0 EndX=30.57 EndY=1.01 EndZ=0
    g17: LineSegment StartX=25.57 StartY=-2.19 StartZ=0 EndX=30.57 EndY=-2.19 EndZ=0
    g18: LineSegment StartX=25.57 StartY=26.01 StartZ=0 EndX=30.57 EndY=26.01 EndZ=0
    g19: LineSegment StartX=25.57 StartY=22.81 StartZ=0 EndX=30.57 EndY=22.81 EndZ=0
    g20: GeomPoint X=33 Y=12 Z=0
    g21: GeomPoint X=33 Y=12 Z=0
    g22: GeomPoint X=33 Y=12 Z=0
  constraints (65):
    c: Coincident(g0,g1)
    c: Vertical(g1)
    c: Coincident(g1,g2)
    c: Coincident(g3,g2)
    c: Coincident(g3,g0)
    c: Horizontal(g2)
    c: Horizontal(g0)
    c: DistanceY(g1,g1) = 38
    c: DistanceX(g0) = 66
    c: Horizontal(g4)
    c: Horizontal(g5)
    c: DistanceY(g3) = 12
    c: Vertical(g5,g4)
    c: DistanceX(g3) = 33
    c: Vertical(g0,g3)
    c: Equal(g0,g2)
    c: Diameter(g6) = 3.5
    c: DistanceX(g6,g0) = 15
    c: DistanceY(g6,g0) = 19.14
    c: Horizontal(g7)
    c: Horizontal(g8)
    c: Tangent(g6,g7) = 1.5708
    c: Tangent(g6,g8) = -1.5708
    c: Coincident(g9,g3)
    c: Coincident(g9,g5)
    c: Coincident(g11,g4)
    c: Coincident(g10,g5)
    c: Symmetric(g4,g5,g10)
    c: Coincident(g10,g7)
    c: Coincident(g11,g8)
    c: DistanceX(g3,g10) = 3
    c: Coincident(g10,g11)
    c: Diameter(g9) = 20.5
    c: Coincident(g9,g4)
    c: Vertical(g4,g5)
    c: DistanceX(g12) = 25.57
    c: Horizontal(g12,g13)
    c: Horizontal(g14,g15)
    c: Vertical(g12,g14)
    c: Equal(g12,g13)
    c: Diameter(g12) = 3.2
    c: Equal(g14,g15)
    c: Diameter(g14) = 3.2
    c: DistanceX(g12,g13) = 5
    c: Vertical(g13,g15)
    c: DistanceY(g14,g12) = 25
    c: Tangent(g15,g16) = 1.5708
    c: Tangent(g15,g17) = -1.5708
    c: Coincident(g14,g17)
    c: Coincident(g14,g16)
    c: Vertical(g14,g14)
    c: Coincident(g13,g18)
    c: Coincident(g13,g19)
    c: Coincident(g12,g19)
    c: Coincident(g12,g18)
    c: Vertical(g12,g12)
    c: Vertical(g13,g13)
    c: Coincident(g20,g3)
    c: Coincident(g21,g3)
    c: Coincident(g22,g3)
    c: DistanceY(g12) = 24.41
    c: Vertical(g4,g3)
    c: Vertical(g13,g13)
    c: Vertical(g12,g12)
    c: Vertical(g14,g14)
FEATURE [PartDesign::Pad] Pad068
  Direction = (0,-1,-2e-16)
  Length = 5
  Length2 = 10
  Placement = pos=(0,0,0) rot=(1,0,0;1.5708rad)
  Profile = -> Sketch124
  ReferenceAxis = -> Sketch124 [N_Axis]
  Reversed = true
  Type = 0
FEATURE [Sketcher::SketchObject] Sketch125
  AttachmentOffset = pos=(0,0,67) rot=(0,0,1;0rad)
  FullyConstrained = true
  MapMode = 5
  Placement = pos=(67,-1.49e-14,1.49e-14) rot=(0.57735,0.57735,0.57735;2.0944rad)
  Support = -> [YZ_Plane042]
  sketch-geometry (4):
    g0: LineSegment StartX=80 StartY=17 StartZ=0 EndX=60 EndY=17 EndZ=0
    g1: LineSegment StartX=60 StartY=17 StartZ=0 EndX=60 EndY=-21 EndZ=0
    g2: LineSegment StartX=60 StartY=-21 StartZ=0 EndX=80 EndY=-21 EndZ=0
    g3: LineSegment StartX=80 StartY=-21 StartZ=0 EndX=80 EndY=17 EndZ=0
  constraints (12):
    c: Coincident(g0,g1)
    c: Coincident(g1,g2)
    c: Coincident(g2,g3)
    c: Coincident(g3,g0)
    c: Horizontal(g0)
    c: Horizontal(g2)
    c: Vertical(g1)
    c: Vertical(g3)
    c: DistanceX(g0) = 80
    c: Distance(g3) = 38
    c: DistanceY(g0) = 17
    c: Distance(g0) = 20
FEATURE [PartDesign::Pad] Pad069
  BaseFeature = -> Pad068
  Direction = (1,-2e-16,3e-16)
  Length = 4
  Length2 = 10
  Placement = pos=(0,0,0) rot=(1,0,0;1.5708rad)
  Profile = -> Sketch125
  ReferenceAxis = -> Sketch125 [N_Axis]
  Reversed = true
  Type = 0
FEATURE [Sketcher::SketchObject] Sketch
  AttachmentOffset = pos=(0,0,67) rot=(0,0,1;0rad)
  FullyConstrained = true
  MapMode = 5
  Placement = pos=(67,-1.49e-14,1.49e-14) rot=(0.57735,0.57735,0.57735;2.0944rad)
  Support = -> [YZ_Plane042]
  sketch-geometry (2):
    g0: Circle CenterX=68 CenterY=8 CenterZ=0 NormalX=0 NormalY=0 NormalZ=1 AngleXU=0 Radius=2.1
    g1: Circle CenterX=68 CenterY=-12 CenterZ=0 NormalX=0 NormalY=0 NormalZ=1 AngleXU=0 Radius=2.1
  constraints (6):
    c: Equal(g0,g1)
    c: Diameter(g0) = 4.2
    c: Vertical(g1,g0)
    c: Distance(g1,g0) = 20
    c: DistanceY(g0) = 8
    c: DistanceX(g0) = 68
FEATURE [PartDesign::Pocket] Pocket
  BaseFeature = -> Pad069
  Direction = (-1,2e-16,-3e-16)
  Length = 5
  Length2 = 5
  Placement = pos=(0,0,0) rot=(1,0,0;1.5708rad)
  Profile = -> Sketch
  ReferenceAxis = -> Sketch [N_Axis]
  Type = 1
FEATURE [Sketcher::SketchObject] Sketch126
  AttachmentOffset = pos=(0,0,-21) rot=(0,0,1;0rad)
  FullyConstrained = true
  MapMode = 5
  Placement = pos=(0,0,-21) rot=(0,0,1;0rad)
  Support = -> [XY_Plane042]
  sketch-geometry (3):
    g0: LineSegment StartX=63 StartY=60 StartZ=0 EndX=63 EndY=75 EndZ=0
    g1: LineSegment StartX=63 StartY=75 StartZ=0 EndX=48 EndY=75 EndZ=0
    g2: LineSegment StartX=48 StartY=75 StartZ=0 EndX=63 EndY=60 EndZ=0
  constraints (9):
    c: Vertical(g0)
    c: Coincident(g0,g1)
    c: Horizontal(g1)
    c: Coincident(g1,g2)
    c: Coincident(g2,g0)
    c: Equal(g1,g0)
    c: Distance(g0) = 15
    c: DistanceY(g0) = 75
    c: DistanceX(g0) = 63
FEATURE [PartDesign::Pad] Pad
  BaseFeature = -> Pocket
  Direction = (0,0,1)
  Length = 3
  Length2 = 10
  Placement = pos=(0,0,0) rot=(1,0,0;1.5708rad)
  Profile = -> Sketch126
  ReferenceAxis = -> Sketch126 [N_Axis]
  Type = 0
FEATURE [Sketcher::SketchObject] Sketch127
  AttachmentOffset = pos=(0,0,17) rot=(0,0,1;0rad)
  FullyConstrained = true
  MapMode = 5
  Placement = pos=(0,0,17) rot=(0,0,1;0rad)
  Support = -> [XY_Plane042]
  sketch-geometry (3):
    g0: LineSegment StartX=63 StartY=60 StartZ=0 EndX=63 EndY=75 EndZ=0
    g1: LineSegment StartX=63 StartY=75 StartZ=0 EndX=48 EndY=75 EndZ=0
    g2: LineSegment StartX=48 StartY=75 StartZ=0 EndX=63 EndY=60 EndZ=0
  constraints (9):
    c: Vertical(g0)
    c: Coincident(g0,g1)
    c: Horizontal(g1)
    c: Coincident(g1,g2)
    c: Coincident(g2,g0)
    c: Equal(g1,g0)
    c: Distance(g0) = 15
    c: DistanceY(g0) = 75
    c: DistanceX(g0) = 63
FEATURE [PartDesign::Pad] Pad070
  BaseFeature = -> Pad
  Direction = (0,0,1)
  Length = 3
  Length2 = 10
  Placement = pos=(0,0,0) rot=(1,0,0;1.5708rad)
  Profile = -> Sketch127
  ReferenceAxis = -> Sketch127 [N_Axis]
  Reversed = true
  Type = 0
FEATURE [PartDesign::Chamfer] Chamfer
  Angle = 45
  Base = -> Pad070 [Face6]
  BaseFeature = -> Pad070
  ChamferType = 0
  FlipDirection = false
  Placement = pos=(0,0,0) rot=(1,0,0;1.5708rad)
  Size = 0.5
  Size2 = 1
  SupportTransform = false
  UseAllEdges = false
FEATURE [PartDesign::Chamfer] Chamfer001
  Angle = 45
  Base = -> Chamfer [Edge73,Edge72,Edge79,Edge78,Edge77]
  BaseFeature = -> Chamfer
  ChamferType = 0
  FlipDirection = false
  Placement = pos=(0,0,0) rot=(1,0,0;1.5708rad)
  Size = 0.3
  Size2 = 1
  SupportTransform = false
  UseAllEdges = false
FEATURE [PartDesign::Chamfer] Chamfer002
  Angle = 45
  Base = -> Chamfer001 [Edge5,Edge3,Edge1]
  BaseFeature = -> Chamfer001
  ChamferType = 0
  FlipDirection = false
  Placement = pos=(0,0,0) rot=(1,0,0;1.5708rad)
  Size = 0.3
  Size2 = 1
  SupportTransform = false
  UseAllEdges = false
FEATURE [PartDesign::Chamfer] Chamfer003
  Angle = 45
  Base = -> Chamfer002 [Edge54,Edge52]
  BaseFeature = -> Chamfer002
  ChamferType = 0
  FlipDirection = false
  Placement = pos=(0,0,0) rot=(1,0,0;1.5708rad)
  Size = 0.4
  Size2 = 1
  SupportTransform = false
  UseAllEdges = false
FEATURE [PartDesign::Chamfer] Chamfer004
  Angle = 45
  Base = -> Chamfer003 [Edge48,Edge50]
  BaseFeature = -> Chamfer003
  ChamferType = 0
  FlipDirection = false
  Placement = pos=(0,0,0) rot=(1,0,0;1.5708rad)
  Size = 0.4
  Size2 = 1
  SupportTransform = false
  UseAllEdges = false
FEATURE [PartDesign::Chamfer] Chamfer005
  Angle = 45
  Base = -> Chamfer004 [Edge33]
  BaseFeature = -> Chamfer004
  ChamferType = 0
  FlipDirection = false
  Placement = pos=(0,0,0) rot=(1,0,0;1.5708rad)
  Size = 0.4
  Size2 = 1
  SupportTransform = false
  UseAllEdges = false
FEATURE [PartDesign::Body] Body026  label="Roll Encoder Mount"
  Group = -> [Sketch124,Pad068,Sketch125,Pad069,Sketch,Pocket,Sketch126,Pad,Sketch127,Pad070,Chamfer,Chamfer001,Chamfer002,Chamfer003,Chamfer004,Chamfer005]
  Origin = -> Origin042
  Placement = pos=(0,2,0) rot=(0,0,1;0rad)
  Tip = -> Chamfer005
---- part Parts/Roll_Encoder_Pulley.FCStd = doc fcstd_fdb3ba359fab ----
FCSTD DOCUMENT  (FreeCAD 0.21R32110 (Git))
Label: Roll_Encoder_Pulley
License: All rights reserved
LicenseURL: http://en.wikipedia.org/wiki/All_rights_reserved
objects: Sketcher::SketchObject×3, PartDesign::Pad×2, PartDesign::Chamfer×2, PartDesign::FeaturePython×1, PartDesign::Pocket×1, PartDesign::Body×1, App::Part×1
note: 15 computed .brp shape members not serialized (recipe doc carries the construction recipe); baked Part::Feature solids carry a one-line shape summary decoded from their .brp

FEATURE [PartDesign::FeaturePython] TimingGear  # WARN: FeaturePython — macro-defined, semantics opaque (R4)
  AttacherType = Attacher::AttachEngine3D
  h = 0.75
  height = 7
  offset = 0.4
  pitch = 2
  r0 = 0.555
  r1 = 1
  rs = 0.15
  teeth = 26
  type = 0
  u = 0.254
  version = 0.0.4
FEATURE [Sketcher::SketchObject] Sketch
  AttachmentOffset = pos=(0,0,1) rot=(0,0,1;0rad)
  FullyConstrained = true
  MapMode = 5
  Placement = pos=(0,0,1) rot=(0,0,1;0rad)
  Support = -> [XY_Plane001]
  sketch-geometry (1):
    g0: Circle CenterX=0 CenterY=0 CenterZ=0 NormalX=0 NormalY=0 NormalZ=1 AngleXU=0 Radius=9
  constraints (2):
    c: Coincident(g0,g-1)
    c: Diameter(g0) = 18
FEATURE [PartDesign::Pad] Pad
  AlongSketchNormal = false
  BaseFeature = -> TimingGear
  Direction = (0,0,1)
  Length = 2
  Length2 = 10
  Profile = -> Sketch
  ReferenceAxis = -> Sketch [N_Axis]
  Reversed = true
  Type = 0
FEATURE [Sketcher::SketchObject] Sketch001
  AttachmentOffset = pos=(0,0,7) rot=(0,0,1;0rad)
  FullyConstrained = true
  MapMode = 5
  Placement = pos=(0,0,7) rot=(0,0,1;0rad)
  Support = -> [XY_Plane001]
  sketch-geometry (1):
    g0: Circle CenterX=0 CenterY=0 CenterZ=0 NormalX=0 NormalY=0 NormalZ=1 AngleXU=0 Radius=9
  constraints (2):
    c: Coincident(g0,g-1)
    c: Diameter(g0) = 18
FEATURE [PartDesign::Pad] Pad001
  BaseFeature = -> Pad
  Direction = (0,0,1)
  Length = 2
  Length2 = 10
  Profile = -> Sketch001
  ReferenceAxis = -> Sketch001 [N_Axis]
  Type = 0
FEATURE [Sketcher::SketchObject] Sketch002
  AttachmentOffset = pos=(0,0,-2) rot=(0,0,1;0rad)
  FullyConstrained = true
  MapMode = 5
  Placement = pos=(0,0,-2) rot=(0,0,1;0rad)
  Support = -> [XY_Plane001]
  sketch-geometry (2):
    g0: ArcOfCircle CenterX=0 CenterY=0 CenterZ=0 NormalX=0 NormalY=0 NormalZ=1 AngleXU=0 Radius=3.2 StartAngle=2.24493 EndAngle=7.17985
    g1: LineSegment StartX=-1.9975 StartY=2.5 StartZ=0 EndX=1.9975 EndY=2.5 EndZ=0
  constraints (6):
    c: Coincident(g0,g-1)
    c: Diameter(g0) = 6.4
    c: Horizontal(g1)
    c: Coincident(g1,g0)
    c: Coincident(g1,g0)
    c: DistanceY(g0,g0) = 2.5
FEATURE [PartDesign::Pocket] Pocket
  BaseFeature = -> Pad001
  Direction = (0,0,-1)
  Length = 7
  Length2 = 5
  Profile = -> Sketch002
  ReferenceAxis = -> Sketch002 [N_Axis]
  Reversed = true
  Type = 1
FEATURE [PartDesign::Chamfer] Chamfer
  Angle = 45
  Base = -> Pocket [Edge478,Edge2]
  BaseFeature = -> Pocket
  ChamferType = 0
  FlipDirection = false
  Size = 0.9
  Size2 = 1
  SupportTransform = false
  UseAllEdges = false
FEATURE [PartDesign::Chamfer] Chamfer001
  Angle = 45
  Base = -> Chamfer [Edge480,Edge3]
  BaseFeature = -> Chamfer
  ChamferType = 0
  FlipDirection = false
  Size = 0.3
  Size2 = 1
  SupportTransform = false
  UseAllEdges = false
FEATURE [PartDesign::Body] Body
  Group = -> [TimingGear,Sketch,Pad,Sketch001,Pad001,Sketch002,Pocket,Chamfer,Chamfer001]
  Origin = -> Origin001
  Tip = -> Chamfer001
FEATURE [App::Part] Part
  Group = -> [Body]
  Origin = -> Origin
---- part Parts/Roll_Motor_Mount.FCStd = doc fcstd_34d485632d3c ----
FCSTD DOCUMENT  (FreeCAD 0.21R32110 (Git))
Label: Roll_Motor_Mount
License: All rights reserved
LicenseURL: http://en.wikipedia.org/wiki/All_rights_reserved
objects: Sketcher::SketchObject×2, PartDesign::Pad×2, PartDesign::Fillet×1, PartDesign::Body×1
note: 9 computed .brp shape members not serialized (recipe doc carries the construction recipe); baked Part::Feature solids carry a one-line shape summary decoded from their .brp

FEATURE [Sketcher::SketchObject] Sketch017
  AttachmentOffset = pos=(3,-3,-40) rot=(0,0,1;0rad)
  FullyConstrained = false
  MapMode = 5
  Placement = pos=(-40,3,-3) rot=(0.57735,0.57735,0.57735;2.0944rad)
  Support = -> [YZ_Plane009]
  sketch-geometry (8):
    g0: LineSegment StartX=-2.53905 StartY=-25.1351 StartZ=0 EndX=39.4609 EndY=-25.1351 EndZ=0
    g1: LineSegment StartX=39.4609 StartY=-25.1351 StartZ=0 EndX=39.4609 EndY=19.8649 EndZ=0
    g2: LineSegment StartX=39.4609 StartY=19.8649 StartZ=0 EndX=-2.53905 EndY=19.8649 EndZ=0
    g3: LineSegment StartX=-2.53905 StartY=19.8649 StartZ=0 EndX=-2.53905 EndY=-25.1351 EndZ=0
    g4: Circle CenterX=12.4609 CenterY=11.8649 CenterZ=0 NormalX=0 NormalY=0 NormalZ=1 AngleXU=0 Radius=3
    g5: Circle CenterX=30.4609 CenterY=11.8649 CenterZ=0 NormalX=0 NormalY=0 NormalZ=1 AngleXU=0 Radius=3
    g6: Circle CenterX=30.4609 CenterY=-17.1351 CenterZ=0 NormalX=0 NormalY=0 NormalZ=1 AngleXU=0 Radius=3
    g7: Circle CenterX=12.4609 CenterY=-17.1351 CenterZ=0 NormalX=0 NormalY=0 NormalZ=1 AngleXU=0 Radius=3
  constraints (22):
    c: Coincident(g0,g1)
    c: Coincident(g1,g2)
    c: Coincident(g2,g3)
    c: Coincident(g3,g0)
    c: Horizontal(g0)
    c: Horizontal(g2)
    c: Vertical(g1)
    c: Vertical(g3)
    c: DistanceX(g2,g2) = 42
    c: DistanceY(g1,g1) = 45
    c: Horizontal(g4,g5)
    c: Horizontal(g7,g6)
    c: Vertical(g6,g5)
    c: Vertical(g4,g7)
    c: DistanceY(g6,g5) = 29
    c: DistanceY(g0,g6) = 8
    c: Equal(g4,g5)
    c: Equal(g4,g7)
    c: Equal(g4,g6)
    c: Diameter(g4) = 6
    c: DistanceX(g4,g5) = 18
    c: DistanceX(g2,g4) = 15
FEATURE [PartDesign::Pad] Pad012
  Direction = (1,-2e-16,3e-16)
  Length = 2
  Length2 = 10
  Placement = pos=(0,0,0) rot=(0.57735,0.57735,0.57735;2.0944rad)
  Profile = -> Sketch017
  ReferenceAxis = -> Sketch017 [N_Axis]
  Reversed = true
  Type = 0
FEATURE [Sketcher::SketchObject] Sketch018
  AttachmentOffset = pos=(-21,-3,0) rot=(0,0,1;0rad)
  FullyConstrained = false
  MapMode = 5
  Placement = pos=(-21,7e-16,-3) rot=(1,0,0;1.5708rad)
  Support = -> [XZ_Plane009]
  sketch-geometry (12):
    g0: LineSegment StartX=-20.9755 StartY=19.8621 StartZ=0 EndX=-78.4755 EndY=19.8621 EndZ=0
    g1: LineSegment StartX=-78.4755 StartY=19.8621 StartZ=0 EndX=-78.4755 EndY=-25.1379 EndZ=0
    g2: LineSegment StartX=-78.4755 StartY=-25.1379 StartZ=0 EndX=-20.9755 EndY=-25.1379 EndZ=0
    g3: LineSegment StartX=-20.9755 StartY=-25.1379 StartZ=0 EndX=-20.9755 EndY=19.8621 EndZ=0
    g4: LineSegment StartX=-57 StartY=-15 StartZ=0 EndX=-45 EndY=-15 EndZ=0
    g5: LineSegment StartX=-32.5 StartY=-2.5 StartZ=0 EndX=-32.5 EndY=-1.5 EndZ=0
    g6: LineSegment StartX=-45 StartY=11 StartZ=0 EndX=-57 EndY=11 EndZ=0
    g7: LineSegment StartX=-69.5 StartY=-1.5 StartZ=0 EndX=-69.5 EndY=-2.5 EndZ=0
    g8: ArcOfCircle CenterX=-57 CenterY=-2.5 CenterZ=0 NormalX=0 NormalY=0 NormalZ=1 AngleXU=0 Radius=12.5 StartAngle=3.14159 EndAngle=4.71239
    g9: ArcOfCircle CenterX=-57 CenterY=-1.5 CenterZ=0 NormalX=0 NormalY=0 NormalZ=1 AngleXU=0 Radius=12.5 StartAngle=1.5708 EndAngle=3.14159
    g10: ArcOfCircle CenterX=-45 CenterY=-1.5 CenterZ=0 NormalX=0 NormalY=0 NormalZ=1 AngleXU=0 Radius=12.5 StartAngle=0 EndAngle=1.5708
    g11: ArcOfCircle CenterX=-45 CenterY=-2.5 CenterZ=0 NormalX=0 NormalY=0 NormalZ=1 AngleXU=0 Radius=12.5 StartAngle=4.71239 EndAngle=6.28319
  constraints (30):
    c: Coincident(g0,g1)
    c: Coincident(g1,g2)
    c: Coincident(g2,g3)
    c: Coincident(g3,g0)
    c: Horizontal(g0)
    c: Horizontal(g2)
    c: Vertical(g1)
    c: Vertical(g3)
    c: DistanceY(g3,g3) = 45
    c: DistanceX(g0,g0) = 57.5
    c: Horizontal(g4)
    c: Horizontal(g6)
    c: Vertical(g5)
    c: Vertical(g7)
    c: Tangent(g7,g8) = -1.5708
    c: Tangent(g4,g8) = -1.5708
    c: Tangent(g7,g9) = -1.5708
    c: Tangent(g6,g9) = -1.5708
    c: Tangent(g6,g10) = -1.5708
    c: Tangent(g5,g10) = -1.5708
    c: Tangent(g4,g11) = -1.5708
    c: Tangent(g5,g11) = -1.5708
    c: Equal(g9,g10)
    c: Equal(g9,g11)
    c: Equal(g9,g8)
    c: Diameter(g9) = 25
    c: DistanceY(g4,g6) = 26
    c: DistanceX(g6,g6) = 12
    c: DistanceY(g4) = -15
    c: DistanceX(g4) = -45
FEATURE [PartDesign::Pad] Pad013
  BaseFeature = -> Pad012
  Direction = (0,-1,-2e-16)
  Length = 2
  Length2 = 10
  Placement = pos=(0,0,0) rot=(0.57735,0.57735,0.57735;2.0944rad)
  Profile = -> Sketch018
  ReferenceAxis = -> Sketch018 [N_Axis]
  Reversed = true
  Type = 0
FEATURE [PartDesign::Fillet] Fillet
  Base = -> Pad013 [Edge48,Edge47]
  BaseFeature = -> Pad013
  Placement = pos=(0,0,0) rot=(0.57735,0.57735,0.57735;2.0944rad)
  Radius = 22
  SupportTransform = false
  UseAllEdges = false
FEATURE [PartDesign::Body] Body005  label="Roll Motor Mount"
  Group = -> [Sketch017,Pad012,Sketch018,Pad013,Fillet]
  Origin = -> Origin009
  Tip = -> Fillet
---- part Parts/Yoke_Bearing.FCStd = doc fcstd_b6bac02575db ----
FCSTD DOCUMENT  (FreeCAD 0.21R32110 (Git))
Label: Yoke_Bearing
License: All rights reserved
LicenseURL: http://en.wikipedia.org/wiki/All_rights_reserved
objects: PartDesign::Chamfer×2, Sketcher::SketchObject×1, PartDesign::Pad×1, PartDesign::Body×1
note: 8 computed .brp shape members not serialized (recipe doc carries the construction recipe); baked Part::Feature solids carry a one-line shape summary decoded from their .brp

FEATURE [Sketcher::SketchObject] Sketch057
  AttachmentOffset = pos=(0,0,-2) rot=(0,0,1;0rad)
  FullyConstrained = true
  MapMode = 5
  Placement = pos=(0,122.5,0) rot=(1,0,0;1.5708rad)
  sketch-geometry (2):
    g0: Circle CenterX=0 CenterY=0 CenterZ=0 NormalX=0 NormalY=0 NormalZ=1 AngleXU=0 Radius=21
    g1: Circle CenterX=0 CenterY=0 CenterZ=0 NormalX=0 NormalY=0 NormalZ=1 AngleXU=0 Radius=12.5
  constraints (4):
    c: Coincident(g0,g-1)
    c: Coincident(g1,g0)
    c: Diameter(g0) = 42
    c: Diameter(g1) = 25
FEATURE [PartDesign::Pad] Pad034
  Direction = (0,-1,0)
  Length = 9
  Length2 = 10
  Placement = pos=(0,122.5,0) rot=(1,0,0;1.5708rad)
  Profile = -> Sketch057
  ReferenceAxis = -> Sketch057 [N_Axis]
  Reversed = true
  Type = 0
FEATURE [PartDesign::Chamfer] Chamfer
  Angle = 45
  Base = -> Pad034 [Face3]
  BaseFeature = -> Pad034
  ChamferType = 0
  FlipDirection = false
  Placement = pos=(0,122.5,0) rot=(1,0,0;1.5708rad)
  Size = 0.5
  Size2 = 1
  SupportTransform = false
  UseAllEdges = false
FEATURE [PartDesign::Chamfer] Chamfer001
  Angle = 45
  Base = -> Chamfer [Face3]
  BaseFeature = -> Chamfer
  ChamferType = 0
  FlipDirection = false
  Placement = pos=(0,122.5,0) rot=(1,0,0;1.5708rad)
  Size = 0.5
  Size2 = 1
  SupportTransform = false
  UseAllEdges = false
FEATURE [PartDesign::Body] Body008  label="Yoke_Bearing"
  Group = -> [Sketch057,Pad034,Chamfer,Chamfer001]
  Origin = -> Origin012
  Tip = -> Chamfer001
---- part Parts/Yoke_Encoder_Pulley.FCStd = doc fcstd_738ef21aebc0 ----
FCSTD DOCUMENT  (FreeCAD 0.21R33668 +26 (Git))
Label: Yoke_Encoder_Pulley
License: All rights reserved
LicenseURL: http://en.wikipedia.org/wiki/All_rights_reserved
objects: Sketcher::SketchObject×10, PartDesign::Pad×5, PartDesign::Pocket×5, PartDesign::Chamfer×2, PartDesign::FeaturePython×1, PartDesign::Body×1
note: 36 computed .brp shape members not serialized (recipe doc carries the construction recipe); baked Part::Feature solids carry a one-line shape summary decoded from their .brp

FEATURE [Sketcher::SketchObject] Sketch002
  FullyConstrained = true
  MapMode = 5
  Placement = pos=(0,0,0) rot=(1,0,0;1.5708rad)
  Support = -> [XZ_Plane]
  sketch-geometry (1):
    g0: Circle CenterX=0 CenterY=0 CenterZ=0 NormalX=0 NormalY=0 NormalZ=1 AngleXU=0 Radius=14.5
  constraints (2):
    c: Coincident(g0,g-1)
    c: Diameter(g0) = 29
FEATURE [Sketcher::SketchObject] Sketch003
  AttachmentOffset = pos=(0,0,5) rot=(0,0,1;0rad)
  FullyConstrained = true
  MapMode = 5
  Placement = pos=(5,-1.1e-15,1.1e-15) rot=(0.57735,0.57735,0.57735;2.0944rad)
  Support = -> [YZ_Plane]
  sketch-geometry (1):
    g0: Circle CenterX=-18 CenterY=17 CenterZ=0 NormalX=0 NormalY=0 NormalZ=1 AngleXU=0 Radius=1.65
  constraints (3):
    c: DistanceX(g0) = -18
    c: DistanceY(g0) = 17
    c: Diameter(g0) = 3.3
FEATURE [PartDesign::FeaturePython] TimingGear  # WARN: FeaturePython — macro-defined, semantics opaque (R4)
  AttacherType = Attacher::AttachEngine3D
  Placement = pos=(0,-2,0) rot=(1,0,0;1.5708rad)
  h = 0.75
  height = 6.5
  offset = 0.4
  pitch = 2
  r0 = 0.555
  r1 = 1
  rs = 0.15
  teeth = 52
  type = 0
  u = 0.254
  version = 0.0.4
FEATURE [Sketcher::SketchObject] Sketch004
  AttachmentOffset = pos=(0,0,23) rot=(0,0,1;0rad)
  FullyConstrained = true
  MapMode = 5
  Placement = pos=(0,-23,-5.1e-15) rot=(1,0,0;1.5708rad)
  Support = -> [XZ_Plane]
  sketch-geometry (4):
    g0: LineSegment StartX=-0.5 StartY=21 StartZ=0 EndX=0.5 EndY=21 EndZ=0
    g1: LineSegment StartX=0.5 StartY=21 StartZ=0 EndX=0.5 EndY=9 EndZ=0
    g2: LineSegment StartX=0.5 StartY=9 StartZ=0 EndX=-0.5 EndY=9 EndZ=0
    g3: LineSegment StartX=-0.5 StartY=9 StartZ=0 EndX=-0.5 EndY=21 EndZ=0
  constraints (11):
    c: Coincident(g0,g1)
    c: Coincident(g1,g2)
    c: Coincident(g2,g3)
    c: Coincident(g3,g0)
    c: Horizontal(g0)
    c: Vertical(g1)
    c: Vertical(g3)
    c: Symmetric(g2,g1,g-2)
    c: Distance(g0) = 1
    c: Distance(g1) = 12
    c: DistanceY(g1) = 9
FEATURE [PartDesign::Pad] Pad
  BaseFeature = -> TimingGear
  Direction = (0,-1,-2e-16)
  Length = 25
  Length2 = 10
  Placement = pos=(0,-2,0) rot=(1,0,0;1.5708rad)
  Profile = -> Sketch002
  ReferenceAxis = -> Sketch002 [N_Axis]
  Type = 0
FEATURE [Sketcher::SketchObject] Sketch005
  AttachmentOffset = pos=(0,0,14) rot=(0,0,1;0rad)
  FullyConstrained = true
  MapMode = 5
  Placement = pos=(0,-14,-3.1e-15) rot=(1,0,0;1.5708rad)
  Support = -> [XZ_Plane]
  sketch-geometry (4):
    g0: LineSegment StartX=-3.5 StartY=20.5 StartZ=0 EndX=3.5 EndY=20.5 EndZ=0
    g1: LineSegment StartX=3.5 StartY=20.5 StartZ=0 EndX=3.5 EndY=12.5 EndZ=0
    g2: LineSegment StartX=3.5 StartY=12.5 StartZ=0 EndX=-3.5 EndY=12.5 EndZ=0
    g3: LineSegment StartX=-3.5 StartY=12.5 StartZ=0 EndX=-3.5 EndY=20.5 EndZ=0
  constraints (11):
    c: Coincident(g0,g1)
    c: Coincident(g1,g2)
    c: Coincident(g2,g3)
    c: Coincident(g3,g0)
    c: Horizontal(g2)
    c: Vertical(g1)
    c: Vertical(g3)
    c: Symmetric(g0,g0,g-2)
    c: Distance(g1) = 8
    c: Distance(g0) = 7
    c: DistanceY(g2) = 12.5
FEATURE [PartDesign::Pad] Pad001
  BaseFeature = -> Pad
  Direction = (0,-1,-2e-16)
  Length = 8
  Length2 = 10
  Placement = pos=(0,-2,0) rot=(1,0,0;1.5708rad)
  Profile = -> Sketch005
  ReferenceAxis = -> Sketch005 [N_Axis]
  Type = 0
FEATURE [PartDesign::Pocket] Pocket001
  BaseFeature = -> Pad001
  Direction = (-1,2e-16,-3e-16)
  Length = 5
  Length2 = 5
  Placement = pos=(0,-2,0) rot=(1,0,0;1.5708rad)
  Profile = -> Sketch003
  ReferenceAxis = -> Sketch003 [N_Axis]
  Type = 1
FEATURE [PartDesign::Pocket] Pocket002
  BaseFeature = -> Pocket001
  Direction = (0,1,2e-16)
  Length = 11
  Length2 = 5
  Placement = pos=(0,-2,0) rot=(1,0,0;1.5708rad)
  Profile = -> Sketch004
  ReferenceAxis = -> Sketch004 [N_Axis]
  Type = 0
FEATURE [Sketcher::SketchObject] Sketch007
  AttachmentOffset = pos=(0,0,2.2) rot=(0,0,1;0rad)
  FullyConstrained = true
  MapMode = 5
  Placement = pos=(0,-2.2,-5e-16) rot=(1,0,0;1.5708rad)
  Support = -> [XZ_Plane]
  sketch-geometry (1):
    g0: Circle CenterX=0 CenterY=0 CenterZ=0 NormalX=0 NormalY=0 NormalZ=1 AngleXU=0 Radius=17.5
  constraints (2):
    c: Coincident(g0,g-1)
    c: Diameter(g0) = 35
FEATURE [PartDesign::Pad] Pad003
  BaseFeature = -> Pocket002
  Direction = (0,-1,-2e-16)
  Length = 2.5
  Length2 = 10
  Placement = pos=(0,-2,0) rot=(1,0,0;1.5708rad)
  Profile = -> Sketch007
  ReferenceAxis = -> Sketch007 [N_Axis]
  Reversed = true
  Type = 0
FEATURE [Sketcher::SketchObject] Sketch008
  AttachmentOffset = pos=(0,0,8.5) rot=(0,0,1;0rad)
  FullyConstrained = true
  MapMode = 5
  Placement = pos=(0,-8.5,-1.9e-15) rot=(1,0,0;1.5708rad)
  Support = -> [XZ_Plane]
  sketch-geometry (1):
    g0: Circle CenterX=0 CenterY=0 CenterZ=0 NormalX=0 NormalY=0 NormalZ=1 AngleXU=0 Radius=17.5
  constraints (2):
    c: Coincident(g0,g-1)
    c: Diameter(g0) = 35
FEATURE [PartDesign::Pad] Pad004
  BaseFeature = -> Pad003
  Direction = (0,-1,-2e-16)
  Length = 2.5
  Length2 = 10
  Placement = pos=(0,-2,0) rot=(1,0,0;1.5708rad)
  Profile = -> Sketch008
  ReferenceAxis = -> Sketch008 [N_Axis]
  Type = 0
FEATURE [Sketcher::SketchObject] Sketch009
  FullyConstrained = true
  MapMode = 5
  Placement = pos=(0,0,0) rot=(0.57735,0.57735,0.57735;2.0944rad)
  Support = -> [YZ_Plane]
  sketch-geometry (4):
    g0: LineSegment StartX=-14.01 StartY=12.6 StartZ=0 EndX=-9.6 EndY=12.6 EndZ=0
    g1: LineSegment StartX=-9.6 StartY=12.6 StartZ=0 EndX=-9.6 EndY=17.44 EndZ=0
    g2: LineSegment StartX=-9.6 StartY=17.44 StartZ=0 EndX=-14.01 EndY=20.5 EndZ=0
    g3: LineSegment StartX=-14.01 StartY=20.5 StartZ=0 EndX=-14.01 EndY=12.6 EndZ=0
  constraints (12):
    c: Coincident(g0,g1)
    c: Coincident(g1,g2)
    c: Coincident(g2,g3)
    c: Coincident(g3,g0)
    c: Vertical(g1)
    c: Vertical(g3)
    c: Horizontal(g0)
    c: Distance(g3) = 7.9
    c: Distance(g1) = 4.84
    c: DistanceX(g0) = -9.6
    c: DistanceY(g0) = 12.6
    c: Distance(g0) = 4.41
FEATURE [PartDesign::Chamfer] Chamfer
  Angle = 45
  Base = -> Pad004 [Edge5,Edge319]
  BaseFeature = -> Pad004
  ChamferType = 0
  FlipDirection = false
  Placement = pos=(0,-2,0) rot=(1,0,0;1.5708rad)
  Size = 1
  Size2 = 1
  SupportTransform = false
  UseAllEdges = false
FEATURE [PartDesign::Chamfer] Chamfer001
  Angle = 45
  Base = -> Chamfer [Edge941,Edge946]
  BaseFeature = -> Chamfer
  ChamferType = 0
  FlipDirection = false
  Placement = pos=(0,-2,0) rot=(1,0,0;1.5708rad)
  Size = 0.5
  Size2 = 1
  SupportTransform = false
  UseAllEdges = false
FEATURE [PartDesign::Pad] Pad005
  BaseFeature = -> Chamfer001
  Direction = (1,-2e-16,3e-16)
  Length = 7
  Length2 = 10
  Midplane = true
  Placement = pos=(0,-2,0) rot=(1,0,0;1.5708rad)
  Profile = -> Sketch009
  ReferenceAxis = -> Sketch009 [N_Axis]
  Type = 0
FEATURE [Sketcher::SketchObject] Sketch010
  AttachmentOffset = pos=(0,0,25) rot=(0,0,1;0rad)
  FullyConstrained = true
  MapMode = 5
  Placement = pos=(0,-25,-5.6e-15) rot=(1,0,0;1.5708rad)
  Support = -> [XZ_Plane]
  sketch-geometry (1):
    g0: Circle CenterX=0 CenterY=0 CenterZ=0 NormalX=0 NormalY=0 NormalZ=1 AngleXU=0 Radius=12.725
  constraints (2):
    c: Coincident(g0,g-1)
    c: Diameter(g0) = 25.45
FEATURE [PartDesign::Pocket] Pocket
  BaseFeature = -> Pad005
  Direction = (0,1,2e-16)
  Length = 30
  Length2 = 5
  Placement = pos=(0,-2,0) rot=(1,0,0;1.5708rad)
  Profile = -> Sketch010
  ReferenceAxis = -> Sketch010 [N_Axis]
  Type = 1
FEATURE [Sketcher::SketchObject] Sketch
  AttachmentOffset = pos=(0,0,22) rot=(0,0,1;0rad)
  FullyConstrained = true
  MapMode = 5
  Placement = pos=(0,-22,-4.9e-15) rot=(1,0,0;1.5708rad)
  Support = -> [XZ_Plane]
  sketch-geometry (4):
    g0: LineSegment StartX=-15 StartY=-5 StartZ=0 EndX=15 EndY=-5 EndZ=0
    g1: LineSegment StartX=15 StartY=-5 StartZ=0 EndX=15 EndY=-15 EndZ=0
    g2: LineSegment StartX=15 StartY=-15 StartZ=0 EndX=-15 EndY=-15 EndZ=0
    g3: LineSegment StartX=-15 StartY=-15 StartZ=0 EndX=-15 EndY=-5 EndZ=0
  constraints (11):
    c: Coincident(g0,g1)
    c: Coincident(g1,g2)
    c: Coincident(g2,g3)
    c: Coincident(g3,g0)
    c: Horizontal(g2)
    c: Vertical(g1)
    c: Vertical(g3)
    c: Symmetric(g0,g0,g-2)
    c: Distance(g0) = 30
    c: DistanceY(g0,g-1) = 5
    c: Distance(g3) = 10
FEATURE [Sketcher::SketchObject] Sketch011
  AttachmentOffset = pos=(0,0,22) rot=(0,0,1;0rad)
  FullyConstrained = true
  MapMode = 5
  Placement = pos=(0,-22,-4.9e-15) rot=(1,0,0;1.5708rad)
  Support = -> [XZ_Plane]
  sketch-geometry (4):
    g0: LineSegment StartX=-15 StartY=5 StartZ=0 EndX=15 EndY=5 EndZ=0
    g1: LineSegment StartX=15 StartY=5 StartZ=0 EndX=15 EndY=20 EndZ=0
    g2: LineSegment StartX=15 StartY=20 StartZ=0 EndX=-15 EndY=20 EndZ=0
    g3: LineSegment StartX=-15 StartY=20 StartZ=0 EndX=-15 EndY=5 EndZ=0
  constraints (11):
    c: Coincident(g0,g1)
    c: Coincident(g1,g2)
    c: Coincident(g2,g3)
    c: Coincident(g3,g0)
    c: Horizontal(g2)
    c: Vertical(g1)
    c: Vertical(g3)
    c: Symmetric(g0,g0,g-2)
    c: Distance(g0) = 30
    c: DistanceY(g-1,g0) = 5
    c: Distance(g3) = 15
FEATURE [PartDesign::Pocket] Pocket003
  BaseFeature = -> Pocket
  Direction = (0,1,2e-16)
  Length = 5
  Length2 = 5
  Placement = pos=(0,-2,0) rot=(1,0,0;1.5708rad)
  Profile = -> Sketch011
  ReferenceAxis = -> Sketch011 [N_Axis]
  Reversed = true
  Type = 0
FEATURE [PartDesign::Pocket] Pocket004
  BaseFeature = -> Pocket003
  Direction = (0,1,2e-16)
  Length = 3
  Length2 = 5
  Placement = pos=(0,-2,0) rot=(1,0,0;1.5708rad)
  Profile = -> Sketch
  ReferenceAxis = -> Sketch [N_Axis]
  Reversed = true
  Type = 0
FEATURE [PartDesign::Body] Body  label="RollEncoderPulley"
  Group = -> [TimingGear,Sketch002,Sketch003,Sketch004,Pad,Sketch005,Pad001,Pocket001,Pocket002,Sketch007,Pad003,Sketch008,Pad004,Sketch009,Chamfer,Chamfer001,Pad005,Sketch010,Pocket,Sketch,Sketch011,Pocket003,Pocket004]
  Origin = -> Origin
  Placement = pos=(0,30,0) rot=(0,1,0;0rad)
  Tip = -> Pocket004
---- part Parts/Yoke_Roll_IR_Limit_Ring.FCStd = doc fcstd_bc361efc3d71 ----
FCSTD DOCUMENT  (FreeCAD 0.21R32110 (Git))
Label: Yoke_Roll_IR_Limit_Ring
License: All rights reserved
LicenseURL: http://en.wikipedia.org/wiki/All_rights_reserved
objects: Sketcher::SketchObject×4, PartDesign::Pad×2, PartDesign::Pocket×2, PartDesign::Chamfer×2, App::Part×1, PartDesign::Body×1, App::MeasureDistance×1
note: 17 computed .brp shape members not serialized (recipe doc carries the construction recipe); baked Part::Feature solids carry a one-line shape summary decoded from their .brp

FEATURE [App::Part] Part
  Origin = -> Origin
FEATURE [Sketcher::SketchObject] Sketch136
  FullyConstrained = true
  MapMode = 2
  Placement = pos=(0,0,18.5) rot=(0,0,1;0rad)
  sketch-geometry (1):
    g0: Circle CenterX=0 CenterY=0 CenterZ=0 NormalX=0 NormalY=0 NormalZ=1 AngleXU=0 Radius=14.5
  constraints (2):
    c: Coincident(g0,g-1)
    c: Diameter(g0) = 29
FEATURE [Sketcher::SketchObject] Sketch138
  FullyConstrained = true
  MapMode = 5
  Support = -> [XY_Plane044]
  sketch-geometry (1):
    g0: Circle CenterX=0 CenterY=0 CenterZ=0 NormalX=0 NormalY=0 NormalZ=1 AngleXU=0 Radius=12.725
  constraints (2):
    c: Coincident(g0,g-1)
    c: Diameter(g0) = 25.45
FEATURE [Sketcher::SketchObject] Sketch141
  AttachmentOffset = pos=(0,0,17) rot=(0,0,1;0rad)
  FullyConstrained = true
  MapMode = 5
  Placement = pos=(0,0,17) rot=(0,0,1;0rad)
  Support = -> [XY_Plane044]
  sketch-geometry (3):
    g0: LineSegment StartX=0 StartY=0 StartZ=0 EndX=18.7476 EndY=-20.4594 EndZ=0
    g1: LineSegment StartX=0 StartY=0 StartZ=0 EndX=-18.7476 EndY=-20.4594 EndZ=0
    g2: ArcOfCircle CenterX=0 CenterY=0 CenterZ=0 NormalX=0 NormalY=0 NormalZ=1 AngleXU=0 Radius=27.75 StartAngle=3.97062 EndAngle=5.45415
  constraints (8):
    c: Coincident(g0,g-1)
    c: Coincident(g1,g0)
    c: Coincident(g2,g0)
    c: Diameter(g2) = 55.5
    c: Coincident(g2,g0)
    c: Coincident(g2,g1)
    c: Symmetric(g1,g0,g-2)
    c: Angle(g1,g0) = 1.48353
FEATURE [PartDesign::Pad] Pad078
  Direction = (0,0,1)
  Length = 17.5
  Length2 = 10
  Placement = pos=(0,0,18.5) rot=(0,0,1;0rad)
  Profile = -> Sketch136
  ReferenceAxis = -> Sketch136 [N_Axis]
  Reversed = true
  Type = 0
FEATURE [PartDesign::Pad] Pad079
  BaseFeature = -> Pad078
  Direction = (0,0,1)
  Length = 3
  Length2 = 10
  Midplane = true
  Placement = pos=(0,0,18.5) rot=(0,0,1;0rad)
  Profile = -> Sketch141
  ReferenceAxis = -> Sketch141 [N_Axis]
  Type = 0
FEATURE [PartDesign::Pocket] Pocket051
  BaseFeature = -> Pad079
  Direction = (0,0,-1)
  Length = 5
  Length2 = 5
  Placement = pos=(0,0,18.5) rot=(0,0,1;0rad)
  Profile = -> Sketch138
  ReferenceAxis = -> Sketch138 [N_Axis]
  Reversed = true
  Type = 1
FEATURE [PartDesign::Chamfer] Chamfer
  Angle = 45
  Base = -> Pocket051 [Edge19,Edge7]
  BaseFeature = -> Pocket051
  ChamferType = 0
  FlipDirection = false
  Placement = pos=(0,0,18.5) rot=(0,0,1;0rad)
  Size = 0.3
  Size2 = 1
  SupportTransform = false
  UseAllEdges = false
FEATURE [PartDesign::Chamfer] Chamfer001
  Angle = 45
  Base = -> Chamfer [Edge22]
  BaseFeature = -> Chamfer
  ChamferType = 0
  FlipDirection = false
  Placement = pos=(0,0,18.5) rot=(0,0,1;0rad)
  Size = 0.3
  Size2 = 1
  SupportTransform = false
  UseAllEdges = false
FEATURE [Sketcher::SketchObject] Sketch
  AttachmentOffset = pos=(0,0,18.5) rot=(0,0,1;0rad)
  FullyConstrained = true
  MapMode = 5
  Placement = pos=(0,0,18.5) rot=(0,0,1;0rad)
  Support = -> [XY_Plane044]
  sketch-geometry (4):
    g0: LineSegment StartX=-15 StartY=5.15 StartZ=0 EndX=15 EndY=5.15 EndZ=0
    g1: LineSegment StartX=15 StartY=5.15 StartZ=0 EndX=15 EndY=-5.15 EndZ=0
    g2: LineSegment StartX=15 StartY=-5.15 StartZ=0 EndX=-15 EndY=-5.15 EndZ=0
    g3: LineSegment StartX=-15 StartY=-5.15 StartZ=0 EndX=-15 EndY=5.15 EndZ=0
  constraints (10):
    c: Coincident(g0,g1)
    c: Coincident(g1,g2)
    c: Coincident(g2,g3)
    c: Coincident(g3,g0)
    c: Horizontal(g0)
    c: Vertical(g1)
    c: Symmetric(g2,g1,g-2)
    c: Symmetric(g2,g0,g-1)
    c: Distance(g2) = 30
    c: Distance(g3) = 10.3
FEATURE [PartDesign::Pocket] Pocket
  BaseFeature = -> Chamfer001
  Direction = (0,0,-1)
  Length = 3.75
  Length2 = 5
  Placement = pos=(0,0,18.5) rot=(0,0,1;0rad)
  Profile = -> Sketch
  ReferenceAxis = -> Sketch [N_Axis]
  Type = 0
FEATURE [PartDesign::Body] Body028  label="IR Cam"
  Group = -> [Sketch136,Sketch138,Sketch141,Pad078,Pad079,Pocket051,Chamfer,Chamfer001,Sketch,Pocket]
  Origin = -> Origin044
  Placement = pos=(0,28.5,0) rot=(-1,0,0;1.5708rad)
  Tip = -> Pocket
FEATURE [App::MeasureDistance] Distance  label="Distance: 12.51 mm"
  Distance = 12.5134
  P1 = (9.89823,44.0673,10.5804)
  P2 = (18.2409,44.1607,19.9065)
